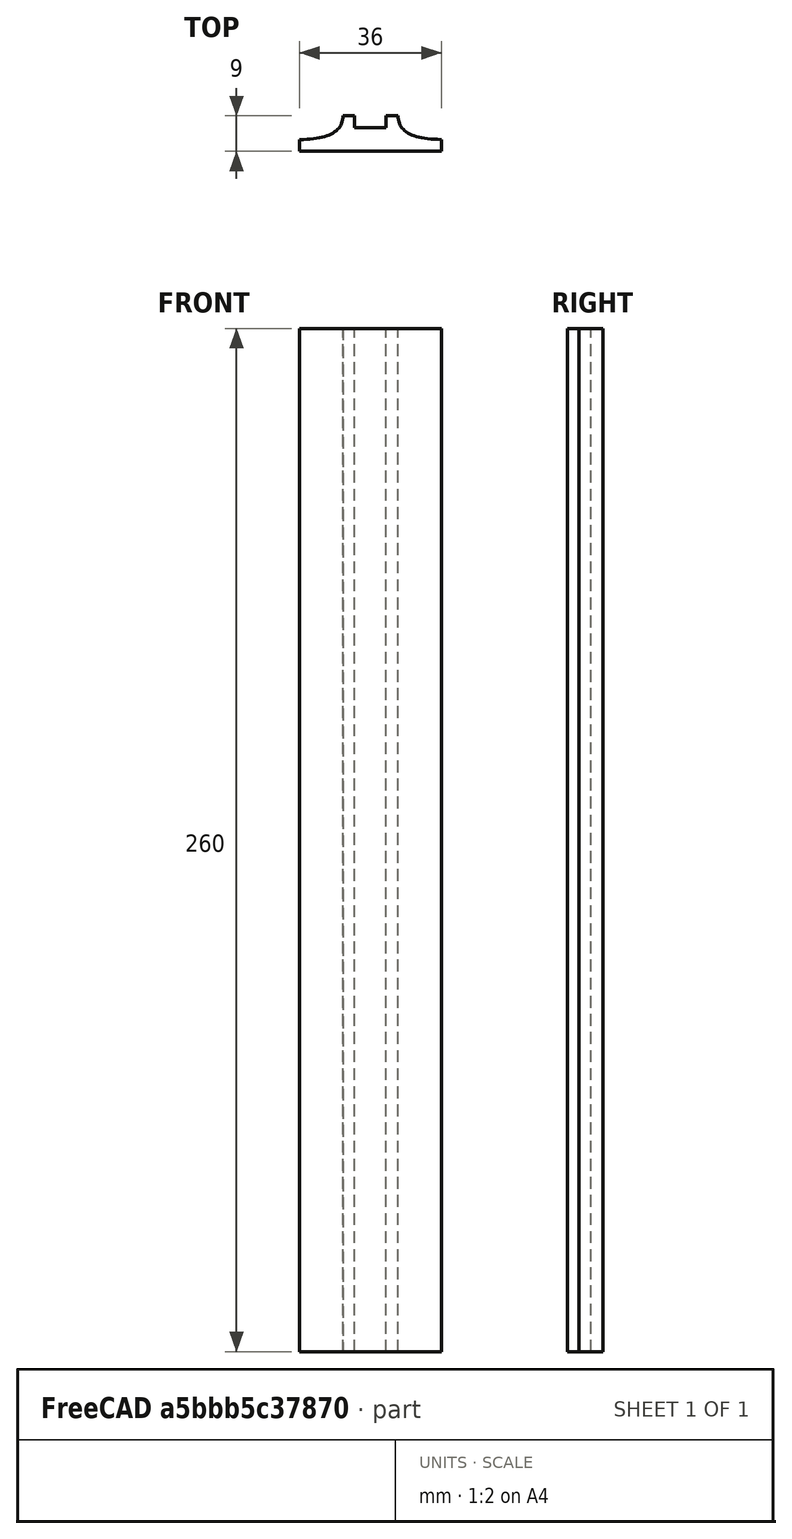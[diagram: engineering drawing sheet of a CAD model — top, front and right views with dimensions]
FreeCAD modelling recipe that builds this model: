
FCSTD DOCUMENT  (FreeCAD 0.19R0.19.2)
Label: laptopStand298.FCStd
License: All rights reserved
LicenseURL: http://en.wikipedia.org/wiki/All_rights_reserved
objects: Sketcher::SketchObject×10, Part::Extrusion×1
note: 11 computed .brp shape members not serialized (recipe doc carries the construction recipe); baked Part::Feature solids carry a one-line shape summary decoded from their .brp

FEATURE [Sketcher::SketchObject] Sketch001  label="legTop"
  FullyConstrained = true
  MapMode = 4
  Placement = pos=(0,0,0) rot=(0.57735,0.57735,0.57735;2.0944rad)
  sketch-geometry (41):
    g0: BSplineCurve PolesCount=3 KnotsCount=2 Degree=2 IsPeriodic=0
    g1: ArcOfCircle CenterX=73.1223 CenterY=-32.291 CenterZ=0 NormalX=0 NormalY=0 NormalZ=1 AngleXU=0 Radius=13 StartAngle=5.92268 EndAngle=9.06428
    g2: ArcOfCircle CenterX=66.7816 CenterY=-49.1439 CenterZ=0 NormalX=0 NormalY=0 NormalZ=1 AngleXU=0 Radius=13 StartAngle=2.78068 EndAngle=5.92131
    g3-g6: Circle x4 (B-spline internal-alignment scaffolding for g7; pole/knot coordinates omitted)
    g7: BSplineCurve PolesCount=4 KnotsCount=2 Degree=3 IsPeriodic=0
    g8: GeomPoint X=28.8094 Y=-19.0875 Z=0
    g9: GeomPoint X=47.0443 Y=-50.4712 Z=0
    g10: Circle CenterX=53.5586 CenterY=-23.2695 CenterZ=0 NormalX=0 NormalY=0 NormalZ=1 AngleXU=0 Radius=3.24518
    g11: LineSegment StartX=17.2232 StartY=-16.0875 StartZ=0 EndX=17.2232 EndY=-19.0875 EndZ=0
    g12: ArcOfCircle CenterX=17.2475 CenterY=-181.166 CenterZ=0 NormalX=0 NormalY=0 NormalZ=1 AngleXU=0 Radius=13 StartAngle=5.92268 EndAngle=7.49361
    g13: ArcOfCircle CenterX=29.5716 CenterY=-148.408 CenterZ=0 NormalX=0 NormalY=0 NormalZ=1 AngleXU=0 Radius=13 StartAngle=4.35228 EndAngle=5.92131
    g14: ArcOfCircle CenterX=35.8967 CenterY=-131.555 CenterZ=0 NormalX=0 NormalY=0 NormalZ=1 AngleXU=0 Radius=13 StartAngle=5.92268 EndAngle=7.49902
    g15: ArcOfCircle CenterX=48.1805 CenterY=-98.7782 CenterZ=0 NormalX=0 NormalY=0 NormalZ=1 AngleXU=0 Radius=13 StartAngle=4.34921 EndAngle=5.92131
    g16: ArcOfCircle CenterX=54.5183 CenterY=-81.9247 CenterZ=0 NormalX=0 NormalY=0 NormalZ=1 AngleXU=0 Radius=13 StartAngle=5.92268 EndAngle=8.70432
    g17: ArcOfCircle CenterX=20.184 CenterY=-217.506 CenterZ=0 NormalX=0 NormalY=0 NormalZ=1 AngleXU=0 Radius=3.81084 StartAngle=1.88136 EndAngle=6.80465
    g18: ArcOfCircle CenterX=36.3663 CenterY=-113.042 CenterZ=0 NormalX=0 NormalY=0 NormalZ=1 AngleXU=0 Radius=3.60555 StartAngle=0.230024 EndAngle=5.3372
    g19: ArcOfCircle CenterX=17.7945 CenterY=-162.686 CenterZ=0 NormalX=0 NormalY=0 NormalZ=1 AngleXU=0 Radius=3.60555 StartAngle=0.230024 EndAngle=5.3372
    g20: ArcOfCircle CenterX=49.8795 CenterY=-62.6074 CenterZ=0 NormalX=0 NormalY=0 NormalZ=1 AngleXU=0 Radius=3.84187 StartAngle=4.46973 EndAngle=9.40343
    g21: LineSegment StartX=48.9563 StartY=-66.3367 StartZ=0 EndX=44.7488 EndY=-73.3482 EndZ=0
    g22: LineSegment StartX=41.085 StartY=-66.3176 StartZ=0 EndX=46.0385 EndY=-62.5254 EndZ=0
    g23: LineSegment StartX=47.0443 StartY=-50.4712 StartZ=0 EndX=41.085 EndY=-66.3176 EndZ=0
    g24: LineSegment StartX=17.2232 StartY=-16.0875 StartZ=0 EndX=117.223 EndY=-16.0875 EndZ=0
    g25: LineSegment StartX=28.8094 StartY=-19.0875 StartZ=0 EndX=17.2232 EndY=-19.0875 EndZ=0
    g26: LineSegment StartX=117.223 StartY=-16.0875 StartZ=0 EndX=117.223 EndY=-19.0875 EndZ=0
    g27: LineSegment StartX=85.2866 StartY=-36.8766 StartZ=0 EndX=78.9396 EndY=-53.7463 EndZ=0
    g28: LineSegment StartX=60.9579 StartY=-27.7053 StartZ=0 EndX=54.6191 EndY=-44.5532 EndZ=0
    g29: LineSegment StartX=23.4884 StartY=-215.608 StartZ=0 EndX=94.6579 EndY=-26.1359 EndZ=0
    g30: LineSegment StartX=19.0195 StartY=-213.878 StartZ=0 EndX=29.4118 EndY=-185.752 EndZ=0
    g31: LineSegment StartX=22.7134 StartY=-166.661 StartZ=0 EndX=21.8316 EndY=-169.001 EndZ=0
    g32: LineSegment StartX=19.9036 StartY=-165.61 StartZ=0 EndX=22.7134 EndY=-166.661 EndZ=0
    g33: LineSegment StartX=21.3051 StartY=-161.864 StartZ=0 EndX=24.1149 EndY=-162.915 EndZ=0
    g34: LineSegment StartX=24.1149 StartY=-162.915 StartZ=0 EndX=24.9906 EndY=-160.574 EndZ=0
    g35: LineSegment StartX=41.7296 StartY=-153.01 StartZ=0 EndX=48.061 EndY=-136.14 EndZ=0
    g36: LineSegment StartX=41.2852 StartY=-117.017 StartZ=0 EndX=40.4148 EndY=-119.365 EndZ=0
    g37: LineSegment StartX=38.4753 StartY=-115.966 StartZ=0 EndX=41.2852 EndY=-117.017 EndZ=0
    g38: LineSegment StartX=39.8769 StartY=-112.22 StartZ=0 EndX=42.6867 EndY=-113.271 EndZ=0
    g39: LineSegment StartX=42.6867 StartY=-113.271 StartZ=0 EndX=43.5622 EndY=-110.93 EndZ=0
    g40: LineSegment StartX=66.6827 StartY=-86.5104 StartZ=0 EndX=60.3386 EndY=-103.381 EndZ=0
  constraints (65):
    c: Block(g0)
    c: Block(g1)
    c: Block(g2)
    c: Weight(g3) = 1
    c: Equal(g3,g4)
    c: Equal(g3,g5)
    c: Equal(g3,g6)
    c: InternalAlignment(g3-g6 -> g7) x4
    c: InternalAlignment(g8,g7)
    c: InternalAlignment(g9,g7)
    c: Block(g10)
    c: Block(g7)
    c: Vertical(g11)
    c: Block(g12)
    c: Block(g13)
    c: Block(g14)
    c: Block(g15)
    c: Block(g16)
    c: Block(g17)
    c: Block(g18)
    c: Block(g19)
    c: Block(g20)
    c: Coincident(g21,g20)
    c: Coincident(g21,g16)
    c: Coincident(g22,g20)
    c: Block(g22)
    c: Coincident(g23,g7)
    c: Coincident(g23,g22)
    c: Coincident(g24,g11)
    c: Horizontal(g24)
    c: Coincident(g25,g7)
    c: Coincident(g25,g11)
    c: Horizontal(g25)
    c: Coincident(g26,g24)
    c: Coincident(g26,g0)
    c: Vertical(g26)
    c: Block(g24)
    c: Coincident(g27,g1)
    c: Coincident(g27,g2)
    c: Coincident(g28,g1)
    c: Coincident(g28,g2)
    c: Coincident(g29,g17)
    c: Coincident(g29,g0)
    c: Coincident(g30,g17)
    c: Coincident(g30,g12)
    c: Coincident(g31,g12)
    c: Coincident(g32,g19)
    c: Coincident(g32,g31)
    c: Block(g31)
    c: Coincident(g33,g19)
    c: Coincident(g34,g33)
    c: Coincident(g34,g13)
    c: Block(g34)
    c: Coincident(g35,g13)
    c: Coincident(g35,g14)
    c: Coincident(g36,g14)
    c: Coincident(g37,g18)
    c: Coincident(g37,g36)
    c: Block(g36)
    c: Coincident(g38,g18)
    c: Coincident(g39,g38)
    c: Coincident(g39,g15)
    c: Block(g39)
    c: Coincident(g40,g16)
    c: Coincident(g40,g15)
FEATURE [Sketcher::SketchObject] Sketch002
  FullyConstrained = true
  sketch-geometry (20):
    g0: LineSegment StartX=-2.77179 StartY=-200.304 StartZ=0 EndX=5.22821 EndY=-200.304 EndZ=0
    g1: LineSegment StartX=5.22821 StartY=-200.304 StartZ=0 EndX=5.22821 EndY=-197.304 EndZ=0
    g2: LineSegment StartX=-2.77179 StartY=-200.304 StartZ=0 EndX=-2.77179 EndY=-197.304 EndZ=0
    g3: LineSegment StartX=5.22821 StartY=-197.304 StartZ=0 EndX=8.22821 EndY=-197.304 EndZ=0
    g4: LineSegment StartX=-2.77179 StartY=-197.304 StartZ=0 EndX=-5.77179 EndY=-197.304 EndZ=0
    g5: LineSegment StartX=19.2282 StartY=-203.304 StartZ=0 EndX=19.2282 EndY=-206.304 EndZ=0
    g6: LineSegment StartX=-16.7718 StartY=-203.304 StartZ=0 EndX=-16.7718 EndY=-206.304 EndZ=0
    g7: LineSegment StartX=-16.7718 StartY=-206.304 StartZ=0 EndX=19.2282 EndY=-206.304 EndZ=0
    g8: Circle CenterX=-16.7718 CenterY=-203.304 CenterZ=0 NormalX=0 NormalY=0 NormalZ=1 AngleXU=0 Radius=1
    g9: Circle CenterX=-5.77179 CenterY=-203.304 CenterZ=0 NormalX=0 NormalY=0 NormalZ=1 AngleXU=0 Radius=1
    g10: Circle CenterX=-5.77179 CenterY=-197.304 CenterZ=0 NormalX=0 NormalY=0 NormalZ=1 AngleXU=0 Radius=1
    g11: BSplineCurve PolesCount=3 KnotsCount=2 Degree=2 IsPeriodic=0
    g12: GeomPoint X=-16.7718 Y=-203.304 Z=0
    g13: GeomPoint X=-5.77179 Y=-197.304 Z=0
    g14: Circle CenterX=19.2282 CenterY=-203.304 CenterZ=0 NormalX=0 NormalY=0 NormalZ=1 AngleXU=0 Radius=1
    g15: Circle CenterX=8.22821 CenterY=-203.304 CenterZ=0 NormalX=0 NormalY=0 NormalZ=1 AngleXU=0 Radius=1
    g16: Circle CenterX=8.22821 CenterY=-197.304 CenterZ=0 NormalX=0 NormalY=0 NormalZ=1 AngleXU=0 Radius=1
    g17: BSplineCurve PolesCount=3 KnotsCount=2 Degree=2 IsPeriodic=0
    g18: GeomPoint X=19.2282 Y=-203.304 Z=0
    g19: GeomPoint X=8.22821 Y=-197.304 Z=0
  constraints (41):
    c: Horizontal(g0)
    c: Distance(g0) = 8
    c: Coincident(g1,g0)
    c: Vertical(g1)
    c: Distance(g1) = 3
    c: Coincident(g2,g0)
    c: Vertical(g2)
    c: Distance(g2) = 3
    c: Coincident(g3,g1)
    c: Horizontal(g3)
    c: Distance(g3) = 3
    c: Coincident(g4,g2)
    c: Horizontal(g4)
    c: Distance(g4) = 3
    c: Vertical(g5)
    c: Vertical(g6)
    c: Coincident(g7,g6)
    c: Coincident(g7,g5)
    c: Weight(g8) = 1
    c: Equal(g8,g9)
    c: Equal(g8,g10)
    c: Coincident(g11,g4)
    c: InternalAlignment(g8,g11)
    c: InternalAlignment(g9,g11)
    c: InternalAlignment(g10,g11)
    c: InternalAlignment(g12,g11)
    c: InternalAlignment(g13,g11)
    c: Coincident(g17,g5)
    c: Weight(g14) = 1
    c: Equal(g14,g15)
    c: Equal(g14,g16)
    c: Coincident(g17,g3)
    c: InternalAlignment(g14,g17)
    c: InternalAlignment(g15,g17)
    c: InternalAlignment(g16,g17)
    c: InternalAlignment(g18,g17)
    c: InternalAlignment(g19,g17)
    c: Block(g7)
    c: Block(g17)
    c: Block(g11)
    c: Block(g6)
FEATURE [Part::Extrusion] Extrude003
  Base = -> Sketch002
  Dir = (0,0,1)
  DirMode = 2
  FaceMakerClass = Part::FaceMakerBullseye
  LengthFwd = 260
  LengthRev = 0
  Solid = true
  Symmetric = false
FEATURE [Sketcher::SketchObject] Sketch003  label="original"
  FullyConstrained = false
  sketch-geometry (469):
    g0: LineSegment StartX=-42.9272 StartY=136.221 StartZ=0 EndX=-42.9272 EndY=-103.779 EndZ=0
    g1: LineSegment StartX=407.073 StartY=136.221 StartZ=0 EndX=407.073 EndY=-103.779 EndZ=0
    g2: ArcOfCircle CenterX=-26.9272 CenterY=-83.7794 CenterZ=0 NormalX=0 NormalY=0 NormalZ=1 AngleXU=0 Radius=8 StartAngle=3.14159 EndAngle=6.28319
    g3: ArcOfCircle CenterX=391.073 CenterY=-83.7794 CenterZ=0 NormalX=0 NormalY=0 NormalZ=1 AngleXU=0 Radius=8 StartAngle=3.14159 EndAngle=6.28319
    g4: Circle CenterX=175.022 CenterY=27.0628 CenterZ=0 NormalX=0 NormalY=0 NormalZ=1 AngleXU=0 Radius=1
    g5: Circle CenterX=179.022 CenterY=24.8665 CenterZ=0 NormalX=0 NormalY=0 NormalZ=1 AngleXU=0 Radius=1
    g6: Circle CenterX=179.022 CenterY=27.0628 CenterZ=0 NormalX=0 NormalY=0 NormalZ=1 AngleXU=0 Radius=1
    g7: BSplineCurve PolesCount=3 KnotsCount=2 Degree=2 IsPeriodic=0
    g8: GeomPoint X=175.022 Y=27.0628 Z=0
    g9: GeomPoint X=179.022 Y=27.0628 Z=0
    g10: Circle CenterX=189.124 CenterY=27.0628 CenterZ=0 NormalX=0 NormalY=0 NormalZ=1 AngleXU=0 Radius=1
    g11: Circle CenterX=185.124 CenterY=24.8665 CenterZ=0 NormalX=0 NormalY=0 NormalZ=1 AngleXU=0 Radius=1
    g12: Circle CenterX=185.124 CenterY=27.0628 CenterZ=0 NormalX=0 NormalY=0 NormalZ=1 AngleXU=0 Radius=1
    g13: BSplineCurve PolesCount=3 KnotsCount=2 Degree=2 IsPeriodic=0
    g14: GeomPoint X=189.124 Y=27.0628 Z=0
    g15: GeomPoint X=185.124 Y=27.0628 Z=0
    g16: Circle CenterX=175.022 CenterY=5.37834 CenterZ=0 NormalX=0 NormalY=0 NormalZ=1 AngleXU=0 Radius=1
    g17: Circle CenterX=179.022 CenterY=7.57463 CenterZ=0 NormalX=0 NormalY=0 NormalZ=1 AngleXU=0 Radius=1
    g18: Circle CenterX=179.022 CenterY=5.34704 CenterZ=0 NormalX=0 NormalY=0 NormalZ=1 AngleXU=0 Radius=1
    g19: BSplineCurve PolesCount=3 KnotsCount=2 Degree=2 IsPeriodic=0
    g20: GeomPoint X=175.022 Y=5.37834 Z=0
    g21: GeomPoint X=179.022 Y=5.34704 Z=0
    g22: Circle CenterX=189.124 CenterY=5.37834 CenterZ=0 NormalX=0 NormalY=0 NormalZ=1 AngleXU=0 Radius=1
    g23: Circle CenterX=185.124 CenterY=7.57463 CenterZ=0 NormalX=0 NormalY=0 NormalZ=1 AngleXU=0 Radius=1
    g24: Circle CenterX=185.124 CenterY=5.34704 CenterZ=0 NormalX=0 NormalY=0 NormalZ=1 AngleXU=0 Radius=1
    g25: BSplineCurve PolesCount=3 KnotsCount=2 Degree=2 IsPeriodic=0
    g26: GeomPoint X=189.124 Y=5.37834 Z=0
    g27: GeomPoint X=185.124 Y=5.34704 Z=0
    g28: Circle CenterX=165.871 CenterY=18.1458 CenterZ=0 NormalX=0 NormalY=0 NormalZ=1 AngleXU=0 Radius=1
    g29: Circle CenterX=169.377 CenterY=16.2206 CenterZ=0 NormalX=0 NormalY=0 NormalZ=1 AngleXU=0 Radius=1
    g30: Circle CenterX=165.871 CenterY=14.2956 CenterZ=0 NormalX=0 NormalY=0 NormalZ=1 AngleXU=0 Radius=1
    g31: BSplineCurve PolesCount=3 KnotsCount=2 Degree=2 IsPeriodic=0
    g32: GeomPoint X=165.871 Y=18.1458 Z=0
    g33: GeomPoint X=165.871 Y=14.2956 Z=0
    g34: Circle CenterX=198.275 CenterY=18.1318 CenterZ=0 NormalX=0 NormalY=0 NormalZ=1 AngleXU=0 Radius=1
    g35: Circle CenterX=194.768 CenterY=16.2206 CenterZ=0 NormalX=0 NormalY=0 NormalZ=1 AngleXU=0 Radius=1
    g36: Circle CenterX=198.264 CenterY=14.2963 CenterZ=0 NormalX=0 NormalY=0 NormalZ=1 AngleXU=0 Radius=1
    g37: BSplineCurve PolesCount=3 KnotsCount=2 Degree=2 IsPeriodic=0
    g38: GeomPoint X=198.275 Y=18.1318 Z=0
    g39: GeomPoint X=198.264 Y=14.2963 Z=0
    g40: LineSegment StartX=407.073 StartY=-103.779 StartZ=0 EndX=-42.9272 EndY=-103.779 EndZ=0
    g41: Circle CenterX=125.607 CenterY=54.1951 CenterZ=0 NormalX=0 NormalY=0 NormalZ=1 AngleXU=0 Radius=1
    g42: Circle CenterX=139.632 CenterY=46.4944 CenterZ=0 NormalX=0 NormalY=0 NormalZ=1 AngleXU=0 Radius=1
    g43: Circle CenterX=127.326 CenterY=56.7187 CenterZ=0 NormalX=0 NormalY=0 NormalZ=1 AngleXU=0 Radius=1
    g44: BSplineCurve PolesCount=3 KnotsCount=2 Degree=2 IsPeriodic=0
    g45: GeomPoint X=125.607 Y=54.1951 Z=0
    g46: GeomPoint X=127.326 Y=56.7187 Z=0
    g47: Circle CenterX=236.824 CenterY=56.7187 CenterZ=0 NormalX=0 NormalY=0 NormalZ=1 AngleXU=0 Radius=1
    g48: Circle CenterX=224.513 CenterY=46.4944 CenterZ=0 NormalX=0 NormalY=0 NormalZ=1 AngleXU=0 Radius=1
    g49: Circle CenterX=238.538 CenterY=54.1951 CenterZ=0 NormalX=0 NormalY=0 NormalZ=1 AngleXU=0 Radius=1
    g50: BSplineCurve PolesCount=3 KnotsCount=2 Degree=2 IsPeriodic=0
    g51: GeomPoint X=236.824 Y=56.7187 Z=0
    g52: GeomPoint X=238.538 Y=54.1951 Z=0
    g53: Circle CenterX=238.538 CenterY=-21.7516 CenterZ=0 NormalX=0 NormalY=0 NormalZ=1 AngleXU=0 Radius=1
    g54: Circle CenterX=224.513 CenterY=-14.0532 CenterZ=0 NormalX=0 NormalY=0 NormalZ=1 AngleXU=0 Radius=1
    g55: Circle CenterX=236.584 CenterY=-24.2775 CenterZ=0 NormalX=0 NormalY=0 NormalZ=1 AngleXU=0 Radius=1
    g56: BSplineCurve PolesCount=3 KnotsCount=2 Degree=2 IsPeriodic=0
    g57: GeomPoint X=238.538 Y=-21.7516 Z=0
    g58: GeomPoint X=236.584 Y=-24.2775 Z=0
    g59: Circle CenterX=125.607 CenterY=-21.7539 CenterZ=0 NormalX=0 NormalY=0 NormalZ=1 AngleXU=0 Radius=1
    g60: Circle CenterX=139.632 CenterY=-14.0532 CenterZ=0 NormalX=0 NormalY=0 NormalZ=1 AngleXU=0 Radius=1
    g61: Circle CenterX=127.325 CenterY=-24.2775 CenterZ=0 NormalX=0 NormalY=0 NormalZ=1 AngleXU=0 Radius=1
    g62: BSplineCurve PolesCount=3 KnotsCount=2 Degree=2 IsPeriodic=0
    g63: GeomPoint X=125.607 Y=-21.7539 Z=0
    g64: GeomPoint X=127.325 Y=-24.2775 Z=0
    g65: Circle CenterX=302.996 CenterY=111.695 CenterZ=0 NormalX=0 NormalY=0 NormalZ=1 AngleXU=0 Radius=1
    g66: Circle CenterX=306.073 CenterY=114.251 CenterZ=0 NormalX=0 NormalY=0 NormalZ=1 AngleXU=0 Radius=1
    g67: Circle CenterX=306.073 CenterY=110.251 CenterZ=0 NormalX=0 NormalY=0 NormalZ=1 AngleXU=0 Radius=1
    g68: BSplineCurve PolesCount=3 KnotsCount=2 Degree=2 IsPeriodic=0
    g69: GeomPoint X=302.996 Y=111.695 Z=0
    g70: GeomPoint X=306.073 Y=110.251 Z=0
    g71: Circle CenterX=306.073 CenterY=95.2763 CenterZ=0 NormalX=0 NormalY=0 NormalZ=1 AngleXU=0 Radius=1
    g72: Circle CenterX=306.073 CenterY=91.2763 CenterZ=0 NormalX=0 NormalY=0 NormalZ=1 AngleXU=0 Radius=1
    g73: Circle CenterX=302.567 CenterY=89.3511 CenterZ=0 NormalX=0 NormalY=0 NormalZ=1 AngleXU=0 Radius=1
    g74: BSplineCurve PolesCount=3 KnotsCount=2 Degree=2 IsPeriodic=0
    g75: GeomPoint X=306.073 Y=95.2763 Z=0
    g76: GeomPoint X=302.567 Y=89.3511 Z=0
    g77: LineSegment StartX=306.073 StartY=110.251 StartZ=0 EndX=306.073 EndY=95.2763 EndZ=0
    g78: LineSegment StartX=302.996 StartY=111.695 StartZ=0 EndX=236.824 EndY=56.7187 EndZ=0
    g79: LineSegment StartX=238.538 StartY=54.1951 StartZ=0 EndX=302.567 EndY=89.3511 EndZ=0
    g80: Circle CenterX=61.1496 CenterY=111.695 CenterZ=0 NormalX=0 NormalY=0 NormalZ=1 AngleXU=0 Radius=1
    g81: Circle CenterX=58.0728 CenterY=114.251 CenterZ=0 NormalX=0 NormalY=0 NormalZ=1 AngleXU=0 Radius=1
    g82: Circle CenterX=58.0728 CenterY=110.251 CenterZ=0 NormalX=0 NormalY=0 NormalZ=1 AngleXU=0 Radius=1
    g83: BSplineCurve PolesCount=3 KnotsCount=2 Degree=2 IsPeriodic=0
    g84: GeomPoint X=61.1496 Y=111.695 Z=0
    g85: GeomPoint X=58.0728 Y=110.251 Z=0
    g86: Circle CenterX=61.5791 CenterY=89.3511 CenterZ=0 NormalX=0 NormalY=0 NormalZ=1 AngleXU=0 Radius=1
    g87: Circle CenterX=58.0728 CenterY=91.2763 CenterZ=0 NormalX=0 NormalY=0 NormalZ=1 AngleXU=0 Radius=1
    g88: Circle CenterX=58.0728 CenterY=95.2763 CenterZ=0 NormalX=0 NormalY=0 NormalZ=1 AngleXU=0 Radius=1
    g89: BSplineCurve PolesCount=3 KnotsCount=2 Degree=2 IsPeriodic=0
    g90: GeomPoint X=61.5791 Y=89.3511 Z=0
    g91: GeomPoint X=58.0728 Y=95.2763 Z=0
    g92: LineSegment StartX=58.0728 StartY=110.251 StartZ=0 EndX=58.0728 EndY=95.2763 EndZ=0
    g93: LineSegment StartX=61.1496 StartY=111.695 StartZ=0 EndX=127.326 EndY=56.7187 EndZ=0
    g94: LineSegment StartX=125.607 StartY=54.1951 StartZ=0 EndX=61.5791 EndY=89.3511 EndZ=0
    g95: Circle CenterX=61.5791 CenterY=-56.9099 CenterZ=0 NormalX=0 NormalY=0 NormalZ=1 AngleXU=0 Radius=1
    g96: Circle CenterX=58.0728 CenterY=-58.8351 CenterZ=0 NormalX=0 NormalY=0 NormalZ=1 AngleXU=0 Radius=1
    g97: Circle CenterX=58.0728 CenterY=-62.8351 CenterZ=0 NormalX=0 NormalY=0 NormalZ=1 AngleXU=0 Radius=1
    g98: BSplineCurve PolesCount=3 KnotsCount=2 Degree=2 IsPeriodic=0
    g99: GeomPoint X=61.5791 Y=-56.9099 Z=0
    g100: GeomPoint X=58.0728 Y=-62.8351 Z=0
    g101: Circle CenterX=58.0728 CenterY=-77.8102 CenterZ=0 NormalX=0 NormalY=0 NormalZ=1 AngleXU=0 Radius=1
    g102: Circle CenterX=58.0728 CenterY=-81.8102 CenterZ=0 NormalX=0 NormalY=0 NormalZ=1 AngleXU=0 Radius=1
    g103: Circle CenterX=61.1496 CenterY=-79.2541 CenterZ=0 NormalX=0 NormalY=0 NormalZ=1 AngleXU=0 Radius=1
    g104: BSplineCurve PolesCount=3 KnotsCount=2 Degree=2 IsPeriodic=0
    g105: GeomPoint X=58.0728 Y=-77.8102 Z=0
    g106: GeomPoint X=61.1496 Y=-79.2541 Z=0
    g107: LineSegment StartX=58.0728 StartY=-62.8351 StartZ=0 EndX=58.0728 EndY=-77.8102 EndZ=0
    g108: LineSegment StartX=61.1496 StartY=-79.2541 StartZ=0 EndX=127.325 EndY=-24.2775 EndZ=0
    g109: LineSegment StartX=125.607 StartY=-21.7539 StartZ=0 EndX=61.5791 EndY=-56.9099 EndZ=0
    g110: Circle CenterX=302.567 CenterY=-56.9099 CenterZ=0 NormalX=0 NormalY=0 NormalZ=1 AngleXU=0 Radius=1
    g111: Circle CenterX=306.073 CenterY=-58.8351 CenterZ=0 NormalX=0 NormalY=0 NormalZ=1 AngleXU=0 Radius=1
    g112: Circle CenterX=306.073 CenterY=-62.8351 CenterZ=0 NormalX=0 NormalY=0 NormalZ=1 AngleXU=0 Radius=1
    g113: BSplineCurve PolesCount=3 KnotsCount=2 Degree=2 IsPeriodic=0
    g114: GeomPoint X=302.567 Y=-56.9099 Z=0
    g115: GeomPoint X=306.073 Y=-62.8351 Z=0
    g116: Circle CenterX=302.996 CenterY=-79.2541 CenterZ=0 NormalX=0 NormalY=0 NormalZ=1 AngleXU=0 Radius=1
    g117: Circle CenterX=306.073 CenterY=-81.8102 CenterZ=0 NormalX=0 NormalY=0 NormalZ=1 AngleXU=0 Radius=1
    g118: Circle CenterX=306.073 CenterY=-77.8102 CenterZ=0 NormalX=0 NormalY=0 NormalZ=1 AngleXU=0 Radius=1
    g119: BSplineCurve PolesCount=3 KnotsCount=2 Degree=2 IsPeriodic=0
    g120: GeomPoint X=302.996 Y=-79.2541 Z=0
    g121: GeomPoint X=306.073 Y=-77.8102 Z=0
    g122: LineSegment StartX=306.073 StartY=-62.8351 StartZ=0 EndX=306.073 EndY=-77.8102 EndZ=0
    g123: LineSegment StartX=302.996 StartY=-79.2541 StartZ=0 EndX=236.584 EndY=-24.2775 EndZ=0
    g124: LineSegment StartX=238.538 StartY=-21.7516 StartZ=0 EndX=302.567 EndY=-56.9099 EndZ=0
    g125: Circle CenterX=61.6457 CenterY=-88.8112 CenterZ=0 NormalX=0 NormalY=0 NormalZ=1 AngleXU=0 Radius=1
    g126: Circle CenterX=58.0728 CenterY=-91.7794 CenterZ=0 NormalX=0 NormalY=0 NormalZ=1 AngleXU=0 Radius=1
    g127: Circle CenterX=63.9135 CenterY=-91.7791 CenterZ=0 NormalX=0 NormalY=0 NormalZ=1 AngleXU=0 Radius=1
    g128: BSplineCurve PolesCount=3 KnotsCount=2 Degree=2 IsPeriodic=0
    g129: GeomPoint X=61.6457 Y=-88.8112 Z=0
    g130: GeomPoint X=63.9135 Y=-91.7791 Z=0
    g131: Circle CenterX=179.022 CenterY=-85.8163 CenterZ=0 NormalX=0 NormalY=0 NormalZ=1 AngleXU=0 Radius=1
    g132: Circle CenterX=179.022 CenterY=-91.7794 CenterZ=0 NormalX=0 NormalY=0 NormalZ=1 AngleXU=0 Radius=1
    g133: Circle CenterX=171.895 CenterY=-91.7791 CenterZ=0 NormalX=0 NormalY=0 NormalZ=1 AngleXU=0 Radius=1
    g134: BSplineCurve PolesCount=3 KnotsCount=2 Degree=2 IsPeriodic=0
    g135: GeomPoint X=179.022 Y=-85.8163 Z=0
    g136: GeomPoint X=171.895 Y=-91.7791 Z=0
    g137: Circle CenterX=185.124 CenterY=-86.2028 CenterZ=0 NormalX=0 NormalY=0 NormalZ=1 AngleXU=0 Radius=1
    g138: Circle CenterX=185.124 CenterY=-91.7794 CenterZ=0 NormalX=0 NormalY=0 NormalZ=1 AngleXU=0 Radius=1
    g139: Circle CenterX=191.747 CenterY=-91.7794 CenterZ=0 NormalX=0 NormalY=0 NormalZ=1 AngleXU=0 Radius=1
    g140: BSplineCurve PolesCount=3 KnotsCount=2 Degree=2 IsPeriodic=0
    g141: GeomPoint X=185.124 Y=-86.2028 Z=0
    g142: GeomPoint X=191.747 Y=-91.7794 Z=0
    g143: Circle CenterX=299.888 CenterY=-86.6413 CenterZ=0 NormalX=0 NormalY=0 NormalZ=1 AngleXU=0 Radius=1
    g144: Circle CenterX=306.073 CenterY=-91.7794 CenterZ=0 NormalX=0 NormalY=0 NormalZ=1 AngleXU=0 Radius=1
    g145: Circle CenterX=298.776 CenterY=-91.7794 CenterZ=0 NormalX=0 NormalY=0 NormalZ=1 AngleXU=0 Radius=1
    g146: BSplineCurve PolesCount=3 KnotsCount=2 Degree=2 IsPeriodic=0
    g147: GeomPoint X=299.888 Y=-86.6413 Z=0
    g148: GeomPoint X=298.776 Y=-91.7794 Z=0
    g149: LineSegment StartX=189.124 StartY=5.37834 StartZ=0 EndX=299.888 EndY=-86.6413 EndZ=0
    g150: LineSegment StartX=298.776 StartY=-91.7794 StartZ=0 EndX=191.747 EndY=-91.7794 EndZ=0
    g151: LineSegment StartX=185.124 StartY=-86.2028 StartZ=0 EndX=185.124 EndY=5.34704 EndZ=0
    g152: LineSegment StartX=179.022 StartY=5.34704 StartZ=0 EndX=179.022 EndY=-85.8163 EndZ=0
    g153: LineSegment StartX=171.895 StartY=-91.7791 StartZ=0 EndX=63.9135 EndY=-91.7791 EndZ=0
    g154: LineSegment StartX=61.6457 StartY=-88.8112 StartZ=0 EndX=175.022 EndY=5.37834 EndZ=0
    g155: Circle CenterX=302.073 CenterY=124.221 CenterZ=0 NormalX=0 NormalY=0 NormalZ=1 AngleXU=0 Radius=1
    g156: Circle CenterX=306.073 CenterY=124.221 CenterZ=0 NormalX=0 NormalY=0 NormalZ=1 AngleXU=0 Radius=1
    g157: Circle CenterX=302.996 CenterY=121.665 CenterZ=0 NormalX=0 NormalY=0 NormalZ=1 AngleXU=0 Radius=1
    g158: BSplineCurve PolesCount=3 KnotsCount=2 Degree=2 IsPeriodic=0
    g159: GeomPoint X=302.073 Y=124.221 Z=0
    g160: GeomPoint X=302.996 Y=121.665 Z=0
    g161: Circle CenterX=189.124 CenterY=124.221 CenterZ=0 NormalX=0 NormalY=0 NormalZ=1 AngleXU=0 Radius=1
    g162: Circle CenterX=185.124 CenterY=124.221 CenterZ=0 NormalX=0 NormalY=0 NormalZ=1 AngleXU=0 Radius=1
    g163: Circle CenterX=185.124 CenterY=120.221 CenterZ=0 NormalX=0 NormalY=0 NormalZ=1 AngleXU=0 Radius=1
    g164: BSplineCurve PolesCount=3 KnotsCount=2 Degree=2 IsPeriodic=0
    g165: GeomPoint X=189.124 Y=124.221 Z=0
    g166: GeomPoint X=185.124 Y=120.221 Z=0
    g167: Circle CenterX=175.022 CenterY=124.221 CenterZ=0 NormalX=0 NormalY=0 NormalZ=1 AngleXU=0 Radius=1
    g168: Circle CenterX=179.022 CenterY=124.221 CenterZ=0 NormalX=0 NormalY=0 NormalZ=1 AngleXU=0 Radius=1
    g169: Circle CenterX=179.022 CenterY=120.221 CenterZ=0 NormalX=0 NormalY=0 NormalZ=1 AngleXU=0 Radius=1
    g170: BSplineCurve PolesCount=3 KnotsCount=2 Degree=2 IsPeriodic=0
    g171: GeomPoint X=175.022 Y=124.221 Z=0
    g172: GeomPoint X=179.022 Y=120.221 Z=0
    g173: Circle CenterX=62.0728 CenterY=124.221 CenterZ=0 NormalX=0 NormalY=0 NormalZ=1 AngleXU=0 Radius=1
    g174: Circle CenterX=58.0728 CenterY=124.221 CenterZ=0 NormalX=0 NormalY=0 NormalZ=1 AngleXU=0 Radius=1
    g175: Circle CenterX=61.1496 CenterY=121.665 CenterZ=0 NormalX=0 NormalY=0 NormalZ=1 AngleXU=0 Radius=1
    g176: BSplineCurve PolesCount=3 KnotsCount=2 Degree=2 IsPeriodic=0
    g177: GeomPoint X=62.0728 Y=124.221 Z=0
    g178: GeomPoint X=61.1496 Y=121.665 Z=0
    g179: LineSegment StartX=179.022 StartY=120.221 StartZ=0 EndX=179.022 EndY=27.0628 EndZ=0
    g180: LineSegment StartX=185.124 StartY=27.0628 StartZ=0 EndX=185.124 EndY=120.221 EndZ=0
    g181: LineSegment StartX=302.996 StartY=121.665 StartZ=0 EndX=189.124 EndY=27.0628 EndZ=0
    g182: LineSegment StartX=175.022 StartY=27.0628 StartZ=0 EndX=61.1496 EndY=121.665 EndZ=0
    g183: Circle CenterX=61.5791 CenterY=75.4095 CenterZ=0 NormalX=0 NormalY=0 NormalZ=1 AngleXU=0 Radius=1
    g184: Circle CenterX=58.0728 CenterY=77.3346 CenterZ=0 NormalX=0 NormalY=0 NormalZ=1 AngleXU=0 Radius=1
    g185: Circle CenterX=58.0728 CenterY=73.3346 CenterZ=0 NormalX=0 NormalY=0 NormalZ=1 AngleXU=0 Radius=1
    g186: BSplineCurve PolesCount=3 KnotsCount=2 Degree=2 IsPeriodic=0
    g187: GeomPoint X=61.5791 Y=75.4095 Z=0
    g188: GeomPoint X=58.0728 Y=73.3346 Z=0
    g189: Circle CenterX=58.0728 CenterY=-40.8935 CenterZ=0 NormalX=0 NormalY=0 NormalZ=1 AngleXU=0 Radius=1
    g190: Circle CenterX=58.0728 CenterY=-44.8935 CenterZ=0 NormalX=0 NormalY=0 NormalZ=1 AngleXU=0 Radius=1
    g191: Circle CenterX=61.5791 CenterY=-42.9683 CenterZ=0 NormalX=0 NormalY=0 NormalZ=1 AngleXU=0 Radius=1
    g192: BSplineCurve PolesCount=3 KnotsCount=2 Degree=2 IsPeriodic=0
    g193: GeomPoint X=58.0728 Y=-40.8935 Z=0
    g194: GeomPoint X=61.5791 Y=-42.9683 Z=0
    g195: LineSegment StartX=61.5791 StartY=-42.9683 StartZ=0 EndX=165.871 EndY=14.2956 EndZ=0
    g196: LineSegment StartX=165.871 StartY=18.1458 StartZ=0 EndX=61.5791 EndY=75.4095 EndZ=0
    g197: LineSegment StartX=58.0728 StartY=73.3346 StartZ=0 EndX=58.0728 EndY=-40.8935 EndZ=0
    g198: Circle CenterX=302.567 CenterY=-42.9683 CenterZ=0 NormalX=0 NormalY=0 NormalZ=1 AngleXU=0 Radius=1
    g199: Circle CenterX=306.073 CenterY=-44.8935 CenterZ=0 NormalX=0 NormalY=0 NormalZ=1 AngleXU=0 Radius=1
    g200: Circle CenterX=306.073 CenterY=-40.8935 CenterZ=0 NormalX=0 NormalY=0 NormalZ=1 AngleXU=0 Radius=1
    g201: BSplineCurve PolesCount=3 KnotsCount=2 Degree=2 IsPeriodic=0
    g202: GeomPoint X=302.567 Y=-42.9683 Z=0
    g203: GeomPoint X=306.073 Y=-40.8935 Z=0
    g204: Circle CenterX=306.073 CenterY=73.3346 CenterZ=0 NormalX=0 NormalY=0 NormalZ=1 AngleXU=0 Radius=1
    g205: Circle CenterX=306.073 CenterY=77.3346 CenterZ=0 NormalX=0 NormalY=0 NormalZ=1 AngleXU=0 Radius=1
    g206: Circle CenterX=302.535 CenterY=75.4095 CenterZ=0 NormalX=0 NormalY=0 NormalZ=1 AngleXU=0 Radius=1
    g207: BSplineCurve PolesCount=3 KnotsCount=2 Degree=2 IsPeriodic=0
    g208: GeomPoint X=306.073 Y=73.3346 Z=0
    g209: GeomPoint X=302.535 Y=75.4095 Z=0
    g210: LineSegment StartX=302.567 StartY=-42.9683 StartZ=0 EndX=198.264 EndY=14.2963 EndZ=0
    g211: LineSegment StartX=198.275 StartY=18.1318 StartZ=0 EndX=302.535 EndY=75.4095 EndZ=0
    g212: LineSegment StartX=306.073 StartY=73.3346 StartZ=0 EndX=306.073 EndY=-40.8935 EndZ=0
    g213: LineSegment StartX=322.073 StartY=105.865 StartZ=0 EndX=328.643 EndY=105.865 EndZ=0
    g214: LineSegment StartX=318.073 StartY=120.221 StartZ=0 EndX=318.073 EndY=109.865 EndZ=0
    g215: LineSegment StartX=336.157 StartY=107.779 StartZ=0 EndX=362.567 EndY=122.294 EndZ=0
    g216: Circle CenterX=362.073 CenterY=124.221 CenterZ=0 NormalX=0 NormalY=0 NormalZ=1 AngleXU=0 Radius=1
    g217: Circle CenterX=366.073 CenterY=124.221 CenterZ=0 NormalX=0 NormalY=0 NormalZ=1 AngleXU=0 Radius=1
    g218: Circle CenterX=362.567 CenterY=122.294 CenterZ=0 NormalX=0 NormalY=0 NormalZ=1 AngleXU=0 Radius=1
    g219: BSplineCurve PolesCount=3 KnotsCount=2 Degree=2 IsPeriodic=0
    g220: GeomPoint X=362.073 Y=124.221 Z=0
    g221: GeomPoint X=362.567 Y=122.294 Z=0
    g222: Circle CenterX=322.073 CenterY=124.221 CenterZ=0 NormalX=0 NormalY=0 NormalZ=1 AngleXU=0 Radius=1
    g223: Circle CenterX=318.073 CenterY=124.221 CenterZ=0 NormalX=0 NormalY=0 NormalZ=1 AngleXU=0 Radius=1
    g224: Circle CenterX=318.073 CenterY=120.221 CenterZ=0 NormalX=0 NormalY=0 NormalZ=1 AngleXU=0 Radius=1
    g225: BSplineCurve PolesCount=3 KnotsCount=2 Degree=2 IsPeriodic=0
    g226: GeomPoint X=322.073 Y=124.221 Z=0
    g227: GeomPoint X=318.073 Y=120.221 Z=0
    g228: Circle CenterX=322.073 CenterY=105.865 CenterZ=0 NormalX=0 NormalY=0 NormalZ=1 AngleXU=0 Radius=1
    g229: Circle CenterX=318.073 CenterY=105.865 CenterZ=0 NormalX=0 NormalY=0 NormalZ=1 AngleXU=0 Radius=1
    g230: Circle CenterX=318.073 CenterY=109.865 CenterZ=0 NormalX=0 NormalY=0 NormalZ=1 AngleXU=0 Radius=1
    g231: BSplineCurve PolesCount=3 KnotsCount=2 Degree=2 IsPeriodic=0
    g232: GeomPoint X=322.073 Y=105.865 Z=0
    g233: GeomPoint X=318.073 Y=109.865 Z=0
    g234: Circle CenterX=336.157 CenterY=107.779 CenterZ=0 NormalX=0 NormalY=0 NormalZ=1 AngleXU=0 Radius=1
    g235: Circle CenterX=332.651 CenterY=105.853 CenterZ=0 NormalX=0 NormalY=0 NormalZ=1 AngleXU=0 Radius=1
    g236: Circle CenterX=328.643 CenterY=105.865 CenterZ=0 NormalX=0 NormalY=0 NormalZ=1 AngleXU=0 Radius=1
    g237: BSplineCurve PolesCount=3 KnotsCount=2 Degree=2 IsPeriodic=0
    g238: GeomPoint X=336.157 Y=107.779 Z=0
    g239: GeomPoint X=328.643 Y=105.865 Z=0
    g240: LineSegment StartX=322.073 StartY=124.221 StartZ=0 EndX=362.073 EndY=124.221 EndZ=0
    g241: Circle CenterX=371.567 CenterY=-80.8644 CenterZ=0 NormalX=0 NormalY=0 NormalZ=1 AngleXU=0 Radius=1
    g242: Circle CenterX=375.073 CenterY=-82.7896 CenterZ=0 NormalX=0 NormalY=0 NormalZ=1 AngleXU=0 Radius=1
    g243: Circle CenterX=375.073 CenterY=-78.7896 CenterZ=0 NormalX=0 NormalY=0 NormalZ=1 AngleXU=0 Radius=1
    g244: BSplineCurve PolesCount=3 KnotsCount=2 Degree=2 IsPeriodic=0
    g245: GeomPoint X=371.567 Y=-80.8644 Z=0
    g246: GeomPoint X=375.073 Y=-78.7896 Z=0
    g247: Circle CenterX=321.579 CenterY=-53.4075 CenterZ=0 NormalX=0 NormalY=0 NormalZ=1 AngleXU=0 Radius=1
    g248: Circle CenterX=318.073 CenterY=-51.4823 CenterZ=0 NormalX=0 NormalY=0 NormalZ=1 AngleXU=0 Radius=1
    g249: Circle CenterX=318.073 CenterY=-47.4805 CenterZ=0 NormalX=0 NormalY=0 NormalZ=1 AngleXU=0 Radius=1
    g250: BSplineCurve PolesCount=3 KnotsCount=2 Degree=2 IsPeriodic=0
    g251: GeomPoint X=321.579 Y=-53.4075 Z=0
    g252: GeomPoint X=318.073 Y=-47.4805 Z=0
    g253: LineSegment StartX=371.567 StartY=-80.8644 StartZ=0 EndX=321.579 EndY=-53.4075 EndZ=0
    g254: Circle CenterX=321.579 CenterY=-67.3492 CenterZ=0 NormalX=0 NormalY=0 NormalZ=1 AngleXU=0 Radius=1
    g255: Circle CenterX=318.073 CenterY=-65.424 CenterZ=0 NormalX=0 NormalY=0 NormalZ=1 AngleXU=0 Radius=1
    g256: Circle CenterX=318.073 CenterY=-69.424 CenterZ=0 NormalX=0 NormalY=0 NormalZ=1 AngleXU=0 Radius=1
    g257: BSplineCurve PolesCount=3 KnotsCount=2 Degree=2 IsPeriodic=0
    g258: GeomPoint X=321.579 Y=-67.3492 Z=0
    g259: GeomPoint X=318.073 Y=-69.424 Z=0
    g260: Circle CenterX=362.567 CenterY=-89.8542 CenterZ=0 NormalX=0 NormalY=0 NormalZ=1 AngleXU=0 Radius=1
    g261: Circle CenterX=366.073 CenterY=-91.7794 CenterZ=0 NormalX=0 NormalY=0 NormalZ=1 AngleXU=0 Radius=1
    g262: Circle CenterX=362.073 CenterY=-91.7794 CenterZ=0 NormalX=0 NormalY=0 NormalZ=1 AngleXU=0 Radius=1
    g263: BSplineCurve PolesCount=3 KnotsCount=2 Degree=2 IsPeriodic=0
    g264: GeomPoint X=362.567 Y=-89.8542 Z=0
    g265: GeomPoint X=362.073 Y=-91.7794 Z=0
    g266: Circle CenterX=322.073 CenterY=-91.7794 CenterZ=0 NormalX=0 NormalY=0 NormalZ=1 AngleXU=0 Radius=1
    g267: Circle CenterX=318.073 CenterY=-91.7794 CenterZ=0 NormalX=0 NormalY=0 NormalZ=1 AngleXU=0 Radius=1
    g268: Circle CenterX=318.073 CenterY=-87.7794 CenterZ=0 NormalX=0 NormalY=0 NormalZ=1 AngleXU=0 Radius=1
    g269: BSplineCurve PolesCount=3 KnotsCount=2 Degree=2 IsPeriodic=0
    g270: GeomPoint X=322.073 Y=-91.7794 Z=0
    g271: GeomPoint X=318.073 Y=-87.7794 Z=0
    g272: LineSegment StartX=362.567 StartY=-89.8542 StartZ=0 EndX=321.579 EndY=-67.3492 EndZ=0
    g273: LineSegment StartX=318.073 StartY=-69.424 StartZ=0 EndX=318.073 EndY=-87.7794 EndZ=0
    g274: LineSegment StartX=322.073 StartY=-91.7794 StartZ=0 EndX=362.073 EndY=-91.7794 EndZ=0
    g275: Circle CenterX=2.07281 CenterY=124.221 CenterZ=0 NormalX=0 NormalY=0 NormalZ=1 AngleXU=0 Radius=1
    g276: Circle CenterX=1.57905 CenterY=122.295 CenterZ=0 NormalX=0 NormalY=0 NormalZ=1 AngleXU=0 Radius=1
    g277: BSplineCurve PolesCount=3 KnotsCount=2 Degree=2 IsPeriodic=0
    g278: GeomPoint X=2.07281 Y=124.221 Z=0
    g279: GeomPoint X=1.57905 Y=122.295 Z=0
    g280: Circle CenterX=42.0728 CenterY=124.221 CenterZ=0 NormalX=0 NormalY=0 NormalZ=1 AngleXU=0 Radius=1
    g281: Circle CenterX=46.0728 CenterY=124.221 CenterZ=0 NormalX=0 NormalY=0 NormalZ=1 AngleXU=0 Radius=1
    g282: Circle CenterX=46.0728 CenterY=120.221 CenterZ=0 NormalX=0 NormalY=0 NormalZ=1 AngleXU=0 Radius=1
    g283: BSplineCurve PolesCount=3 KnotsCount=2 Degree=2 IsPeriodic=0
    g284: GeomPoint X=42.0728 Y=124.221 Z=0
    g285: GeomPoint X=46.0728 Y=120.221 Z=0
    g286: Circle CenterX=46.0728 CenterY=109.865 CenterZ=0 NormalX=0 NormalY=0 NormalZ=1 AngleXU=0 Radius=1
    g287: Circle CenterX=46.0728 CenterY=105.865 CenterZ=0 NormalX=0 NormalY=0 NormalZ=1 AngleXU=0 Radius=1
    g288: Circle CenterX=42.0728 CenterY=105.865 CenterZ=0 NormalX=0 NormalY=0 NormalZ=1 AngleXU=0 Radius=1
    g289: BSplineCurve PolesCount=3 KnotsCount=2 Degree=2 IsPeriodic=0
    g290: GeomPoint X=46.0728 Y=109.865 Z=0
    g291: GeomPoint X=42.0728 Y=105.865 Z=0
    g292: Circle CenterX=35.5028 CenterY=105.865 CenterZ=0 NormalX=0 NormalY=0 NormalZ=1 AngleXU=0 Radius=1
    g293: Circle CenterX=31.5028 CenterY=105.865 CenterZ=0 NormalX=0 NormalY=0 NormalZ=1 AngleXU=0 Radius=1
    g294: Circle CenterX=27.9965 CenterY=107.79 CenterZ=0 NormalX=0 NormalY=0 NormalZ=1 AngleXU=0 Radius=1
    g295: BSplineCurve PolesCount=3 KnotsCount=2 Degree=2 IsPeriodic=0
    g296: GeomPoint X=35.5028 Y=105.865 Z=0
    g297: GeomPoint X=27.9965 Y=107.79 Z=0
    g298: LineSegment StartX=2.07281 StartY=124.221 StartZ=0 EndX=42.0728 EndY=124.221 EndZ=0
    g299: LineSegment StartX=46.0728 StartY=120.221 StartZ=0 EndX=46.0728 EndY=109.865 EndZ=0
    g300: LineSegment StartX=42.0728 StartY=105.865 StartZ=0 EndX=35.5028 EndY=105.865 EndZ=0
    g301: LineSegment StartX=27.9965 StartY=107.79 StartZ=0 EndX=1.57905 EndY=122.295 EndZ=0
    g302: Circle CenterX=42.5666 CenterY=-67.3492 CenterZ=0 NormalX=0 NormalY=0 NormalZ=1 AngleXU=0 Radius=1
    g303: Circle CenterX=46.0728 CenterY=-65.424 CenterZ=0 NormalX=0 NormalY=0 NormalZ=1 AngleXU=0 Radius=1
    g304: Circle CenterX=46.0728 CenterY=-69.424 CenterZ=0 NormalX=0 NormalY=0 NormalZ=1 AngleXU=0 Radius=1
    g305: BSplineCurve PolesCount=3 KnotsCount=2 Degree=2 IsPeriodic=0
    g306: GeomPoint X=42.5666 Y=-67.3492 Z=0
    g307: GeomPoint X=46.0728 Y=-69.424 Z=0
    g308: Circle CenterX=46.0728 CenterY=-87.7794 CenterZ=0 NormalX=0 NormalY=0 NormalZ=1 AngleXU=0 Radius=1
    g309: Circle CenterX=46.0728 CenterY=-91.7794 CenterZ=0 NormalX=0 NormalY=0 NormalZ=1 AngleXU=0 Radius=1
    g310: Circle CenterX=42.0728 CenterY=-91.7794 CenterZ=0 NormalX=0 NormalY=0 NormalZ=1 AngleXU=0 Radius=1
    g311: BSplineCurve PolesCount=3 KnotsCount=2 Degree=2 IsPeriodic=0
    g312: GeomPoint X=46.0728 Y=-87.7794 Z=0
    g313: GeomPoint X=42.0728 Y=-91.7794 Z=0
    g314: Circle CenterX=2.07281 CenterY=-91.7794 CenterZ=0 NormalX=0 NormalY=0 NormalZ=1 AngleXU=0 Radius=1
    g315: Circle CenterX=-1.92719 CenterY=-91.7794 CenterZ=0 NormalX=0 NormalY=0 NormalZ=1 AngleXU=0 Radius=1
    g316: Circle CenterX=1.57905 CenterY=-89.8542 CenterZ=0 NormalX=0 NormalY=0 NormalZ=1 AngleXU=0 Radius=1
    g317: BSplineCurve PolesCount=3 KnotsCount=2 Degree=2 IsPeriodic=0
    g318: GeomPoint X=2.07281 Y=-91.7794 Z=0
    g319: GeomPoint X=1.57905 Y=-89.8542 Z=0
    g320: LineSegment StartX=2.07281 StartY=-91.7794 StartZ=0 EndX=42.0728 EndY=-91.7794 EndZ=0
    g321: LineSegment StartX=46.0728 StartY=-87.7794 StartZ=0 EndX=46.0728 EndY=-69.424 EndZ=0
    g322: LineSegment StartX=42.5666 StartY=-67.3492 StartZ=0 EndX=1.57905 EndY=-89.8542 EndZ=0
    g323: Circle CenterX=322.073 CenterY=76.4095 CenterZ=0 NormalX=0 NormalY=0 NormalZ=1 AngleXU=0 Radius=4
    g324: BSplineCurve PolesCount=3 KnotsCount=2 Degree=2 IsPeriodic=0
    g325: GeomPoint X=318.073 Y=72.4095 Z=0
    g326: GeomPoint X=322.073 Y=76.4095 Z=0
    g327: Circle CenterX=375.073 CenterY=72.4095 CenterZ=0 NormalX=0 NormalY=0 NormalZ=1 AngleXU=0 Radius=1
    g328: Circle CenterX=375.073 CenterY=76.4095 CenterZ=0 NormalX=0 NormalY=0 NormalZ=1 AngleXU=0 Radius=1
    g329: Circle CenterX=371.073 CenterY=76.4095 CenterZ=0 NormalX=0 NormalY=0 NormalZ=1 AngleXU=0 Radius=1
    g330: BSplineCurve PolesCount=3 KnotsCount=2 Degree=2 IsPeriodic=0
    g331: GeomPoint X=375.073 Y=72.4095 Z=0
    g332: GeomPoint X=371.073 Y=76.4095 Z=0
    g333: LineSegment StartX=322.073 StartY=76.4095 StartZ=0 EndX=371.073 EndY=76.4095 EndZ=0
    g334: LineSegment StartX=318.073 StartY=72.4095 StartZ=0 EndX=318.073 EndY=-47.4805 EndZ=0
    g335: LineSegment StartX=375.073 StartY=72.4095 StartZ=0 EndX=375.073 EndY=-78.7896 EndZ=0
    g336: ArcOfCircle CenterX=-26.9272 CenterY=22.1087 CenterZ=0 NormalX=0 NormalY=0 NormalZ=1 AngleXU=0 Radius=4 StartAngle=5e-16 EndAngle=3.14159
    g337: LineSegment StartX=-22.9272 StartY=22.1087 StartZ=0 EndX=-18.9272 EndY=-83.7794 EndZ=0
    g338: LineSegment StartX=-34.9272 StartY=-83.7794 StartZ=0 EndX=-30.9272 EndY=22.1087 EndZ=0
    g339: ArcOfCircle CenterX=391.073 CenterY=22.1087 CenterZ=0 NormalX=0 NormalY=0 NormalZ=1 AngleXU=0 Radius=4 StartAngle=0 EndAngle=3.14159
    g340: LineSegment StartX=387.073 StartY=22.1087 StartZ=0 EndX=383.073 EndY=-83.7794 EndZ=0
    g341: LineSegment StartX=395.073 StartY=22.1087 StartZ=0 EndX=399.073 EndY=-83.7794 EndZ=0
    g342: Circle CenterX=-10.9272 CenterY=-78.7794 CenterZ=0 NormalX=0 NormalY=0 NormalZ=1 AngleXU=0 Radius=1
    g343: Circle CenterX=-10.9272 CenterY=-82.7794 CenterZ=0 NormalX=0 NormalY=0 NormalZ=1 AngleXU=0 Radius=1
    g344: Circle CenterX=-7.42095 CenterY=-80.8542 CenterZ=0 NormalX=0 NormalY=0 NormalZ=1 AngleXU=0 Radius=1
    g345: BSplineCurve PolesCount=3 KnotsCount=2 Degree=2 IsPeriodic=0
    g346: GeomPoint X=-10.9272 Y=-78.7794 Z=0
    g347: GeomPoint X=-7.42095 Y=-80.8542 Z=0
    g348: Circle CenterX=42.5666 CenterY=-53.4075 CenterZ=0 NormalX=0 NormalY=0 NormalZ=1 AngleXU=0 Radius=1
    g349: Circle CenterX=46.0728 CenterY=-51.4823 CenterZ=0 NormalX=0 NormalY=0 NormalZ=1 AngleXU=0 Radius=1
    g350: Circle CenterX=46.0728 CenterY=-47.4823 CenterZ=0 NormalX=0 NormalY=0 NormalZ=1 AngleXU=0 Radius=1
    g351: BSplineCurve PolesCount=3 KnotsCount=2 Degree=2 IsPeriodic=0
    g352: GeomPoint X=42.5666 Y=-53.4075 Z=0
    g353: GeomPoint X=46.0728 Y=-47.4823 Z=0
    g354: Circle CenterX=46.0728 CenterY=72.4095 CenterZ=0 NormalX=0 NormalY=0 NormalZ=1 AngleXU=0 Radius=1
    g355: Circle CenterX=46.0728 CenterY=76.4095 CenterZ=0 NormalX=0 NormalY=0 NormalZ=1 AngleXU=0 Radius=1
    g356: Circle CenterX=42.0728 CenterY=76.4095 CenterZ=0 NormalX=0 NormalY=0 NormalZ=1 AngleXU=0 Radius=1
    g357: BSplineCurve PolesCount=3 KnotsCount=2 Degree=2 IsPeriodic=0
    g358: GeomPoint X=46.0728 Y=72.4095 Z=0
    g359: GeomPoint X=42.0728 Y=76.4095 Z=0
    g360: Circle CenterX=-6.92719 CenterY=76.4095 CenterZ=0 NormalX=0 NormalY=0 NormalZ=1 AngleXU=0 Radius=1
    g361: Circle CenterX=-10.9272 CenterY=76.4095 CenterZ=0 NormalX=0 NormalY=0 NormalZ=1 AngleXU=0 Radius=1
    g362: Circle CenterX=-10.9272 CenterY=72.4095 CenterZ=0 NormalX=0 NormalY=0 NormalZ=1 AngleXU=0 Radius=1
    g363: BSplineCurve PolesCount=3 KnotsCount=2 Degree=2 IsPeriodic=0
    g364: GeomPoint X=-6.92719 Y=76.4095 Z=0
    g365: GeomPoint X=-10.9272 Y=72.4095 Z=0
    g366: LineSegment StartX=-10.9272 StartY=72.4095 StartZ=0 EndX=-10.9272 EndY=-78.7794 EndZ=0
    g367: LineSegment StartX=-7.42095 StartY=-80.8542 StartZ=0 EndX=42.5666 EndY=-53.4075 EndZ=0
    g368: LineSegment StartX=46.0728 StartY=-47.4823 StartZ=0 EndX=46.0728 EndY=72.4095 EndZ=0
    g369: LineSegment StartX=42.0728 StartY=76.4095 StartZ=0 EndX=-6.92719 EndY=76.4095 EndZ=0
    g370: LineSegment StartX=-42.9272 StartY=136.221 StartZ=0 EndX=407.073 EndY=136.221 EndZ=0
    g371: LineSegment StartX=232.072 StartY=136.221 StartZ=0 EndX=220.072 EndY=136.221 EndZ=0
    g372: LineSegment StartX=232.072 StartY=136.221 StartZ=0 EndX=232.072 EndY=124.221 EndZ=0
    g373: LineSegment StartX=220.072 StartY=136.221 StartZ=0 EndX=220.072 EndY=124.221 EndZ=0
    g374: LineSegment StartX=220.072 StartY=136.221 StartZ=0 EndX=226.072 EndY=136.221 EndZ=0
    g375: LineSegment StartX=220.072 StartY=136.221 StartZ=0 EndX=220.072 EndY=130.221 EndZ=0
    g376: LineSegment StartX=220.072 StartY=124.221 StartZ=0 EndX=226.072 EndY=124.221 EndZ=0
    g377: LineSegment StartX=232.072 StartY=124.221 StartZ=0 EndX=232.072 EndY=127.221 EndZ=0
    g378: LineSegment StartX=232.072 StartY=136.221 StartZ=0 EndX=232.072 EndY=133.221 EndZ=0
    g379-g383: Circle x5 (B-spline internal-alignment scaffolding for g384; pole/knot coordinates omitted)
    g384: BSplineCurve PolesCount=5 KnotsCount=3 Degree=3 IsPeriodic=0
    g385: GeomPoint X=232.072 Y=133.221 Z=0
    g386: GeomPoint X=223.072 Y=130.221 Z=0
    g387: GeomPoint X=232.072 Y=127.221 Z=0
    g388: LineSegment StartX=189.124 StartY=124.221 StartZ=0 EndX=302.073 EndY=124.221 EndZ=0
    g389: LineSegment StartX=132.072 StartY=136.221 StartZ=0 EndX=132.072 EndY=124.221 EndZ=0
    g390: LineSegment StartX=132.072 StartY=136.221 StartZ=0 EndX=144.072 EndY=136.221 EndZ=0
    g391: LineSegment StartX=144.072 StartY=136.221 StartZ=0 EndX=144.072 EndY=124.221 EndZ=0
    g392: LineSegment StartX=144.072 StartY=136.221 StartZ=0 EndX=138.072 EndY=136.221 EndZ=0
    g393: LineSegment StartX=144.072 StartY=136.221 StartZ=0 EndX=144.072 EndY=130.221 EndZ=0
    g394: LineSegment StartX=132.072 StartY=136.221 StartZ=0 EndX=132.072 EndY=133.221 EndZ=0
    g395: LineSegment StartX=132.072 StartY=133.221 StartZ=0 EndX=132.072 EndY=127.221 EndZ=0
    g396-g400: Circle x5 (B-spline internal-alignment scaffolding for g401; pole/knot coordinates omitted)
    g401: BSplineCurve PolesCount=5 KnotsCount=3 Degree=3 IsPeriodic=0
    g402: GeomPoint X=132.072 Y=133.221 Z=0
    g403: GeomPoint X=141.072 Y=130.221 Z=0
    g404: GeomPoint X=132.072 Y=127.221 Z=0
    g405: LineSegment StartX=132.072 StartY=124.221 StartZ=0 EndX=175.022 EndY=124.221 EndZ=0
    g406: LineSegment StartX=62.0728 StartY=124.221 StartZ=0 EndX=132.072 EndY=124.221 EndZ=0
    g407: LineSegment StartX=132.072 StartY=136.221 StartZ=0 EndX=131.457 EndY=138.832 EndZ=0
    ... +61 more geometry lines
  constraints (808):
    c: Vertical(g0)
    c: Vertical(g1)
    c: Block(g1)
    c: Block(g0)
    c: Weight(g4) = 1
    c: Equal(g4,g5)
    c: Equal(g4,g6)
    c: InternalAlignment(g4,g7)
    c: InternalAlignment(g5,g7)
    c: InternalAlignment(g6,g7)
    c: InternalAlignment(g8,g7)
    c: InternalAlignment(g9,g7)
    c: Weight(g10) = 1
    c: Equal(g10,g11)
    c: Equal(g10,g12)
    c: InternalAlignment(g10,g13)
    c: InternalAlignment(g11,g13)
    c: InternalAlignment(g12,g13)
    c: InternalAlignment(g14,g13)
    c: InternalAlignment(g15,g13)
    c: Block(g13)
    c: Block(g7)
    c: Weight(g16) = 1
    c: Equal(g16,g17)
    c: Equal(g16,g18)
    c: InternalAlignment(g16,g19)
    c: InternalAlignment(g17,g19)
    c: InternalAlignment(g18,g19)
    c: InternalAlignment(g20,g19)
    c: InternalAlignment(g21,g19)
    c: Weight(g22) = 1
    c: Equal(g22,g23)
    c: Equal(g22,g24)
    c: InternalAlignment(g22,g25)
    c: InternalAlignment(g23,g25)
    c: InternalAlignment(g24,g25)
    c: InternalAlignment(g26,g25)
    c: InternalAlignment(g27,g25)
    c: Block(g25)
    c: Block(g19)
    c: Weight(g28) = 1
    c: Equal(g28,g29)
    c: Equal(g28,g30)
    c: InternalAlignment(g28,g31)
    c: InternalAlignment(g29,g31)
    c: InternalAlignment(g30,g31)
    c: InternalAlignment(g32,g31)
    c: InternalAlignment(g33,g31)
    c: Weight(g34) = 1
    c: Equal(g34,g35)
    c: Equal(g34,g36)
    c: InternalAlignment(g34,g37)
    c: InternalAlignment(g35,g37)
    c: InternalAlignment(g36,g37)
    c: InternalAlignment(g38,g37)
    c: InternalAlignment(g39,g37)
    c: Block(g31)
    c: Block(g37)
    c: Coincident(g40,g1)
    c: Coincident(g40,g0)
    c: Horizontal(g40)
    c: Distance(g40) = 450
    c: Weight(g41) = 1
    c: Equal(g41,g42)
    c: Equal(g41,g43)
    c: InternalAlignment(g41,g44)
    c: InternalAlignment(g42,g44)
    c: InternalAlignment(g43,g44)
    c: InternalAlignment(g45,g44)
    c: InternalAlignment(g46,g44)
    c: Block(g44)
    c: Weight(g47) = 1
    c: Equal(g47,g48)
    c: Equal(g47,g49)
    c: InternalAlignment(g47,g50)
    c: InternalAlignment(g48,g50)
    c: InternalAlignment(g49,g50)
    c: InternalAlignment(g51,g50)
    c: InternalAlignment(g52,g50)
    c: Block(g50)
    c: Weight(g53) = 1
    c: Equal(g53,g54)
    c: Equal(g53,g55)
    c: InternalAlignment(g53,g56)
    c: InternalAlignment(g54,g56)
    c: InternalAlignment(g55,g56)
    c: InternalAlignment(g57,g56)
    c: InternalAlignment(g58,g56)
    c: Block(g56)
    c: Weight(g59) = 1
    c: Equal(g59,g60)
    c: Equal(g59,g61)
    c: InternalAlignment(g59,g62)
    c: InternalAlignment(g60,g62)
    c: InternalAlignment(g61,g62)
    c: InternalAlignment(g63,g62)
    c: InternalAlignment(g64,g62)
    c: Block(g62)
    c: Weight(g65) = 1
    c: Equal(g65,g66)
    c: Equal(g65,g67)
    c: InternalAlignment(g65,g68)
    c: InternalAlignment(g66,g68)
    c: InternalAlignment(g67,g68)
    c: InternalAlignment(g69,g68)
    c: InternalAlignment(g70,g68)
    c: Weight(g71) = 1
    c: Equal(g71,g72)
    c: Equal(g71,g73)
    c: InternalAlignment(g71,g74)
    c: InternalAlignment(g72,g74)
    c: InternalAlignment(g73,g74)
    c: InternalAlignment(g75,g74)
    c: InternalAlignment(g76,g74)
    c: Block(g68)
    c: Block(g74)
    c: Coincident(g77,g68)
    c: Coincident(g77,g74)
    c: Vertical(g77)
    c: Coincident(g78,g68)
    c: Coincident(g78,g50)
    c: Coincident(g79,g50)
    c: Coincident(g79,g74)
    c: Weight(g80) = 1
    c: Equal(g80,g81)
    c: Equal(g80,g82)
    c: InternalAlignment(g80,g83)
    c: InternalAlignment(g81,g83)
    c: InternalAlignment(g82,g83)
    c: InternalAlignment(g84,g83)
    c: InternalAlignment(g85,g83)
    c: Weight(g86) = 1
    c: Equal(g86,g87)
    c: Equal(g86,g88)
    c: InternalAlignment(g86,g89)
    c: InternalAlignment(g87,g89)
    c: InternalAlignment(g88,g89)
    c: InternalAlignment(g90,g89)
    c: InternalAlignment(g91,g89)
    c: Block(g83)
    c: Block(g89)
    c: Coincident(g92,g83)
    c: Coincident(g92,g89)
    c: Vertical(g92)
    c: Coincident(g93,g83)
    c: Coincident(g93,g44)
    c: Coincident(g94,g44)
    c: Coincident(g94,g89)
    c: Weight(g95) = 1
    c: Equal(g95,g96)
    c: Equal(g95,g97)
    c: InternalAlignment(g95,g98)
    c: InternalAlignment(g96,g98)
    c: InternalAlignment(g97,g98)
    c: InternalAlignment(g99,g98)
    c: InternalAlignment(g100,g98)
    c: Weight(g101) = 1
    c: Equal(g101,g102)
    c: Equal(g101,g103)
    c: InternalAlignment(g101,g104)
    c: InternalAlignment(g102,g104)
    c: InternalAlignment(g103,g104)
    c: InternalAlignment(g105,g104)
    c: InternalAlignment(g106,g104)
    c: Block(g98)
    c: Block(g104)
    c: Coincident(g107,g98)
    c: Coincident(g107,g104)
    c: Vertical(g107)
    c: Coincident(g108,g104)
    c: Coincident(g108,g62)
    c: Coincident(g109,g62)
    c: Coincident(g109,g98)
    c: Weight(g110) = 1
    c: Equal(g110,g111)
    c: Equal(g110,g112)
    c: InternalAlignment(g110,g113)
    c: InternalAlignment(g111,g113)
    c: InternalAlignment(g112,g113)
    c: InternalAlignment(g114,g113)
    c: InternalAlignment(g115,g113)
    c: Weight(g116) = 1
    c: Equal(g116,g117)
    c: Equal(g116,g118)
    c: InternalAlignment(g116,g119)
    c: InternalAlignment(g117,g119)
    c: InternalAlignment(g118,g119)
    c: InternalAlignment(g120,g119)
    c: InternalAlignment(g121,g119)
    c: Block(g113)
    c: Block(g119)
    c: Coincident(g122,g113)
    c: Coincident(g122,g119)
    c: Vertical(g122)
    c: Coincident(g123,g119)
    c: Coincident(g123,g56)
    c: Coincident(g124,g56)
    c: Coincident(g124,g113)
    c: Weight(g125) = 1
    c: Equal(g125,g126)
    c: Equal(g125,g127)
    c: InternalAlignment(g125,g128)
    c: InternalAlignment(g126,g128)
    c: InternalAlignment(g127,g128)
    c: InternalAlignment(g129,g128)
    c: InternalAlignment(g130,g128)
    c: Weight(g131) = 1
    c: Equal(g131,g132)
    c: Equal(g131,g133)
    c: InternalAlignment(g131,g134)
    c: InternalAlignment(g132,g134)
    c: InternalAlignment(g133,g134)
    c: InternalAlignment(g135,g134)
    c: InternalAlignment(g136,g134)
    c: Weight(g137) = 1
    c: Equal(g137,g138)
    c: Equal(g137,g139)
    c: InternalAlignment(g137,g140)
    c: InternalAlignment(g138,g140)
    c: InternalAlignment(g139,g140)
    c: InternalAlignment(g141,g140)
    c: InternalAlignment(g142,g140)
    c: Weight(g143) = 1
    c: Equal(g143,g144)
    c: Equal(g143,g145)
    c: InternalAlignment(g143,g146)
    c: InternalAlignment(g144,g146)
    c: InternalAlignment(g145,g146)
    c: InternalAlignment(g147,g146)
    c: InternalAlignment(g148,g146)
    c: Block(g146)
    c: Block(g140)
    c: Block(g134)
    c: Block(g128)
    c: Coincident(g149,g25)
    c: Coincident(g149,g146)
    c: Coincident(g150,g146)
    c: Coincident(g150,g140)
    c: Horizontal(g150)
    c: Coincident(g151,g140)
    c: Coincident(g151,g25)
    c: Vertical(g151)
    c: Coincident(g152,g19)
    c: Coincident(g152,g134)
    c: Vertical(g152)
    c: Coincident(g153,g134)
    c: Coincident(g153,g128)
    c: Horizontal(g153)
    c: Coincident(g154,g128)
    c: Coincident(g154,g19)
    c: Weight(g155) = 1
    c: Equal(g155,g156)
    c: Equal(g155,g157)
    c: InternalAlignment(g155,g158)
    c: InternalAlignment(g156,g158)
    c: InternalAlignment(g157,g158)
    c: InternalAlignment(g159,g158)
    c: InternalAlignment(g160,g158)
    c: Weight(g161) = 1
    c: Equal(g161,g162)
    c: Equal(g161,g163)
    c: InternalAlignment(g161,g164)
    c: InternalAlignment(g162,g164)
    c: InternalAlignment(g163,g164)
    c: InternalAlignment(g165,g164)
    c: InternalAlignment(g166,g164)
    c: Weight(g167) = 1
    c: Equal(g167,g168)
    c: Equal(g167,g169)
    c: InternalAlignment(g167,g170)
    c: InternalAlignment(g168,g170)
    c: InternalAlignment(g169,g170)
    c: InternalAlignment(g171,g170)
    c: InternalAlignment(g172,g170)
    c: Weight(g173) = 1
    c: Equal(g173,g174)
    c: Equal(g173,g175)
    c: InternalAlignment(g173,g176)
    c: InternalAlignment(g174,g176)
    c: InternalAlignment(g175,g176)
    c: InternalAlignment(g177,g176)
    c: InternalAlignment(g178,g176)
    c: Block(g176)
    c: Block(g170)
    c: Block(g164)
    c: Block(g158)
    c: Coincident(g179,g170)
    c: Coincident(g179,g7)
    c: Vertical(g179)
    c: Coincident(g180,g13)
    c: Coincident(g180,g164)
    c: Vertical(g180)
    c: Coincident(g181,g158)
    c: Coincident(g181,g13)
    c: Coincident(g182,g7)
    c: Weight(g183) = 1
    c: Equal(g183,g184)
    c: Equal(g183,g185)
    c: InternalAlignment(g183,g186)
    c: InternalAlignment(g184,g186)
    c: InternalAlignment(g185,g186)
    c: InternalAlignment(g187,g186)
    c: InternalAlignment(g188,g186)
    c: Weight(g189) = 1
    c: Equal(g189,g190)
    c: Equal(g189,g191)
    c: InternalAlignment(g189,g192)
    c: InternalAlignment(g190,g192)
    c: InternalAlignment(g191,g192)
    c: InternalAlignment(g193,g192)
    c: InternalAlignment(g194,g192)
    c: Block(g192)
    c: Block(g186)
    c: Coincident(g195,g192)
    c: Coincident(g195,g31)
    c: Coincident(g196,g31)
    c: Coincident(g196,g186)
    c: Coincident(g197,g186)
    c: Coincident(g197,g192)
    c: Vertical(g197)
    c: Weight(g198) = 1
    c: Equal(g198,g199)
    c: Equal(g198,g200)
    c: InternalAlignment(g198,g201)
    c: InternalAlignment(g199,g201)
    c: InternalAlignment(g200,g201)
    c: InternalAlignment(g202,g201)
    c: InternalAlignment(g203,g201)
    c: Weight(g204) = 1
    c: Equal(g204,g205)
    c: Equal(g204,g206)
    c: InternalAlignment(g204,g207)
    c: InternalAlignment(g205,g207)
    c: InternalAlignment(g206,g207)
    c: InternalAlignment(g208,g207)
    c: InternalAlignment(g209,g207)
    c: Block(g207)
    c: Block(g201)
    c: Coincident(g210,g201)
    c: Coincident(g210,g37)
    c: Coincident(g211,g37)
    c: Coincident(g211,g207)
    c: Coincident(g212,g207)
    c: Coincident(g212,g201)
    c: Vertical(g212)
    c: Horizontal(g213)
    c: Block(g213)
    c: Vertical(g214)
    c: Block(g214)
    c: Block(g215)
    c: Weight(g216) = 1
    c: Equal(g216,g217)
    c: Equal(g216,g218)
    c: InternalAlignment(g216,g219)
    c: InternalAlignment(g217,g219)
    c: InternalAlignment(g218,g219)
    c: InternalAlignment(g220,g219)
    c: InternalAlignment(g221,g219)
    c: Weight(g222) = 1
    c: Equal(g222,g223)
    c: Equal(g222,g224)
    c: InternalAlignment(g222,g225)
    c: InternalAlignment(g223,g225)
    c: InternalAlignment(g224,g225)
    c: InternalAlignment(g226,g225)
    c: InternalAlignment(g227,g225)
    c: Weight(g228) = 1
    c: Equal(g228,g229)
    c: Equal(g228,g230)
    c: InternalAlignment(g228,g231)
    c: InternalAlignment(g229,g231)
    c: InternalAlignment(g230,g231)
    c: InternalAlignment(g232,g231)
    c: InternalAlignment(g233,g231)
    c: Weight(g234) = 1
    c: Equal(g234,g235)
    c: Equal(g234,g236)
    c: InternalAlignment(g234,g237)
    c: InternalAlignment(g235,g237)
    c: InternalAlignment(g236,g237)
    c: InternalAlignment(g238,g237)
    c: InternalAlignment(g239,g237)
    c: Block(g219)
    c: Block(g225)
    c: Block(g231)
    c: Block(g237)
    c: Coincident(g240,g225)
    c: Coincident(g240,g219)
    c: Horizontal(g240)
    c: Block(g182)
    c: Weight(g241) = 1
    c: Equal(g241,g242)
    c: Equal(g241,g243)
    c: InternalAlignment(g241,g244)
    c: InternalAlignment(g242,g244)
    c: InternalAlignment(g243,g244)
    c: InternalAlignment(g245,g244)
    c: InternalAlignment(g246,g244)
    c: Weight(g247) = 1
    c: Equal(g247,g248)
    c: Equal(g247,g249)
    c: InternalAlignment(g247,g250)
    c: InternalAlignment(g248,g250)
    c: InternalAlignment(g249,g250)
    c: InternalAlignment(g251,g250)
    c: InternalAlignment(g252,g250)
    c: Block(g244)
    c: Block(g250)
    c: Coincident(g253,g244)
    c: Coincident(g253,g250)
    c: Weight(g254) = 1
    c: Equal(g254,g255)
    c: Equal(g254,g256)
    c: InternalAlignment(g254,g257)
    c: InternalAlignment(g255,g257)
    c: InternalAlignment(g256,g257)
    c: InternalAlignment(g258,g257)
    c: InternalAlignment(g259,g257)
    c: Weight(g260) = 1
    c: Equal(g260,g261)
    c: Equal(g260,g262)
    c: InternalAlignment(g260,g263)
    c: InternalAlignment(g261,g263)
    c: InternalAlignment(g262,g263)
    c: InternalAlignment(g264,g263)
    c: InternalAlignment(g265,g263)
    c: Weight(g266) = 1
    c: Equal(g266,g267)
    c: Equal(g266,g268)
    c: InternalAlignment(g266,g269)
    c: InternalAlignment(g267,g269)
    c: InternalAlignment(g268,g269)
    c: InternalAlignment(g270,g269)
    c: InternalAlignment(g271,g269)
    c: Block(g269)
    c: Block(g263)
    c: Block(g257)
    c: Coincident(g272,g263)
    c: Coincident(g272,g257)
    c: Coincident(g273,g257)
    c: Coincident(g273,g269)
    c: Vertical(g273)
    c: Coincident(g274,g269)
    c: Coincident(g274,g263)
    c: Horizontal(g274)
    c: Weight(g275) = 1
    c: Equal(g275,g276)
    c: InternalAlignment(g275,g277)
    c: InternalAlignment(g276,g277)
    c: InternalAlignment(g278,g277)
    c: InternalAlignment(g279,g277)
    c: Weight(g280) = 1
    c: InternalAlignment(g281,g283)
    c: InternalAlignment(g282,g283)
    c: InternalAlignment(g284,g283)
    c: InternalAlignment(g285,g283)
    c: Weight(g286) = 1
    c: Equal(g286,g287)
    c: Equal(g286,g288)
    c: InternalAlignment(g286,g289)
    c: InternalAlignment(g287,g289)
    c: InternalAlignment(g288,g289)
    c: InternalAlignment(g290,g289)
    c: InternalAlignment(g291,g289)
    c: Equal(g292,g293)
    c: Equal(g292,g294)
    c: InternalAlignment(g292,g295)
    c: InternalAlignment(g293,g295)
    c: InternalAlignment(g294,g295)
    c: InternalAlignment(g296,g295)
    c: InternalAlignment(g297,g295)
    c: Block(g283)
    c: Block(g289)
    c: Block(g295)
    c: Block(g277)
    c: Coincident(g298,g277)
    c: Coincident(g298,g283)
    c: Horizontal(g298)
    c: Coincident(g299,g283)
    c: Coincident(g299,g289)
    c: Vertical(g299)
    c: Coincident(g300,g289)
    c: Coincident(g300,g295)
    c: Horizontal(g300)
    c: Coincident(g301,g295)
    c: Coincident(g301,g277)
    c: Weight(g302) = 1
    c: Equal(g302,g303)
    c: Equal(g302,g304)
    c: InternalAlignment(g302,g305)
    c: InternalAlignment(g303,g305)
    c: InternalAlignment(g304,g305)
    c: InternalAlignment(g306,g305)
    c: InternalAlignment(g307,g305)
    c: Weight(g308) = 1
    c: Equal(g308,g309)
    c: Equal(g308,g310)
    c: InternalAlignment(g308,g311)
    c: InternalAlignment(g309,g311)
    c: InternalAlignment(g310,g311)
    c: InternalAlignment(g312,g311)
    c: Weight(g314) = 1
    c: Equal(g314,g315)
    c: Equal(g314,g316)
    c: InternalAlignment(g314,g317)
    c: InternalAlignment(g315,g317)
    c: InternalAlignment(g316,g317)
    c: InternalAlignment(g318,g317)
    c: InternalAlignment(g319,g317)
    c: Block(g317)
    c: Block(g311)
    c: Block(g305)
    c: Coincident(g320,g317)
    c: Coincident(g320,g311)
    c: Horizontal(g320)
    c: Coincident(g321,g311)
    c: Coincident(g321,g305)
    c: Vertical(g321)
    c: Coincident(g322,g305)
    c: Coincident(g322,g317)
    c: InternalAlignment(g323,g324)
    c: InternalAlignment(g325,g324)
    c: InternalAlignment(g326,g324)
    c: Block(g324)
    c: Equal(g327,g328)
    c: Equal(g327,g329)
    c: InternalAlignment(g327,g330)
    c: InternalAlignment(g328,g330)
    c: InternalAlignment(g329,g330)
    c: InternalAlignment(g331,g330)
    c: InternalAlignment(g332,g330)
    c: Block(g330)
    c: Coincident(g333,g324)
    c: Horizontal(g333)
    c: Block(g333)
    c: Coincident(g334,g324)
    c: Coincident(g334,g250)
    c: Vertical(g334)
    c: Coincident(g335,g330)
    c: Coincident(g335,g244)
    c: Vertical(g335)
    c: Block(g336)
    c: Block(g2)
    c: Distance(g334) = 119.89
    c: Coincident(g337,g336)
    c: Coincident(g337,g2)
    c: Coincident(g338,g2)
    c: Coincident(g338,g336)
    c: Block(g3)
    c: Block(g339)
    c: Coincident(g340,g339)
    c: Coincident(g340,g3)
    c: Coincident(g341,g339)
    c: Coincident(g341,g3)
    c: Block(g341)
    c: Block(g340)
    c: Weight(g342) = 1
    c: Equal(g342,g344)
    c: InternalAlignment(g342,g345)
    c: InternalAlignment(g343,g345)
    c: InternalAlignment(g344,g345)
    c: InternalAlignment(g346,g345)
    c: InternalAlignment(g347,g345)
    c: InternalAlignment(g352,g351)
    c: InternalAlignment(g353,g351)
    c: InternalAlignment(g355,g357)
    c: Horizontal(g369)
    c: Coincident(g370,g0)
    c: Horizontal(g370)
    c: Block(g370)
    c: Distance(g370) = 450
    c: Horizontal(g371)
    c: Distance(g371) = 12
    c: Coincident(g373,g371)
    c: Vertical(g373)
    c: Horizontal(g374)
    c: Vertical(g375)
    c: Distance(g375) = 6
    c: Coincident(g375,g371)
    c: Coincident(g374,g371)
    c: Block(g373)
    c: Coincident(g376,g373)
    c: Horizontal(g376)
    c: Distance(g376) = 6
    c: Vertical(g377)
    c: Distance(g377) = 3
    c: Vertical(g378)
    c: Distance(g378) = 3
    c: Coincident(g372,g377)
    c: Coincident(g384,g378)
    c: Weight(g379) = 1
    c: Equal(g379,g380)
    c: Coincident(g380,g374)
    c: Equal(g379,g381)
    c: Coincident(g381,g375)
    c: Equal(g379,g382)
    c: Coincident(g382,g376)
    c: Equal(g379,g383)
    c: Coincident(g384,g377)
    c: InternalAlignment(g379-g383 -> g384) x5
    c: InternalAlignment(g385,g384)
    c: InternalAlignment(g386,g384)
    c: InternalAlignment(g387,g384)
    c: Coincident(g388,g164)
    c: Coincident(g388,g158)
    c: Coincident(g392,g390)
    c: Vertical(g393)
    c: Distance(g393) = 6
    c: Coincident(g393,g390)
    c: Vertical(g394)
    c: Distance(g394) = 3
    c: Vertical(g395)
    c: Distance(g395) = 6
    c: Coincident(g395,g394)
    c: Coincident(g401,g394)
    c: Weight(g396) = 1
    c: Equal(g396,g397)
    c: Coincident(g397,g392)
    c: Equal(g396,g398)
    c: Coincident(g398,g393)
    c: Equal(g396,g399)
    c: Equal(g396,g400)
    c: Coincident(g401,g395)
    c: InternalAlignment(g396-g400 -> g401) x5
    c: InternalAlignment(g402,g401)
    c: InternalAlignment(g403,g401)
    c: InternalAlignment(g404,g401)
    c: Coincident(g405,g389)
    c: Coincident(g405,g170)
    c: Horizontal(g405)
    c: Block(g401)
    c: Coincident(g406,g176)
    c: Coincident(g406,g389)
    c: Horizontal(g406)
    c: Block(g405)
    c: Coincident(g408,g389)
    c: PointOnObject(g408,g153)
    c: Vertical(g408)
    c: Block(g409)
    c: Coincident(g410,g409)
    c: Vertical(g410)
    c: PointOnObject(g410,g40)
    c: Block(g410)
    c: Coincident(g411,g409)
    c: Vertical(g411)
    c: Block(g411)
    c: Vertical(g412)
    c: Distance(g412) = 3
    c: Equal(g379,g415) = 1
    c: Equal(g415,g416)
    c: InternalAlignment(g415,g417)
    c: InternalAlignment(g416,g417)
    c: InternalAlignment(g413,g417)
    c: InternalAlignment(g414,g417)
    c: InternalAlignment(g418,g417)
    c: Block(g417)
    c: Coincident(g418,g412)
    c: Coincident(g419,g417)
    c: PointOnObject(g419,g150)
    c: Vertical(g419)
    c: Distance(g420) = 3
    c: Block(g420)
    c: Distance(g421) = 3
    c: Parallel(g421,g420)
    c: Coincident(g421,g420)
    c: Coincident(g422,g420)
    c: Perpendicular(g422,g420)
    c: Distance(g422) = 3
    c: Coincident(g423,g421)
    c: Perpendicular(g423,g421)
    c: Distance(g423) = 3
    c: Coincident(g424,g420)
    c: Perpendicular(g424,g421)
    c: Distance(g424) = 6
    c: Coincident(g425,g424)
    c: PointOnObject(g423,g425)
    c: Coincident(g426,g420)
    c: PointOnObject(g426,g79)
    c: Block(g426)
    c: Distance(g427) = 2.76
    c: Coincident(g428,g427)
    c: Parallel(g427,g428)
    c: PointOnObject(g428,g181)
    c: Distance(g428) = 2.41
    c: Block(g428)
    c: Coincident(g429,g427)
    c: Distance(g429) = 6.6
    c: Perpendicular(g429,g428)
    c: Distance(g430) = 6.6
    c: Coincident(g431,g429)
    c: Coincident(g431,g430)
    c: Block(g432)
    c: Coincident(g433,g432)
    c: Vertical(g433)
    c: Distance(g433) = 3.6
    c: Coincident(g434,g427)
    c: Parallel(g427,g434)
    c: PointOnObject(g434,g78)
    c: Block(g434)
    c: Coincident(g435,g421)
    c: Parallel(g435,g421)
    c: PointOnObject(g435,g211)
    c: Block(g435)
    c: Coincident(g436,g435)
    c: Vertical(g436)
    c: PointOnObject(g436,g210)
    c: Coincident(g437,g436)
    c: Perpendicular(g437,g210)
    c: Distance(g437) = 3
    c: Coincident(g438,g437)
    c: Block(g437)
    c: Distance(g438) = 3
    c: Parallel(g437,g438)
    c: Coincident(g439,g438)
    c: Distance(g439) = 3
    c: Parallel(g438,g439)
    c: Coincident(g440,g439)
    c: Parallel(g440,g437)
    c: PointOnObject(g440,g124)
    c: PointOnObject(g441,g53)
    c: Tangent(g440,g441)
    c: Coincident(g442,g439)
    c: Perpendicular(g442,g439)
    c: Coincident(g443,g437)
    c: Parallel(g443,g442)
    c: Distance(g443) = 3
    c: Distance(g442) = 3
    c: PointOnObject(g442,g444)
    c: Block(g444)
    c: PointOnObject(g445,g123)
    c: Perpendicular(g123,g445)
    c: Distance(g445) = 2.41
    c: Block(g445)
    c: Coincident(g446,g445)
    c: Perpendicular(g123,g446)
    c: Distance(g446) = 2.76
    c: Coincident(g447,g446)
    c: Perpendicular(g123,g447)
    c: PointOnObject(g447,g149)
    c: Coincident(g448,g445)
    c: Parallel(g123,g448)
    c: Distance(g448) = 6.6
    c: Coincident(g449,g446)
    c: Parallel(g123,g449)
    c: Coincident(g450,g448)
    c: Distance(g449) = 6.6
    c: Coincident(g449,g450)
    c: Block(g149)
    c: Block(g124)
    c: Block(g211)
    c: Block(g181)
    c: Block(g78)
    c: Block(g79)
    c: Block(g430)
    c: Coincident(g451,g447)
    c: Distance(g451) = 46
    c: Parallel(g149,g451)
    c: Coincident(g452,g451)
    c: Horizontal(g452)
    c: PointOnObject(g452,g154)
    c: Coincident(g453,g451)
    c: Vertical(g453)
    c: Distance(g453) = 9
    c: Block(g452)
    c: PointOnObject(g454,g93)
    c: Distance(g455) = 6.6
    c: Distance(g456) = 6.6
    c: Block(g454)
    c: Coincident(g457,g456)
    c: Coincident(g457,g455)
    c: Perpendicular(g457,g182)
    c: Coincident(g458,g455)
    c: Perpendicular(g458,g182)
    c: PointOnObject(g458,g182)
    c: Block(g458)
    c: Block(g457)
    c: Block(g456)
    c: PointOnObject(g459,g196)
    c: Perpendicular(g196,g459)
    c: Distance(g459) = 3
    c: Coincident(g460,g459)
    c: Perpendicular(g196,g460)
    c: Distance(g460) = 3
    c: Coincident(g461,g460)
    c: Perpendicular(g196,g461)
    c: Distance(g461) = 3
    c: Coincident(g462,g461)
    c: Tangent(g462,g41)
    c: PointOnObject(g462,g94)
    c: Block(g462)
    c: Block(g459)
    c: Coincident(g463,g459)
    c: Parallel(g196,g463)
    c: Distance(g463) = 3
    c: Coincident(g464,g461)
    c: Distance(g464) = 3
    c: Parallel(g196,g464)
    c: Coincident(g465,g460)
    c: Distance(g465) = 6
    c: Parallel(g465,g196)
    c: Coincident(g466,g465)
    c: PointOnObject(g464,g466)
    c: Block(g466)
    c: Coincident(g467,g458)
    c: Vertical(g467)
    c: PointOnObject(g467,g195)
    c: Coincident(g468,g467)
    c: Perpendicular(g195,g468)
FEATURE [Sketcher::SketchObject] Sketch004  label="rightSideBottom"
  FullyConstrained = false
  sketch-geometry (91):
    g0: ArcOfCircle CenterX=391.073 CenterY=-83.7794 CenterZ=0 NormalX=0 NormalY=0 NormalZ=1 AngleXU=0 Radius=8 StartAngle=3.14159 EndAngle=6.28319
    g1: Circle CenterX=306.073 CenterY=-81.8102 CenterZ=0 NormalX=0 NormalY=0 NormalZ=1 AngleXU=0 Radius=1
    g2: Circle CenterX=306.073 CenterY=-77.8102 CenterZ=0 NormalX=0 NormalY=0 NormalZ=1 AngleXU=0 Radius=1
    g3: Circle CenterX=302.567 CenterY=-42.9683 CenterZ=0 NormalX=0 NormalY=0 NormalZ=1 AngleXU=0 Radius=1
    g4: Circle CenterX=306.073 CenterY=-44.8935 CenterZ=0 NormalX=0 NormalY=0 NormalZ=1 AngleXU=0 Radius=1
    g5: Circle CenterX=306.073 CenterY=-40.8935 CenterZ=0 NormalX=0 NormalY=0 NormalZ=1 AngleXU=0 Radius=1
    g6: BSplineCurve PolesCount=3 KnotsCount=2 Degree=2 IsPeriodic=0
    g7: GeomPoint X=302.567 Y=-42.9683 Z=0
    g8: GeomPoint X=306.073 Y=-40.8935 Z=0
    g9: Circle CenterX=371.567 CenterY=-80.8644 CenterZ=0 NormalX=0 NormalY=0 NormalZ=1 AngleXU=0 Radius=1
    g10: Circle CenterX=375.073 CenterY=-82.7896 CenterZ=0 NormalX=0 NormalY=0 NormalZ=1 AngleXU=0 Radius=1
    g11: Circle CenterX=375.073 CenterY=-78.7896 CenterZ=0 NormalX=0 NormalY=0 NormalZ=1 AngleXU=0 Radius=1
    g12: GeomPoint X=371.567 Y=-80.8644 Z=0
    g13: GeomPoint X=375.073 Y=-78.7896 Z=0
    g14: Circle CenterX=318.073 CenterY=-51.4823 CenterZ=0 NormalX=0 NormalY=0 NormalZ=1 AngleXU=0 Radius=1
    g15: Circle CenterX=318.073 CenterY=-47.4805 CenterZ=0 NormalX=0 NormalY=0 NormalZ=1 AngleXU=0 Radius=1
    g16: GeomPoint X=321.579 Y=-53.4075 Z=0
    g17: GeomPoint X=318.073 Y=-47.4805 Z=0
    g18: Circle CenterX=321.579 CenterY=-67.3492 CenterZ=0 NormalX=0 NormalY=0 NormalZ=1 AngleXU=0 Radius=1
    g19: Circle CenterX=318.073 CenterY=-65.424 CenterZ=0 NormalX=0 NormalY=0 NormalZ=1 AngleXU=0 Radius=1
    g20: Circle CenterX=318.073 CenterY=-69.424 CenterZ=0 NormalX=0 NormalY=0 NormalZ=1 AngleXU=0 Radius=1
    g21: GeomPoint X=321.579 Y=-67.3492 Z=0
    g22: GeomPoint X=318.073 Y=-69.424 Z=0
    g23: Circle CenterX=362.567 CenterY=-89.8542 CenterZ=0 NormalX=0 NormalY=0 NormalZ=1 AngleXU=0 Radius=1
    g24: Circle CenterX=366.073 CenterY=-91.7794 CenterZ=0 NormalX=0 NormalY=0 NormalZ=1 AngleXU=0 Radius=1
    g25: Circle CenterX=362.073 CenterY=-91.7794 CenterZ=0 NormalX=0 NormalY=0 NormalZ=1 AngleXU=0 Radius=1
    g26: GeomPoint X=362.567 Y=-89.8542 Z=0
    g27: GeomPoint X=362.073 Y=-91.7794 Z=0
    g28: Circle CenterX=322.073 CenterY=-91.7794 CenterZ=0 NormalX=0 NormalY=0 NormalZ=1 AngleXU=0 Radius=1
    g29: Circle CenterX=318.073 CenterY=-91.7794 CenterZ=0 NormalX=0 NormalY=0 NormalZ=1 AngleXU=0 Radius=1
    g30: Circle CenterX=318.073 CenterY=-87.7794 CenterZ=0 NormalX=0 NormalY=0 NormalZ=1 AngleXU=0 Radius=1
    g31: GeomPoint X=322.073 Y=-91.7794 Z=0
    g32: GeomPoint X=318.073 Y=-87.7794 Z=0
    g33: ArcOfCircle CenterX=391.073 CenterY=22.1087 CenterZ=0 NormalX=0 NormalY=0 NormalZ=1 AngleXU=0 Radius=4 StartAngle=0 EndAngle=3.14159
    g34: LineSegment StartX=387.073 StartY=22.1087 StartZ=0 EndX=383.073 EndY=-83.7794 EndZ=0
    g35: LineSegment StartX=395.073 StartY=22.1087 StartZ=0 EndX=399.073 EndY=-83.7794 EndZ=0
    g36: LineSegment StartX=232.072 StartY=-103.779 StartZ=0 EndX=232.072 EndY=-100.779 EndZ=0
    g37: GeomPoint X=232.072 Y=-94.7794 Z=0
    g38: GeomPoint X=223.072 Y=-97.7794 Z=0
    g39: Circle CenterX=232.072 CenterY=-94.7794 CenterZ=0 NormalX=0 NormalY=0 NormalZ=1 AngleXU=0 Radius=1
    g40: Circle CenterX=232.072 CenterY=-100.779 CenterZ=0 NormalX=0 NormalY=0 NormalZ=1 AngleXU=0 Radius=1
    g41: BSplineCurve PolesCount=5 KnotsCount=3 Degree=3 IsPeriodic=0
    g42: GeomPoint X=232.072 Y=-100.779 Z=0
    g43: LineSegment StartX=232.072 StartY=-94.7794 StartZ=0 EndX=232.072 EndY=-91.7794 EndZ=0
    g44: LineSegment StartX=245.072 StartY=-31.3037 StartZ=0 EndX=243.535 EndY=-33.1602 EndZ=0
    g45: LineSegment StartX=241.775 StartY=-35.2862 StartZ=0 EndX=240.266 EndY=-37.1092 EndZ=0
    g46: LineSegment StartX=243.535 StartY=-33.1602 StartZ=0 EndX=248.619 EndY=-37.3688 EndZ=0
    g47: LineSegment StartX=241.775 StartY=-35.2862 StartZ=0 EndX=246.859 EndY=-39.4949 EndZ=0
    g48: LineSegment StartX=248.619 StartY=-37.3688 StartZ=0 EndX=246.859 EndY=-39.4949 EndZ=0
    g49: LineSegment StartX=232.072 StartY=-103.779 StartZ=0 EndX=407.073 EndY=-103.779 EndZ=0
    g50: LineSegment StartX=299.888 StartY=-86.6413 StartZ=0 EndX=240.266 EndY=-37.1092 EndZ=0
    g51: LineSegment StartX=245.072 StartY=-11.4025 StartZ=0 EndX=302.567 EndY=-42.9683 EndZ=0
    g52: BSplineCurve PolesCount=3 KnotsCount=2 Degree=2 IsPeriodic=0
    g53: BSplineCurve PolesCount=3 KnotsCount=2 Degree=2 IsPeriodic=0
    g54: LineSegment StartX=321.579 StartY=-53.4075 StartZ=0 EndX=371.567 EndY=-80.8644 EndZ=0
    g55: BSplineCurve PolesCount=3 KnotsCount=2 Degree=2 IsPeriodic=0
    g56: BSplineCurve PolesCount=3 KnotsCount=2 Degree=2 IsPeriodic=0
    g57: BSplineCurve PolesCount=3 KnotsCount=2 Degree=2 IsPeriodic=0
    g58: LineSegment StartX=318.073 StartY=-69.424 StartZ=0 EndX=318.073 EndY=-87.7794 EndZ=0
    g59: LineSegment StartX=321.579 StartY=-67.3492 StartZ=0 EndX=362.567 EndY=-89.8542 EndZ=0
    g60: LineSegment StartX=362.073 StartY=-91.7794 StartZ=0 EndX=322.073 EndY=-91.7794 EndZ=0
    g61: BSplineCurve PolesCount=3 KnotsCount=2 Degree=2 IsPeriodic=0
    g62: BSplineCurve PolesCount=3 KnotsCount=2 Degree=2 IsPeriodic=0
    g63: LineSegment StartX=245.072 StartY=-31.3037 StartZ=0 EndX=302.996 EndY=-79.2541 EndZ=0
    g64: LineSegment StartX=302.567 StartY=-56.9099 StartZ=0 EndX=239.193 EndY=-22.1109 EndZ=0
    g65: LineSegment StartX=306.073 StartY=-62.8351 StartZ=0 EndX=306.073 EndY=-77.8102 EndZ=0
    g66: BSplineCurve PolesCount=3 KnotsCount=2 Degree=2 IsPeriodic=0
    g67: LineSegment StartX=298.776 StartY=-91.7794 StartZ=0 EndX=232.072 EndY=-91.7794 EndZ=0
    g68: LineSegment StartX=245.072 StartY=-11.4025 StartZ=0 EndX=243.628 EndY=-14.0323 EndZ=0
    g69: LineSegment StartX=240.741 StartY=-19.2917 StartZ=0 EndX=239.193 EndY=-22.1109 EndZ=0
    g70: LineSegment StartX=243.628 StartY=-14.0323 StartZ=0 EndX=246.258 EndY=-15.476 EndZ=0
    g71: LineSegment StartX=240.741 StartY=-19.2917 StartZ=0 EndX=243.37 EndY=-20.7355 EndZ=0
    g72: ArcOfCircle CenterX=247.444 CenterY=-19.5495 CenterZ=0 NormalX=0 NormalY=0 NormalZ=1 AngleXU=0 Radius=4.24264 StartAngle=3.4249 EndAngle=8.13729
    g73: LineSegment StartX=407.073 StartY=-103.779 StartZ=0 EndX=407.073 EndY=48.2206 EndZ=0
    g74: LineSegment StartX=375.073 StartY=48.2206 StartZ=0 EndX=375.073 EndY=-78.7896 EndZ=0
    g75: LineSegment StartX=375.073 StartY=48.2206 StartZ=0 EndX=382.073 EndY=48.2206 EndZ=0
    g76: LineSegment StartX=407.073 StartY=48.2206 StartZ=0 EndX=400.073 EndY=48.2206 EndZ=0
    g77: LineSegment StartX=394.073 StartY=48.2206 StartZ=0 EndX=394.073 EndY=52.2206 EndZ=0
    g78: LineSegment StartX=388.073 StartY=48.2206 StartZ=0 EndX=388.073 EndY=58.2206 EndZ=0
    g79: ArcOfCircle CenterX=385.073 CenterY=61.2206 CenterZ=0 NormalX=0 NormalY=0 NormalZ=1 AngleXU=0 Radius=4.24264 StartAngle=5.49779 EndAngle=10.2102
    g80: ArcOfCircle CenterX=397.073 CenterY=55.2206 CenterZ=0 NormalX=0 NormalY=0 NormalZ=1 AngleXU=0 Radius=4.24264 StartAngle=5.49779 EndAngle=10.2102
    g81: LineSegment StartX=382.073 StartY=58.2206 StartZ=0 EndX=382.073 EndY=48.2206 EndZ=0
    g82: LineSegment StartX=400.073 StartY=52.2206 StartZ=0 EndX=400.073 EndY=48.2206 EndZ=0
    g83: LineSegment StartX=394.073 StartY=48.2206 StartZ=0 EndX=388.073 EndY=48.2206 EndZ=0
    g84: LineSegment StartX=306.073 StartY=-40.8935 StartZ=0 EndX=306.073 EndY=-27.5935 EndZ=0
    g85: LineSegment StartX=318.073 StartY=-27.5935 StartZ=0 EndX=318.073 EndY=-47.4805 EndZ=0
    g86: LineSegment StartX=306.073 StartY=-27.5935 StartZ=0 EndX=310.073 EndY=-27.5935 EndZ=0
    g87: LineSegment StartX=318.073 StartY=-27.5935 StartZ=0 EndX=314.073 EndY=-27.5935 EndZ=0
    g88: LineSegment StartX=310.073 StartY=-27.5935 StartZ=0 EndX=310.073 EndY=-31.5935 EndZ=0
    g89: LineSegment StartX=314.073 StartY=-27.5935 StartZ=0 EndX=314.073 EndY=-31.5935 EndZ=0
    g90: ArcOfCircle CenterX=312.073 CenterY=-33.5935 CenterZ=0 NormalX=0 NormalY=0 NormalZ=1 AngleXU=0 Radius=2.82843 StartAngle=2.35619 EndAngle=7.06858
  constraints (121):
    c: Distance(g44) = 2.41
    c: Block(g44)
    c: Coincident(g46,g44)
    c: Coincident(g49,g36)
    c: Horizontal(g49)
    c: Block(g49)
    c: Coincident(g50,g45)
    c: Block(g50)
    c: Coincident(g51,g6)
    c: Block(g51)
    c: Coincident(g54,g52)
    c: Coincident(g54,g53)
    c: Coincident(g58,g56)
    c: Coincident(g58,g57)
    c: Vertical(g58)
    c: Coincident(g59,g56)
    c: Coincident(g59,g55)
    c: Coincident(g60,g55)
    c: Coincident(g60,g57)
    c: Horizontal(g60)
    c: Block(g61)
    c: Block(g62)
    c: Coincident(g63,g44)
    c: Coincident(g63,g62)
    c: Coincident(g64,g61)
    c: Coincident(g65,g61)
    c: Coincident(g65,g62)
    c: Vertical(g65)
    c: Block(g66)
    c: Coincident(g66,g50)
    c: Coincident(g67,g66)
    c: Coincident(g67,g43)
    c: Horizontal(g67)
    c: Coincident(g68,g51)
    c: Perpendicular(g68,g51)
    c: Coincident(g69,g64)
    c: Coincident(g70,g68)
    c: Distance(g70) = 3
    c: Distance(g71) = 3
    c: Perpendicular(g68,g70)
    c: Coincident(g72,g70)
    c: Coincident(g72,g71)
    c: Block(g72)
    c: Block(g69)
    c: Block(g71)
    c: Block(g54)
    c: Block(g59)
    c: Block(g58)
    c: Block(g60)
    c: Block(g67)
    c: Block(g43)
    c: Block(g36)
    c: Block(g48)
    c: Block(g46)
    c: Block(g47)
    c: Block(g45)
    c: Block(g35)
    c: Block(g34)
    c: Block(g0)
    c: Block(g33)
    c: Block(g52)
    c: Block(g6)
    c: Block(g41)
    c: Block(g57)
    c: Block(g55)
    c: Block(g53)
    c: Block(g68)
    c: Distance(g48) = 2.76
    c: Distance(g47) = 6.6
    c: Distance(g45) = 2.36657
    c: Coincident(g73,g49)
    c: Vertical(g73)
    c: Distance(g73) = 152
    c: Coincident(g74,g53)
    c: Vertical(g74)
    c: Block(g74)
    c: Coincident(g75,g74)
    c: Horizontal(g75)
    c: Distance(g75) = 7
    c: Horizontal(g76)
    c: Distance(g76) = 7
    c: Coincident(g76,g73)
    c: Vertical(g77)
    c: Distance(g77) = 4
    c: Vertical(g78)
    c: Distance(g78) = 10
    c: Coincident(g79,g78)
    c: Coincident(g80,g77)
    c: Block(g80)
    c: Block(g79)
    c: Coincident(g81,g79)
    c: Coincident(g81,g75)
    c: Vertical(g81)
    c: Coincident(g82,g80)
    c: Coincident(g82,g76)
    c: Vertical(g82)
    c: Coincident(g83,g77)
    c: Coincident(g83,g78)
    c: Horizontal(g83)
    c: Coincident(g84,g6)
    c: Vertical(g84)
    c: Distance(g84) = 13.3
    c: Coincident(g85,g52)
    c: Vertical(g85)
    c: Block(g85)
    c: Coincident(g86,g84)
    c: Horizontal(g86)
    c: Distance(g86) = 4
    c: Coincident(g87,g85)
    c: Horizontal(g87)
    c: Distance(g87) = 4
    c: Coincident(g88,g86)
    c: Vertical(g88)
    c: Coincident(g89,g87)
    c: Vertical(g89)
    c: Distance(g88) = 4
    c: Distance(g89) = 4
    c: Coincident(g90,g88)
    c: Coincident(g90,g89)
    c: Block(g90)
    c: Block(g56)
FEATURE [Sketcher::SketchObject] Sketch005  label="middleTop"
  FullyConstrained = true
  sketch-geometry (133):
    g0: Circle CenterX=175.025 CenterY=27.0667 CenterZ=0 NormalX=0 NormalY=0 NormalZ=1 AngleXU=0 Radius=1
    g1: Circle CenterX=179.022 CenterY=24.8665 CenterZ=0 NormalX=0 NormalY=0 NormalZ=1 AngleXU=0 Radius=1
    g2: Circle CenterX=179.022 CenterY=27.0606 CenterZ=0 NormalX=0 NormalY=0 NormalZ=1 AngleXU=0 Radius=1
    g3: BSplineCurve PolesCount=3 KnotsCount=2 Degree=2 IsPeriodic=0
    g4: GeomPoint X=175.025 Y=27.0667 Z=0
    g5: GeomPoint X=179.022 Y=27.0606 Z=0
    g6: Circle CenterX=189.124 CenterY=27.0628 CenterZ=0 NormalX=0 NormalY=0 NormalZ=1 AngleXU=0 Radius=1
    g7: Circle CenterX=185.124 CenterY=24.8665 CenterZ=0 NormalX=0 NormalY=0 NormalZ=1 AngleXU=0 Radius=1
    g8: Circle CenterX=185.124 CenterY=27.0606 CenterZ=0 NormalX=0 NormalY=0 NormalZ=1 AngleXU=0 Radius=1
    g9: BSplineCurve PolesCount=3 KnotsCount=2 Degree=2 IsPeriodic=0
    g10: GeomPoint X=189.124 Y=27.0628 Z=0
    g11: GeomPoint X=185.124 Y=27.0606 Z=0
    g12: Circle CenterX=165.871 CenterY=18.1458 CenterZ=0 NormalX=0 NormalY=0 NormalZ=1 AngleXU=0 Radius=1
    g13: Circle CenterX=169.377 CenterY=16.2206 CenterZ=0 NormalX=0 NormalY=0 NormalZ=1 AngleXU=0 Radius=1
    g14: Circle CenterX=165.871 CenterY=14.2956 CenterZ=0 NormalX=0 NormalY=0 NormalZ=1 AngleXU=0 Radius=1
    g15: BSplineCurve PolesCount=3 KnotsCount=2 Degree=2 IsPeriodic=0
    g16: GeomPoint X=165.871 Y=18.1458 Z=0
    g17: GeomPoint X=165.871 Y=14.2956 Z=0
    g18: Circle CenterX=198.275 CenterY=18.1318 CenterZ=0 NormalX=0 NormalY=0 NormalZ=1 AngleXU=0 Radius=1
    g19: Circle CenterX=194.768 CenterY=16.2206 CenterZ=0 NormalX=0 NormalY=0 NormalZ=1 AngleXU=0 Radius=1
    g20: Circle CenterX=198.264 CenterY=14.2963 CenterZ=0 NormalX=0 NormalY=0 NormalZ=1 AngleXU=0 Radius=1
    g21: BSplineCurve PolesCount=3 KnotsCount=2 Degree=2 IsPeriodic=0
    g22: GeomPoint X=198.275 Y=18.1318 Z=0
    g23: GeomPoint X=198.264 Y=14.2963 Z=0
    g24: Circle CenterX=125.607 CenterY=54.1951 CenterZ=0 NormalX=0 NormalY=0 NormalZ=1 AngleXU=0 Radius=1
    g25: Circle CenterX=139.632 CenterY=46.4944 CenterZ=0 NormalX=0 NormalY=0 NormalZ=1 AngleXU=0 Radius=1
    g26: Circle CenterX=127.326 CenterY=56.7187 CenterZ=0 NormalX=0 NormalY=0 NormalZ=1 AngleXU=0 Radius=1
    g27: BSplineCurve PolesCount=3 KnotsCount=2 Degree=2 IsPeriodic=0
    g28: GeomPoint X=125.607 Y=54.1951 Z=0
    g29: GeomPoint X=127.326 Y=56.7187 Z=0
    g30: Circle CenterX=236.824 CenterY=56.7187 CenterZ=0 NormalX=0 NormalY=0 NormalZ=1 AngleXU=0 Radius=1
    g31: Circle CenterX=224.513 CenterY=46.4944 CenterZ=0 NormalX=0 NormalY=0 NormalZ=1 AngleXU=0 Radius=1
    g32: Circle CenterX=238.538 CenterY=54.1951 CenterZ=0 NormalX=0 NormalY=0 NormalZ=1 AngleXU=0 Radius=1
    g33: BSplineCurve PolesCount=3 KnotsCount=2 Degree=2 IsPeriodic=0
    g34: GeomPoint X=236.824 Y=56.7187 Z=0
    g35: GeomPoint X=238.538 Y=54.1951 Z=0
    g36: Circle CenterX=189.121 CenterY=124.221 CenterZ=0 NormalX=0 NormalY=0 NormalZ=1 AngleXU=0 Radius=1
    g37: Circle CenterX=185.124 CenterY=124.221 CenterZ=0 NormalX=0 NormalY=0 NormalZ=1 AngleXU=0 Radius=1
    g38: Circle CenterX=185.124 CenterY=120.221 CenterZ=0 NormalX=0 NormalY=0 NormalZ=1 AngleXU=0 Radius=1
    g39: BSplineCurve PolesCount=3 KnotsCount=2 Degree=2 IsPeriodic=0
    g40: GeomPoint X=189.121 Y=124.221 Z=0
    g41: GeomPoint X=185.124 Y=120.221 Z=0
    g42: Circle CenterX=175.022 CenterY=124.221 CenterZ=0 NormalX=0 NormalY=0 NormalZ=1 AngleXU=0 Radius=1
    g43: Circle CenterX=179.022 CenterY=124.221 CenterZ=0 NormalX=0 NormalY=0 NormalZ=1 AngleXU=0 Radius=1
    g44: Circle CenterX=179.022 CenterY=120.221 CenterZ=0 NormalX=0 NormalY=0 NormalZ=1 AngleXU=0 Radius=1
    g45: BSplineCurve PolesCount=3 KnotsCount=2 Degree=2 IsPeriodic=0
    g46: GeomPoint X=175.022 Y=124.221 Z=0
    g47: GeomPoint X=179.022 Y=120.221 Z=0
    g48: LineSegment StartX=232.071 StartY=124.221 StartZ=0 EndX=232.071 EndY=127.221 EndZ=0
    g49-g52: Circle x4 (B-spline internal-alignment scaffolding for g53; pole/knot coordinates omitted)
    g53: BSplineCurve PolesCount=5 KnotsCount=3 Degree=3 IsPeriodic=0
    g54: GeomPoint X=232.072 Y=133.221 Z=0
    g55: GeomPoint X=223.072 Y=130.221 Z=0
    g56: GeomPoint X=232.071 Y=127.221 Z=0
    g57-g61: Circle x5 (B-spline internal-alignment scaffolding for g62; pole/knot coordinates omitted)
    g62: BSplineCurve PolesCount=5 KnotsCount=3 Degree=3 IsPeriodic=0
    g63: GeomPoint X=132.072 Y=133.221 Z=0
    g64: GeomPoint X=141.072 Y=130.221 Z=0
    g65: GeomPoint X=132.072 Y=127.221 Z=0
    g66: ArcOfCircle CenterX=247.391 CenterY=52.0843 CenterZ=0 NormalX=0 NormalY=0 NormalZ=1 AngleXU=0 Radius=4.24264 StartAngle=4.42912 EndAngle=9.14151
    g67: LineSegment StartX=240.687 StartY=51.8263 StartZ=0 EndX=239.192 EndY=54.5542 EndZ=0
    g68: LineSegment StartX=243.575 StartY=46.5669 StartZ=0 EndX=245.072 EndY=43.8408 EndZ=0
    g69: LineSegment StartX=240.168 StartY=69.471 StartZ=0 EndX=241.708 EndY=67.6172 EndZ=0
    g70: LineSegment StartX=246.783 StartY=71.8328 StartZ=0 EndX=248.546 EndY=69.7098 EndZ=0
    g71: LineSegment StartX=245.073 StartY=63.5726 StartZ=0 EndX=243.476 EndY=65.4955 EndZ=0
    g72: LineSegment StartX=123.967 StartY=69.4706 StartZ=0 EndX=122.37 EndY=67.5474 EndZ=0
    g73: LineSegment StartX=232.072 StartY=133.221 StartZ=0 EndX=232.072 EndY=136.221 EndZ=0
    g74: LineSegment StartX=232.072 StartY=136.221 StartZ=0 EndX=132.072 EndY=136.221 EndZ=0
    g75: LineSegment StartX=132.072 StartY=136.221 StartZ=0 EndX=132.072 EndY=133.221 EndZ=0
    g76: LineSegment StartX=132.072 StartY=127.221 StartZ=0 EndX=132.072 EndY=124.221 EndZ=0
    g77: LineSegment StartX=132.072 StartY=124.221 StartZ=0 EndX=175.022 EndY=124.221 EndZ=0
    g78: LineSegment StartX=189.121 StartY=124.221 StartZ=0 EndX=232.071 EndY=124.221 EndZ=0
    g79: LineSegment StartX=185.124 StartY=120.221 StartZ=0 EndX=185.124 EndY=27.0606 EndZ=0
    g80: LineSegment StartX=189.124 StartY=27.0628 StartZ=0 EndX=240.168 EndY=69.471 EndZ=0
    g81: LineSegment StartX=241.708 StartY=67.6172 StartZ=0 EndX=246.783 EndY=71.8328 EndZ=0
    g82: LineSegment StartX=248.546 StartY=69.7098 StartZ=0 EndX=243.476 EndY=65.4955 EndZ=0
    g83: LineSegment StartX=245.073 StartY=63.5726 StartZ=0 EndX=236.824 EndY=56.7187 EndZ=0
    g84: LineSegment StartX=238.538 StartY=54.1951 StartZ=0 EndX=239.192 EndY=54.5542 EndZ=0
    g85: LineSegment StartX=240.687 StartY=51.8263 StartZ=0 EndX=243.317 EndY=53.2701 EndZ=0
    g86: LineSegment StartX=246.205 StartY=48.0108 StartZ=0 EndX=243.575 EndY=46.5669 EndZ=0
    g87: LineSegment StartX=245.072 StartY=43.8408 StartZ=0 EndX=198.275 EndY=18.1318 EndZ=0
    g88: LineSegment StartX=165.871 StartY=18.1458 StartZ=0 EndX=118.934 EndY=43.9178 EndZ=0
    g89: LineSegment StartX=118.934 StartY=43.9178 StartZ=0 EndX=120.377 EndY=46.5474 EndZ=0
    g90: LineSegment StartX=117.748 StartY=47.9913 StartZ=0 EndX=120.377 EndY=46.5474 EndZ=0
    g91: LineSegment StartX=120.635 StartY=53.2507 StartZ=0 EndX=123.265 EndY=51.8068 EndZ=0
    g92: LineSegment StartX=123.265 StartY=51.8068 StartZ=0 EndX=124.73 EndY=54.6766 EndZ=0
    g93: ArcOfCircle CenterX=116.562 CenterY=52.0649 CenterZ=0 NormalX=0 NormalY=0 NormalZ=1 AngleXU=0 Radius=4.24264 StartAngle=0.283267 EndAngle=4.99566
    g94: LineSegment StartX=124.73 StartY=54.6766 StartZ=0 EndX=125.607 EndY=54.1951 EndZ=0
    g95: LineSegment StartX=127.326 StartY=56.7187 StartZ=0 EndX=119.072 EndY=63.5741 EndZ=0
    g96: LineSegment StartX=119.072 StartY=63.5741 StartZ=0 EndX=120.669 EndY=65.4973 EndZ=0
    g97: LineSegment StartX=120.669 StartY=65.4973 StartZ=0 EndX=115.591 EndY=69.7147 EndZ=0
    g98: LineSegment StartX=115.591 StartY=69.7147 StartZ=0 EndX=117.293 EndY=71.7641 EndZ=0
    g99: LineSegment StartX=117.293 StartY=71.7641 StartZ=0 EndX=122.37 EndY=67.5474 EndZ=0
    g100: LineSegment StartX=123.967 StartY=69.4706 StartZ=0 EndX=175.025 EndY=27.0667 EndZ=0
    g101: LineSegment StartX=179.022 StartY=27.0606 StartZ=0 EndX=179.022 EndY=120.221 EndZ=0
    g102-g117: Circle x16 (B-spline internal-alignment scaffolding for g118; pole/knot coordinates omitted)
    g118: BSplineCurve PolesCount=16 KnotsCount=14 Degree=3 IsPeriodic=0
    g119-g132: GeomPoint x14 (B-spline internal-alignment scaffolding for g118; pole/knot coordinates omitted)
  constraints (180):
    c: Weight(g0) = 1
    c: Equal(g0,g1)
    c: Equal(g0,g2)
    c: InternalAlignment(g0,g3)
    c: InternalAlignment(g1,g3)
    c: InternalAlignment(g2,g3)
    c: InternalAlignment(g4,g3)
    c: InternalAlignment(g5,g3)
    c: Weight(g6) = 1
    c: Equal(g6,g7)
    c: Equal(g6,g8)
    c: InternalAlignment(g6,g9)
    c: InternalAlignment(g7,g9)
    c: InternalAlignment(g8,g9)
    c: InternalAlignment(g10,g9)
    c: InternalAlignment(g11,g9)
    c: Block(g9)
    c: Block(g3)
    c: Weight(g12) = 1
    c: Equal(g12,g13)
    c: Equal(g12,g14)
    c: InternalAlignment(g12,g15)
    c: InternalAlignment(g13,g15)
    c: InternalAlignment(g14,g15)
    c: InternalAlignment(g16,g15)
    c: InternalAlignment(g17,g15)
    c: Weight(g18) = 1
    c: Equal(g18,g19)
    c: Equal(g18,g20)
    c: InternalAlignment(g18,g21)
    c: InternalAlignment(g19,g21)
    c: InternalAlignment(g20,g21)
    c: InternalAlignment(g22,g21)
    c: InternalAlignment(g23,g21)
    c: Block(g15)
    c: Block(g21)
    c: Weight(g24) = 1
    c: Equal(g24,g25)
    c: Equal(g24,g26)
    c: InternalAlignment(g24,g27)
    c: InternalAlignment(g25,g27)
    c: InternalAlignment(g26,g27)
    c: InternalAlignment(g28,g27)
    c: InternalAlignment(g29,g27)
    c: Block(g27)
    c: Weight(g30) = 1
    c: Equal(g30,g31)
    c: Equal(g30,g32)
    c: InternalAlignment(g30,g33)
    c: InternalAlignment(g31,g33)
    c: InternalAlignment(g32,g33)
    c: InternalAlignment(g34,g33)
    c: InternalAlignment(g35,g33)
    c: Block(g33)
    c: Weight(g36) = 1
    c: Equal(g36,g37)
    c: Equal(g36,g38)
    c: InternalAlignment(g36,g39)
    c: InternalAlignment(g37,g39)
    c: InternalAlignment(g38,g39)
    c: InternalAlignment(g40,g39)
    c: InternalAlignment(g41,g39)
    c: Weight(g42) = 1
    c: Equal(g42,g43)
    c: Equal(g42,g44)
    c: InternalAlignment(g42,g45)
    c: InternalAlignment(g43,g45)
    c: InternalAlignment(g44,g45)
    c: InternalAlignment(g46,g45)
    c: InternalAlignment(g47,g45)
    c: Block(g45)
    c: Block(g39)
    c: Vertical(g48)
    c: Distance(g48) = 3
    c: Weight(g49) = 1
    c: Equal(g49,g50)
    c: Equal(g49,g51)
    c: Equal(g49,g52)
    c: Coincident(g53,g48)
    c: InternalAlignment(g49-g52 -> g53) x4
    c: InternalAlignment(g54,g53)
    c: InternalAlignment(g55,g53)
    c: InternalAlignment(g56,g53)
    c: Weight(g57) = 1
    c: Equal(g57, g58-g61) x4
    c: InternalAlignment(g57-g61 -> g62) x5
    c: InternalAlignment(g63,g62)
    c: InternalAlignment(g64,g62)
    c: InternalAlignment(g65,g62)
    c: Block(g62)
    c: Block(g67)
    c: Block(g68)
    c: Distance(g69) = 2.41
    c: Distance(g70) = 2.76
    c: Distance(g71) = 2.5
    c: Distance(g72) = 2.5
    c: Block(g66)
    c: Block(g48)
    c: Block(g53)
    c: Coincident(g73,g53)
    c: Vertical(g73)
    c: Distance(g73) = 3
    c: Coincident(g74,g73)
    c: Horizontal(g74)
    c: Distance(g74) = 100
    c: Coincident(g75,g74)
    c: Coincident(g75,g62)
    c: Vertical(g75)
    c: Distance(g75) = 3
    c: Coincident(g76,g62)
    c: Vertical(g76)
    c: Distance(g76) = 3
    c: Coincident(g77,g76)
    c: Coincident(g77,g45)
    c: Horizontal(g77)
    c: Distance(g77) = 42.95
    c: Coincident(g78,g39)
    c: Coincident(g78,g48)
    c: Horizontal(g78)
    c: Distance(g78) = 42.95
    c: Coincident(g79,g39)
    c: Coincident(g79,g9)
    c: Vertical(g79)
    c: Distance(g79) = 93.16
    c: Coincident(g80,g9)
    c: Coincident(g80,g69)
    c: Angle(g80) = 0.693245
    c: Block(g80)
    c: Coincident(g81,g69)
    c: Coincident(g81,g70)
    c: Block(g81)
    c: Coincident(g82,g70)
    c: Coincident(g82,g71)
    c: Block(g82)
    c: Coincident(g83,g71)
    c: Coincident(g83,g33)
    c: Block(g71)
    c: Coincident(g84,g33)
    c: Coincident(g84,g67)
    c: Coincident(g85,g67)
    c: Coincident(g85,g66)
    c: Coincident(g86,g66)
    c: Coincident(g86,g68)
    c: Coincident(g87,g68)
    c: Coincident(g87,g21)
    c: Coincident(g88,g15)
    c: Coincident(g89,g88)
    c: Block(g89)
    c: Coincident(g90,g89)
    c: Block(g90)
    c: Block(g91)
    c: Coincident(g92,g91)
    c: Block(g92)
    c: Coincident(g93,g91)
    c: Coincident(g93,g90)
    c: Block(g93)
    c: Coincident(g94,g92)
    c: Coincident(g94,g27)
    c: Coincident(g95,g27)
    c: Block(g95)
    c: Coincident(g96,g95)
    c: Coincident(g97,g96)
    c: Coincident(g98,g97)
    c: Coincident(g99,g98)
    c: Coincident(g99,g72)
    c: Block(g98)
    c: Block(g96)
    c: Block(g72)
    c: Coincident(g100,g72)
    c: Coincident(g100,g3)
    c: Coincident(g101,g3)
    c: Coincident(g101,g45)
    c: Vertical(g101)
    c: Coincident(g118,g21)
    c: Weight(g102) = 1
    c: Equal(g102, g103-g117) x15
    c: Coincident(g118,g15)
    c: InternalAlignment(g102-g117 -> g118) x16
    c: InternalAlignment(g119-g132 -> g118) x14
    c: Block(g118)
FEATURE [Sketcher::SketchObject] Sketch006  label="leftSideTop"
  FullyConstrained = true
  sketch-geometry (99):
    g0: Circle CenterX=61.1495 CenterY=111.695 CenterZ=0 NormalX=0 NormalY=0 NormalZ=1 AngleXU=0 Radius=1
    g1: Circle CenterX=58.0728 CenterY=114.251 CenterZ=0 NormalX=0 NormalY=0 NormalZ=1 AngleXU=0 Radius=1
    g2: Circle CenterX=58.0728 CenterY=110.251 CenterZ=0 NormalX=0 NormalY=0 NormalZ=1 AngleXU=0 Radius=1
    g3: BSplineCurve PolesCount=3 KnotsCount=2 Degree=2 IsPeriodic=0
    g4: GeomPoint X=61.1495 Y=111.695 Z=0
    g5: GeomPoint X=58.0728 Y=110.251 Z=0
    g6: Circle CenterX=61.5791 CenterY=89.3511 CenterZ=0 NormalX=0 NormalY=0 NormalZ=1 AngleXU=0 Radius=1
    g7: Circle CenterX=58.0728 CenterY=91.2763 CenterZ=0 NormalX=0 NormalY=0 NormalZ=1 AngleXU=0 Radius=1
    g8: Circle CenterX=58.0728 CenterY=95.2763 CenterZ=0 NormalX=0 NormalY=0 NormalZ=1 AngleXU=0 Radius=1
    g9: BSplineCurve PolesCount=3 KnotsCount=2 Degree=2 IsPeriodic=0
    g10: GeomPoint X=61.5791 Y=89.3511 Z=0
    g11: GeomPoint X=58.0728 Y=95.2763 Z=0
    g12: Circle CenterX=62.0728 CenterY=124.221 CenterZ=0 NormalX=0 NormalY=0 NormalZ=1 AngleXU=0 Radius=1
    g13: Circle CenterX=58.0728 CenterY=124.221 CenterZ=0 NormalX=0 NormalY=0 NormalZ=1 AngleXU=0 Radius=1
    g14: Circle CenterX=61.1496 CenterY=121.665 CenterZ=0 NormalX=0 NormalY=0 NormalZ=1 AngleXU=0 Radius=1
    g15: BSplineCurve PolesCount=3 KnotsCount=2 Degree=2 IsPeriodic=0
    g16: GeomPoint X=62.0728 Y=124.221 Z=0
    g17: GeomPoint X=61.1496 Y=121.665 Z=0
    g18: Circle CenterX=61.5791 CenterY=75.4095 CenterZ=0 NormalX=0 NormalY=0 NormalZ=1 AngleXU=0 Radius=1
    g19: Circle CenterX=58.0728 CenterY=77.3346 CenterZ=0 NormalX=0 NormalY=0 NormalZ=1 AngleXU=0 Radius=1
    g20: Circle CenterX=58.0728 CenterY=73.3346 CenterZ=0 NormalX=0 NormalY=0 NormalZ=1 AngleXU=0 Radius=1
    g21: BSplineCurve PolesCount=3 KnotsCount=2 Degree=2 IsPeriodic=0
    g22: GeomPoint X=61.5791 Y=75.4095 Z=0
    g23: GeomPoint X=58.0728 Y=73.3346 Z=0
    g24: Circle CenterX=2.07281 CenterY=124.221 CenterZ=0 NormalX=0 NormalY=0 NormalZ=1 AngleXU=0 Radius=1
    g25: Circle CenterX=1.57905 CenterY=122.295 CenterZ=0 NormalX=0 NormalY=0 NormalZ=1 AngleXU=0 Radius=1
    g26: BSplineCurve PolesCount=3 KnotsCount=2 Degree=2 IsPeriodic=0
    g27: GeomPoint X=2.07281 Y=124.221 Z=0
    g28: GeomPoint X=1.57905 Y=122.295 Z=0
    g29: Circle CenterX=46.0728 CenterY=124.221 CenterZ=0 NormalX=0 NormalY=0 NormalZ=1 AngleXU=0 Radius=1
    g30: Circle CenterX=46.0728 CenterY=120.221 CenterZ=0 NormalX=0 NormalY=0 NormalZ=1 AngleXU=0 Radius=1
    g31: BSplineCurve PolesCount=3 KnotsCount=2 Degree=2 IsPeriodic=0
    g32: GeomPoint X=42.0728 Y=124.221 Z=0
    g33: GeomPoint X=46.0728 Y=120.221 Z=0
    g34: Circle CenterX=46.0728 CenterY=109.865 CenterZ=0 NormalX=0 NormalY=0 NormalZ=1 AngleXU=0 Radius=1
    g35: Circle CenterX=46.0728 CenterY=105.865 CenterZ=0 NormalX=0 NormalY=0 NormalZ=1 AngleXU=0 Radius=1
    g36: Circle CenterX=42.0728 CenterY=105.865 CenterZ=0 NormalX=0 NormalY=0 NormalZ=1 AngleXU=0 Radius=1
    g37: BSplineCurve PolesCount=3 KnotsCount=2 Degree=2 IsPeriodic=0
    g38: GeomPoint X=46.0728 Y=109.865 Z=0
    g39: GeomPoint X=42.0728 Y=105.865 Z=0
    g40: Circle CenterX=35.5028 CenterY=105.865 CenterZ=0 NormalX=0 NormalY=0 NormalZ=1 AngleXU=0 Radius=1
    g41: Circle CenterX=31.5028 CenterY=105.865 CenterZ=0 NormalX=0 NormalY=0 NormalZ=1 AngleXU=0 Radius=1
    g42: Circle CenterX=27.9965 CenterY=107.79 CenterZ=0 NormalX=0 NormalY=0 NormalZ=1 AngleXU=0 Radius=1
    g43: BSplineCurve PolesCount=3 KnotsCount=2 Degree=2 IsPeriodic=0
    g44: GeomPoint X=35.5028 Y=105.865 Z=0
    g45: GeomPoint X=27.9965 Y=107.79 Z=0
    g46-g50: Circle x5 (B-spline internal-alignment scaffolding for g51; pole/knot coordinates omitted)
    g51: BSplineCurve PolesCount=5 KnotsCount=3 Degree=3 IsPeriodic=0
    g52: GeomPoint X=132.072 Y=133.221 Z=0
    g53: GeomPoint X=141.072 Y=130.221 Z=0
    g54: GeomPoint X=132.072 Y=127.221 Z=0
    g55: ArcOfCircle CenterX=116.562 CenterY=52.0649 CenterZ=0 NormalX=0 NormalY=0 NormalZ=1 AngleXU=0 Radius=4.24264 StartAngle=0.283268 EndAngle=4.99566
    g56: LineSegment StartX=123.967 StartY=69.4706 StartZ=0 EndX=122.37 EndY=67.5474 EndZ=0
    g57: LineSegment StartX=117.293 StartY=71.7641 StartZ=0 EndX=115.591 EndY=69.7147 EndZ=0
    g58: LineSegment StartX=120.669 StartY=65.4973 StartZ=0 EndX=119.072 EndY=63.5741 EndZ=0
    g59: LineSegment StartX=124.73 StartY=54.6766 StartZ=0 EndX=123.265 EndY=51.8068 EndZ=0
    g60: LineSegment StartX=120.377 StartY=46.5474 StartZ=0 EndX=118.934 EndY=43.9178 EndZ=0
    g61: BSplineCurve PolesCount=3 KnotsCount=2 Degree=2 IsPeriodic=0
    g62: BSplineCurve PolesCount=3 KnotsCount=2 Degree=2 IsPeriodic=0
    g63: LineSegment StartX=61.5791 StartY=75.4095 StartZ=0 EndX=118.934 EndY=43.9178 EndZ=0
    g64: LineSegment StartX=117.748 StartY=47.9913 StartZ=0 EndX=120.377 EndY=46.5474 EndZ=0
    g65: LineSegment StartX=120.635 StartY=53.2507 StartZ=0 EndX=123.265 EndY=51.8068 EndZ=0
    g66: LineSegment StartX=124.73 StartY=54.6766 StartZ=0 EndX=61.5791 EndY=89.3511 EndZ=0
    g67: LineSegment StartX=58.0728 StartY=95.2763 StartZ=0 EndX=58.0728 EndY=110.251 EndZ=0
    g68: LineSegment StartX=61.1495 StartY=111.695 StartZ=0 EndX=119.072 EndY=63.5741 EndZ=0
    g69: LineSegment StartX=120.669 StartY=65.4973 StartZ=0 EndX=115.591 EndY=69.7147 EndZ=0
    g70: LineSegment StartX=117.293 StartY=71.7641 StartZ=0 EndX=122.37 EndY=67.5474 EndZ=0
    g71: LineSegment StartX=123.967 StartY=69.4706 StartZ=0 EndX=61.1496 EndY=121.665 EndZ=0
    g72: LineSegment StartX=62.0728 StartY=124.221 StartZ=0 EndX=132.072 EndY=124.221 EndZ=0
    g73: LineSegment StartX=132.072 StartY=127.221 StartZ=0 EndX=132.072 EndY=124.221 EndZ=0
    g74: LineSegment StartX=132.072 StartY=133.221 StartZ=0 EndX=132.072 EndY=136.221 EndZ=0
    g75: LineSegment StartX=132.072 StartY=136.221 StartZ=0 EndX=-42.9272 EndY=136.221 EndZ=0
    g76: LineSegment StartX=2.07281 StartY=124.221 StartZ=0 EndX=42.0728 EndY=124.221 EndZ=0
    g77: LineSegment StartX=46.0728 StartY=120.221 StartZ=0 EndX=46.0728 EndY=109.865 EndZ=0
    g78: LineSegment StartX=42.0728 StartY=105.865 StartZ=0 EndX=35.5028 EndY=105.865 EndZ=0
    g79: LineSegment StartX=27.9965 StartY=107.79 StartZ=0 EndX=1.57905 EndY=122.295 EndZ=0
    g80: LineSegment StartX=-6.92718 StartY=76.4095 StartZ=0 EndX=42.0728 EndY=76.4095 EndZ=0
    g81: LineSegment StartX=-17.9272 StartY=48.2206 StartZ=0 EndX=-17.9272 EndY=58.2206 EndZ=0
    g82: LineSegment StartX=-35.9272 StartY=48.2206 StartZ=0 EndX=-35.9272 EndY=52.2206 EndZ=0
    g83: LineSegment StartX=-29.9272 StartY=48.2206 StartZ=0 EndX=-29.9272 EndY=52.2206 EndZ=0
    g84: LineSegment StartX=-23.9272 StartY=48.2206 StartZ=0 EndX=-23.9272 EndY=58.2206 EndZ=0
    g85: ArcOfCircle CenterX=-32.9272 CenterY=55.2206 CenterZ=0 NormalX=0 NormalY=0 NormalZ=1 AngleXU=0 Radius=4.24264 StartAngle=5.49779 EndAngle=10.2102
    g86: ArcOfCircle CenterX=-20.9272 CenterY=61.2206 CenterZ=0 NormalX=0 NormalY=0 NormalZ=1 AngleXU=0 Radius=4.24264 StartAngle=5.49779 EndAngle=10.2102
    g87: LineSegment StartX=-10.9272 StartY=48.2206 StartZ=0 EndX=-10.9272 EndY=72.4095 EndZ=0
    g88: LineSegment StartX=-42.9272 StartY=48.2206 StartZ=0 EndX=-42.9272 EndY=136.221 EndZ=0
    g89: LineSegment StartX=46.0728 StartY=72.4095 StartZ=0 EndX=46.0728 EndY=-27.5905 EndZ=0
    g90: LineSegment StartX=58.0728 StartY=-27.5905 StartZ=0 EndX=58.0728 EndY=73.3346 EndZ=0
    g91: LineSegment StartX=50.0728 StartY=-27.5905 StartZ=0 EndX=50.0728 EndY=-31.5905 EndZ=0
    g92: LineSegment StartX=54.0728 StartY=-27.5905 StartZ=0 EndX=54.0728 EndY=-31.5905 EndZ=0
    g93: ArcOfCircle CenterX=52.0728 CenterY=-33.5905 CenterZ=0 NormalX=0 NormalY=0 NormalZ=1 AngleXU=0 Radius=2.82843 StartAngle=2.35619 EndAngle=7.06858
    g94: LineSegment StartX=46.0728 StartY=-27.5905 StartZ=0 EndX=50.0728 EndY=-27.5905 EndZ=0
    g95: LineSegment StartX=54.0728 StartY=-27.5905 StartZ=0 EndX=58.0728 EndY=-27.5905 EndZ=0
    g96: LineSegment StartX=-17.9272 StartY=48.2206 StartZ=0 EndX=-10.9272 EndY=48.2206 EndZ=0
    g97: LineSegment StartX=-29.9272 StartY=48.2206 StartZ=0 EndX=-23.9272 EndY=48.2206 EndZ=0
    g98: LineSegment StartX=-42.9272 StartY=48.2206 StartZ=0 EndX=-35.9272 EndY=48.2206 EndZ=0
  constraints (172):
    c: Weight(g0) = 1
    c: Equal(g0,g1)
    c: Equal(g0,g2)
    c: InternalAlignment(g0,g3)
    c: InternalAlignment(g1,g3)
    c: InternalAlignment(g2,g3)
    c: InternalAlignment(g4,g3)
    c: InternalAlignment(g5,g3)
    c: Weight(g6) = 1
    c: Equal(g6,g7)
    c: Equal(g6,g8)
    c: InternalAlignment(g6,g9)
    c: InternalAlignment(g7,g9)
    c: InternalAlignment(g8,g9)
    c: InternalAlignment(g10,g9)
    c: InternalAlignment(g11,g9)
    c: Block(g3)
    c: Block(g9)
    c: Weight(g12) = 1
    c: Equal(g12,g13)
    c: Equal(g12,g14)
    c: InternalAlignment(g12,g15)
    c: InternalAlignment(g13,g15)
    c: InternalAlignment(g14,g15)
    c: InternalAlignment(g16,g15)
    c: InternalAlignment(g17,g15)
    c: Block(g15)
    c: Weight(g18) = 1
    c: Equal(g18,g19)
    c: Equal(g18,g20)
    c: InternalAlignment(g18,g21)
    c: InternalAlignment(g19,g21)
    c: InternalAlignment(g20,g21)
    c: InternalAlignment(g22,g21)
    c: InternalAlignment(g23,g21)
    c: Block(g21)
    c: Weight(g24) = 1
    c: Equal(g24,g25)
    c: InternalAlignment(g24,g26)
    c: InternalAlignment(g25,g26)
    c: InternalAlignment(g27,g26)
    c: InternalAlignment(g28,g26)
    c: InternalAlignment(g29,g31)
    c: InternalAlignment(g30,g31)
    c: InternalAlignment(g32,g31)
    c: InternalAlignment(g33,g31)
    c: Weight(g34) = 1
    c: Equal(g34,g35)
    c: Equal(g34,g36)
    c: InternalAlignment(g34,g37)
    c: InternalAlignment(g35,g37)
    c: InternalAlignment(g36,g37)
    c: InternalAlignment(g38,g37)
    c: InternalAlignment(g39,g37)
    c: Equal(g40,g41)
    c: Equal(g40,g42)
    c: InternalAlignment(g40,g43)
    c: InternalAlignment(g41,g43)
    c: InternalAlignment(g42,g43)
    c: InternalAlignment(g44,g43)
    c: InternalAlignment(g45,g43)
    c: Block(g31)
    c: Block(g37)
    c: Block(g43)
    c: Block(g26)
    c: Weight(g46) = 1
    c: Equal(g46, g47-g50) x4
    c: InternalAlignment(g46-g50 -> g51) x5
    c: InternalAlignment(g52,g51)
    c: InternalAlignment(g53,g51)
    c: InternalAlignment(g54,g51)
    c: Block(g51)
    c: Block(g55)
    c: Block(g56)
    c: Block(g57)
    c: Block(g58)
    c: Block(g59)
    c: Block(g60)
    c: Block(g61)
    c: Block(g62)
    c: Coincident(g90,g21)
    c: Coincident(g63,g21)
    c: Coincident(g63,g60)
    c: Coincident(g64,g55)
    c: Coincident(g64,g60)
    c: Coincident(g65,g55)
    c: Coincident(g65,g59)
    c: Coincident(g66,g59)
    c: Coincident(g66,g9)
    c: Coincident(g67,g9)
    c: Coincident(g67,g3)
    c: Vertical(g67)
    c: Coincident(g68,g3)
    c: Coincident(g68,g58)
    c: Coincident(g69,g58)
    c: Coincident(g69,g57)
    c: Coincident(g70,g57)
    c: Coincident(g70,g56)
    c: Coincident(g71,g56)
    c: Coincident(g71,g15)
    c: Coincident(g72,g15)
    c: Horizontal(g72)
    c: Coincident(g73,g51)
    c: Coincident(g73,g72)
    c: Vertical(g73)
    c: Coincident(g74,g51)
    c: Vertical(g74)
    c: Coincident(g75,g74)
    c: Horizontal(g75)
    c: Coincident(g76,g26)
    c: Coincident(g76,g31)
    c: Horizontal(g76)
    c: Coincident(g77,g31)
    c: Coincident(g77,g37)
    c: Vertical(g77)
    c: Coincident(g78,g37)
    c: Coincident(g78,g43)
    c: Horizontal(g78)
    c: Coincident(g79,g43)
    c: Coincident(g79,g26)
    c: Coincident(g80,g62)
    c: Coincident(g80,g61)
    c: Horizontal(g80)
    c: Vertical(g81)
    c: Distance(g81) = 10
    c: Vertical(g82)
    c: Distance(g82) = 4
    c: Vertical(g83)
    c: Distance(g83) = 4
    c: Vertical(g84)
    c: Distance(g84) = 10
    c: Coincident(g85,g83)
    c: Coincident(g85,g82)
    c: Block(g85)
    c: Coincident(g86,g84)
    c: Coincident(g86,g81)
    c: Block(g86)
    c: Coincident(g87,g62)
    c: Vertical(g87)
    c: Coincident(g88,g75)
    c: Vertical(g88)
    c: Block(g75)
    c: Coincident(g89,g61)
    c: Vertical(g89)
    c: Distance(g89) = 100
    c: Block(g90)
    c: Vertical(g91)
    c: Distance(g91) = 4
    c: Vertical(g92)
    c: Distance(g92) = 4
    c: Coincident(g93,g91)
    c: Coincident(g93,g92)
    c: Block(g93)
    c: Coincident(g94,g89)
    c: Coincident(g94,g91)
    c: Horizontal(g94)
    c: Distance(g94) = 4
    c: Coincident(g95,g92)
    c: Coincident(g95,g90)
    c: Horizontal(g95)
    c: Distance(g95) = 4
    c: Block(g87)
    c: Block(g88)
    c: Coincident(g96,g81)
    c: Coincident(g96,g87)
    c: Horizontal(g96)
    c: Coincident(g97,g83)
    c: Coincident(g97,g84)
    c: Horizontal(g97)
    c: Coincident(g98,g88)
    c: Coincident(g98,g82)
    c: Horizontal(g98)
FEATURE [Sketcher::SketchObject] Sketch007  label="leftSideBottom"
  FullyConstrained = true
  sketch-geometry (92):
    g0: ArcOfCircle CenterX=-26.9272 CenterY=-83.7794 CenterZ=0 NormalX=0 NormalY=0 NormalZ=1 AngleXU=0 Radius=8 StartAngle=3.14159 EndAngle=6.28319
    g1: Circle CenterX=61.5791 CenterY=-56.9099 CenterZ=0 NormalX=0 NormalY=0 NormalZ=1 AngleXU=0 Radius=1
    g2: Circle CenterX=58.0728 CenterY=-58.8351 CenterZ=0 NormalX=0 NormalY=0 NormalZ=1 AngleXU=0 Radius=1
    g3: Circle CenterX=58.0728 CenterY=-62.8351 CenterZ=0 NormalX=0 NormalY=0 NormalZ=1 AngleXU=0 Radius=1
    g4: BSplineCurve PolesCount=3 KnotsCount=2 Degree=2 IsPeriodic=0
    g5: GeomPoint X=61.5791 Y=-56.9099 Z=0
    g6: GeomPoint X=58.0728 Y=-62.8351 Z=0
    g7: Circle CenterX=58.0728 CenterY=-77.8102 CenterZ=0 NormalX=0 NormalY=0 NormalZ=1 AngleXU=0 Radius=1
    g8: Circle CenterX=58.0728 CenterY=-81.8102 CenterZ=0 NormalX=0 NormalY=0 NormalZ=1 AngleXU=0 Radius=1
    g9: Circle CenterX=61.1496 CenterY=-79.2541 CenterZ=0 NormalX=0 NormalY=0 NormalZ=1 AngleXU=0 Radius=1
    g10: BSplineCurve PolesCount=3 KnotsCount=2 Degree=2 IsPeriodic=0
    g11: GeomPoint X=58.0728 Y=-77.8102 Z=0
    g12: GeomPoint X=61.1496 Y=-79.2541 Z=0
    g13: Circle CenterX=61.6457 CenterY=-88.8112 CenterZ=0 NormalX=0 NormalY=0 NormalZ=1 AngleXU=0 Radius=1
    g14: Circle CenterX=58.0728 CenterY=-91.7794 CenterZ=0 NormalX=0 NormalY=0 NormalZ=1 AngleXU=0 Radius=1
    g15: Circle CenterX=63.9135 CenterY=-91.8014 CenterZ=0 NormalX=0 NormalY=0 NormalZ=1 AngleXU=0 Radius=1
    g16: BSplineCurve PolesCount=3 KnotsCount=2 Degree=2 IsPeriodic=0
    g17: GeomPoint X=61.6457 Y=-88.8112 Z=0
    g18: GeomPoint X=63.9135 Y=-91.8014 Z=0
    g19: Circle CenterX=58.0728 CenterY=-40.8935 CenterZ=0 NormalX=0 NormalY=0 NormalZ=1 AngleXU=0 Radius=1
    g20: Circle CenterX=58.0728 CenterY=-44.8935 CenterZ=0 NormalX=0 NormalY=0 NormalZ=1 AngleXU=0 Radius=1
    g21: Circle CenterX=61.5791 CenterY=-42.9683 CenterZ=0 NormalX=0 NormalY=0 NormalZ=1 AngleXU=0 Radius=1
    g22: BSplineCurve PolesCount=3 KnotsCount=2 Degree=2 IsPeriodic=0
    g23: GeomPoint X=58.0728 Y=-40.8935 Z=0
    g24: GeomPoint X=61.5791 Y=-42.9683 Z=0
    g25: Circle CenterX=42.5666 CenterY=-67.3492 CenterZ=0 NormalX=0 NormalY=0 NormalZ=1 AngleXU=0 Radius=1
    g26: Circle CenterX=46.0728 CenterY=-65.424 CenterZ=0 NormalX=0 NormalY=0 NormalZ=1 AngleXU=0 Radius=1
    g27: Circle CenterX=46.0728 CenterY=-69.424 CenterZ=0 NormalX=0 NormalY=0 NormalZ=1 AngleXU=0 Radius=1
    g28: BSplineCurve PolesCount=3 KnotsCount=2 Degree=2 IsPeriodic=0
    g29: GeomPoint X=42.5666 Y=-67.3492 Z=0
    g30: GeomPoint X=46.0728 Y=-69.424 Z=0
    g31: Circle CenterX=2.07281 CenterY=-91.7794 CenterZ=0 NormalX=0 NormalY=0 NormalZ=1 AngleXU=0 Radius=1
    g32: Circle CenterX=-1.92719 CenterY=-91.7794 CenterZ=0 NormalX=0 NormalY=0 NormalZ=1 AngleXU=0 Radius=1
    g33: Circle CenterX=1.57905 CenterY=-89.8542 CenterZ=0 NormalX=0 NormalY=0 NormalZ=1 AngleXU=0 Radius=1
    g34: BSplineCurve PolesCount=3 KnotsCount=2 Degree=2 IsPeriodic=0
    g35: GeomPoint X=2.07281 Y=-91.7794 Z=0
    g36: GeomPoint X=1.57905 Y=-89.8542 Z=0
    g37: ArcOfCircle CenterX=-26.9272 CenterY=22.1087 CenterZ=0 NormalX=0 NormalY=0 NormalZ=1 AngleXU=0 Radius=4 StartAngle=5e-16 EndAngle=3.14159
    g38: Circle CenterX=-10.9272 CenterY=-78.7794 CenterZ=0 NormalX=0 NormalY=0 NormalZ=1 AngleXU=0 Radius=1
    g39: Circle CenterX=-10.9272 CenterY=-82.7794 CenterZ=0 NormalX=0 NormalY=0 NormalZ=1 AngleXU=0 Radius=1
    g40: Circle CenterX=-7.42095 CenterY=-80.8542 CenterZ=0 NormalX=0 NormalY=0 NormalZ=1 AngleXU=0 Radius=1
    g41: BSplineCurve PolesCount=3 KnotsCount=2 Degree=2 IsPeriodic=0
    g42: GeomPoint X=-10.9272 Y=-78.7794 Z=0
    g43: GeomPoint X=-7.42095 Y=-80.8542 Z=0
    g44: BSplineCurve PolesCount=3 KnotsCount=2 Degree=2 IsPeriodic=0
    g45: GeomPoint X=42.5666 Y=-53.4075 Z=0
    g46: GeomPoint X=46.0728 Y=-47.4823 Z=0
    g47: BSplineCurve PolesCount=5 KnotsCount=3 Degree=3 IsPeriodic=0
    g48: LineSegment StartX=124.814 StartY=-22.1885 StartZ=0 EndX=123.265 EndY=-19.3655 EndZ=0
    g49: ArcOfCircle CenterX=116.562 CenterY=-19.6236 CenterZ=0 NormalX=0 NormalY=0 NormalZ=1 AngleXU=0 Radius=4.24264 StartAngle=1.28753 EndAngle=6.00037
    g50: LineSegment StartX=-30.9272 StartY=22.1087 StartZ=0 EndX=-34.9272 EndY=-83.7794 EndZ=0
    g51: LineSegment StartX=-22.9272 StartY=22.1087 StartZ=0 EndX=-18.9272 EndY=-83.7794 EndZ=0
    g52: LineSegment StartX=118.934 StartY=-11.4765 StartZ=0 EndX=120.377 EndY=-14.1062 EndZ=0
    g53: LineSegment StartX=118.86 StartY=-31.3104 StartZ=0 EndX=120.377 EndY=-33.1447 EndZ=0
    g54: LineSegment StartX=115.291 StartY=-37.3514 StartZ=0 EndX=117.05 EndY=-39.4781 EndZ=0
    g55: LineSegment StartX=122.136 StartY=-35.2714 StartZ=0 EndX=123.656 EndY=-37.1092 EndZ=0
    g56: BSplineCurve PolesCount=3 KnotsCount=2 Degree=2 IsPeriodic=0
    g57: LineSegment StartX=132.072 StartY=-100.779 StartZ=0 EndX=132.072 EndY=-103.779 EndZ=0
    g58: LineSegment StartX=132.072 StartY=-91.8014 StartZ=0 EndX=132.072 EndY=-94.7791 EndZ=0
    g59: LineSegment StartX=63.9135 StartY=-91.8014 StartZ=0 EndX=132.072 EndY=-91.8014 EndZ=0
    g60: LineSegment StartX=61.6457 StartY=-88.8112 StartZ=0 EndX=123.656 EndY=-37.1092 EndZ=0
    g61: LineSegment StartX=122.136 StartY=-35.2714 StartZ=0 EndX=117.05 EndY=-39.4781 EndZ=0
    g62: LineSegment StartX=115.291 StartY=-37.3514 StartZ=0 EndX=120.377 EndY=-33.1447 EndZ=0
    g63: LineSegment StartX=118.86 StartY=-31.3104 StartZ=0 EndX=61.1496 EndY=-79.2541 EndZ=0
    g64: LineSegment StartX=58.0728 StartY=-77.8102 StartZ=0 EndX=58.0728 EndY=-62.8351 EndZ=0
    g65: LineSegment StartX=61.5791 StartY=-56.9099 StartZ=0 EndX=124.814 EndY=-22.1885 EndZ=0
    g66: LineSegment StartX=120.636 StartY=-20.8076 StartZ=0 EndX=123.265 EndY=-19.3655 EndZ=0
    g67: LineSegment StartX=117.748 StartY=-15.55 StartZ=0 EndX=120.377 EndY=-14.1062 EndZ=0
    g68: LineSegment StartX=118.934 StartY=-11.4765 StartZ=0 EndX=61.5791 EndY=-42.9683 EndZ=0
    g69: LineSegment StartX=-42.9272 StartY=-103.779 StartZ=0 EndX=132.072 EndY=-103.779 EndZ=0
    g70: LineSegment StartX=42.5666 StartY=-53.4075 StartZ=0 EndX=-7.42095 EndY=-80.8542 EndZ=0
    g71: LineSegment StartX=-10.9272 StartY=-78.7794 StartZ=0 EndX=-10.9272 EndY=48.2206 EndZ=0
    g72: LineSegment StartX=2.07281 StartY=-91.7794 StartZ=0 EndX=42.0728 EndY=-91.7794 EndZ=0
    g73: LineSegment StartX=46.0728 StartY=-87.7794 StartZ=0 EndX=46.0728 EndY=-69.424 EndZ=0
    g74: LineSegment StartX=42.5666 StartY=-67.3492 StartZ=0 EndX=1.57905 EndY=-89.8542 EndZ=0
    g75: LineSegment StartX=-42.9272 StartY=-103.779 StartZ=0 EndX=-42.9272 EndY=48.2206 EndZ=0
    g76: LineSegment StartX=-17.9272 StartY=48.2206 StartZ=0 EndX=-17.9272 EndY=58.2206 EndZ=0
    g77: LineSegment StartX=-35.9272 StartY=48.2206 StartZ=0 EndX=-35.9272 EndY=52.2206 EndZ=0
    g78: LineSegment StartX=-29.9272 StartY=48.2206 StartZ=0 EndX=-29.9272 EndY=52.2206 EndZ=0
    g79: LineSegment StartX=-23.9272 StartY=48.2206 StartZ=0 EndX=-23.9272 EndY=58.2206 EndZ=0
    g80: ArcOfCircle CenterX=-32.9272 CenterY=55.2206 CenterZ=0 NormalX=0 NormalY=0 NormalZ=1 AngleXU=0 Radius=4.24264 StartAngle=5.49779 EndAngle=10.2102
    g81: ArcOfCircle CenterX=-20.9272 CenterY=61.2206 CenterZ=0 NormalX=0 NormalY=0 NormalZ=1 AngleXU=0 Radius=4.24264 StartAngle=5.49779 EndAngle=10.2102
    g82: LineSegment StartX=-17.9272 StartY=48.2206 StartZ=0 EndX=-10.9272 EndY=48.2206 EndZ=0
    g83: LineSegment StartX=-42.9272 StartY=48.2206 StartZ=0 EndX=-35.9272 EndY=48.2206 EndZ=0
    g84: LineSegment StartX=50.0728 StartY=-27.5905 StartZ=0 EndX=50.0728 EndY=-31.5905 EndZ=0
    g85: LineSegment StartX=54.0728 StartY=-27.5905 StartZ=0 EndX=54.0728 EndY=-31.5905 EndZ=0
    g86: ArcOfCircle CenterX=52.0728 CenterY=-33.5905 CenterZ=0 NormalX=0 NormalY=0 NormalZ=1 AngleXU=0 Radius=2.82843 StartAngle=2.35619 EndAngle=7.06858
    g87: LineSegment StartX=46.0728 StartY=-27.5905 StartZ=0 EndX=50.0728 EndY=-27.5905 EndZ=0
    g88: LineSegment StartX=54.0728 StartY=-27.5905 StartZ=0 EndX=58.0728 EndY=-27.5905 EndZ=0
    g89: LineSegment StartX=46.0728 StartY=-27.5905 StartZ=0 EndX=46.0728 EndY=-47.4823 EndZ=0
    g90: LineSegment StartX=58.0728 StartY=-27.5905 StartZ=0 EndX=58.0728 EndY=-40.8935 EndZ=0
    g91: LineSegment StartX=-29.9272 StartY=48.2206 StartZ=0 EndX=-23.9272 EndY=48.2206 EndZ=0
  constraints (170):
    c: Weight(g1) = 1
    c: Equal(g1,g2)
    c: Equal(g1,g3)
    c: InternalAlignment(g1,g4)
    c: InternalAlignment(g2,g4)
    c: InternalAlignment(g3,g4)
    c: InternalAlignment(g5,g4)
    c: InternalAlignment(g6,g4)
    c: Weight(g7) = 1
    c: Equal(g7,g8)
    c: Equal(g7,g9)
    c: InternalAlignment(g7,g10)
    c: InternalAlignment(g8,g10)
    c: InternalAlignment(g9,g10)
    c: InternalAlignment(g11,g10)
    c: InternalAlignment(g12,g10)
    c: Block(g4)
    c: Block(g10)
    c: Weight(g13) = 1
    c: Equal(g13,g14)
    c: Equal(g13,g15)
    c: InternalAlignment(g13,g16)
    c: InternalAlignment(g14,g16)
    c: InternalAlignment(g15,g16)
    c: InternalAlignment(g17,g16)
    c: InternalAlignment(g18,g16)
    c: Block(g16)
    c: Weight(g19) = 1
    c: Equal(g19,g20)
    c: Equal(g19,g21)
    c: InternalAlignment(g19,g22)
    c: InternalAlignment(g20,g22)
    c: InternalAlignment(g21,g22)
    c: InternalAlignment(g23,g22)
    c: InternalAlignment(g24,g22)
    c: Block(g22)
    c: Weight(g25) = 1
    c: Equal(g25,g26)
    c: Equal(g25,g27)
    c: InternalAlignment(g25,g28)
    c: InternalAlignment(g26,g28)
    c: InternalAlignment(g27,g28)
    c: InternalAlignment(g29,g28)
    c: InternalAlignment(g30,g28)
    c: Weight(g31) = 1
    c: Equal(g31,g32)
    c: Equal(g31,g33)
    c: InternalAlignment(g31,g34)
    c: InternalAlignment(g32,g34)
    c: InternalAlignment(g33,g34)
    c: InternalAlignment(g35,g34)
    c: InternalAlignment(g36,g34)
    c: Block(g34)
    c: Block(g28)
    c: Block(g37)
    c: Block(g0)
    c: Weight(g38) = 1
    c: Equal(g38,g40)
    c: InternalAlignment(g38,g41)
    c: InternalAlignment(g39,g41)
    c: InternalAlignment(g40,g41)
    c: InternalAlignment(g42,g41)
    c: InternalAlignment(g43,g41)
    c: InternalAlignment(g45,g44)
    c: InternalAlignment(g46,g44)
    c: Block(g47)
    c: Block(g44)
    c: Block(g41)
    c: Block(g48)
    c: Block(g49)
    c: Coincident(g50,g37)
    c: Coincident(g50,g0)
    c: Coincident(g51,g37)
    c: Coincident(g51,g0)
    c: Block(g51)
    c: Block(g50)
    c: Block(g52)
    c: Block(g53)
    c: Block(g54)
    c: Block(g55)
    c: Block(g56)
    c: Coincident(g57,g47)
    c: Vertical(g57)
    c: Coincident(g58,g47)
    c: Vertical(g58)
    c: Coincident(g59,g16)
    c: Coincident(g59,g58)
    c: Horizontal(g59)
    c: Coincident(g60,g16)
    c: Coincident(g60,g55)
    c: Coincident(g61,g55)
    c: Coincident(g61,g54)
    c: Coincident(g62,g54)
    c: Coincident(g62,g53)
    c: Coincident(g63,g53)
    c: Coincident(g63,g10)
    c: Coincident(g64,g10)
    c: Coincident(g64,g4)
    c: Vertical(g64)
    c: Coincident(g65,g4)
    c: Coincident(g65,g48)
    c: Coincident(g66,g49)
    c: Coincident(g66,g48)
    c: Coincident(g67,g49)
    c: Coincident(g67,g52)
    c: Coincident(g68,g52)
    c: Coincident(g68,g22)
    c: Coincident(g69,g57)
    c: Horizontal(g69)
    c: Coincident(g70,g44)
    c: Coincident(g70,g41)
    c: Coincident(g71,g41)
    c: Vertical(g71)
    c: Coincident(g72,g34)
    c: Coincident(g72,g56)
    c: Horizontal(g72)
    c: Coincident(g73,g56)
    c: Coincident(g73,g28)
    c: Vertical(g73)
    c: Coincident(g74,g28)
    c: Coincident(g74,g34)
    c: Block(g69)
    c: Coincident(g75,g69)
    c: Vertical(g75)
    c: Distance(g75) = 152
    c: Block(g71)
    c: Vertical(g76)
    c: Distance(g76) = 10
    c: Vertical(g77)
    c: Distance(g77) = 4
    c: Vertical(g78)
    c: Distance(g78) = 4
    c: Vertical(g79)
    c: Distance(g79) = 10
    c: Coincident(g80,g78)
    c: Coincident(g80,g77)
    c: Block(g80)
    c: Coincident(g81,g79)
    c: Coincident(g81,g76)
    c: Block(g81)
    c: Coincident(g82,g76)
    c: Coincident(g82,g71)
    c: Horizontal(g82)
    c: Coincident(g83,g75)
    c: Coincident(g83,g77)
    c: Horizontal(g83)
    c: Distance(g83) = 7
    c: Distance(g82) = 7
    c: Vertical(g84)
    c: Distance(g84) = 4
    c: Vertical(g85)
    c: Distance(g85) = 4
    c: Coincident(g86,g84)
    c: Coincident(g86,g85)
    c: Block(g86)
    c: Coincident(g87,g84)
    c: Horizontal(g87)
    c: Distance(g87) = 4
    c: Coincident(g88,g85)
    c: Horizontal(g88)
    c: Distance(g88) = 4
    c: Coincident(g89,g87)
    c: Coincident(g89,g44)
    c: Vertical(g89)
    c: Coincident(g90,g88)
    c: Coincident(g90,g22)
    c: Vertical(g90)
    c: Coincident(g91,g78)
    c: Coincident(g91,g79)
    c: Horizontal(g91)
FEATURE [Sketcher::SketchObject] Sketch008  label="rightSideTop"
  FullyConstrained = false
  sketch-geometry (108):
    g0: Circle CenterX=302.996 CenterY=111.695 CenterZ=0 NormalX=0 NormalY=0 NormalZ=1 AngleXU=0 Radius=1
    g1: Circle CenterX=306.073 CenterY=114.251 CenterZ=0 NormalX=0 NormalY=0 NormalZ=1 AngleXU=0 Radius=1
    g2: Circle CenterX=306.073 CenterY=110.251 CenterZ=0 NormalX=0 NormalY=0 NormalZ=1 AngleXU=0 Radius=1
    g3: BSplineCurve PolesCount=3 KnotsCount=2 Degree=2 IsPeriodic=0
    g4: GeomPoint X=302.996 Y=111.695 Z=0
    g5: GeomPoint X=306.073 Y=110.251 Z=0
    g6: Circle CenterX=306.073 CenterY=95.2763 CenterZ=0 NormalX=0 NormalY=0 NormalZ=1 AngleXU=0 Radius=1
    g7: Circle CenterX=306.073 CenterY=91.2763 CenterZ=0 NormalX=0 NormalY=0 NormalZ=1 AngleXU=0 Radius=1
    g8: Circle CenterX=302.567 CenterY=89.3511 CenterZ=0 NormalX=0 NormalY=0 NormalZ=1 AngleXU=0 Radius=1
    g9: BSplineCurve PolesCount=3 KnotsCount=2 Degree=2 IsPeriodic=0
    g10: GeomPoint X=306.073 Y=95.2763 Z=0
    g11: GeomPoint X=302.567 Y=89.3511 Z=0
    g12: LineSegment StartX=306.073 StartY=110.251 StartZ=0 EndX=306.073 EndY=95.2763 EndZ=0
    g13: Circle CenterX=302.073 CenterY=124.221 CenterZ=0 NormalX=0 NormalY=0 NormalZ=1 AngleXU=0 Radius=1
    g14: Circle CenterX=306.073 CenterY=124.221 CenterZ=0 NormalX=0 NormalY=0 NormalZ=1 AngleXU=0 Radius=1
    g15: Circle CenterX=302.996 CenterY=121.665 CenterZ=0 NormalX=0 NormalY=0 NormalZ=1 AngleXU=0 Radius=1
    g16: BSplineCurve PolesCount=3 KnotsCount=2 Degree=2 IsPeriodic=0
    g17: GeomPoint X=302.073 Y=124.221 Z=0
    g18: GeomPoint X=302.996 Y=121.665 Z=0
    g19: Circle CenterX=306.073 CenterY=73.3346 CenterZ=0 NormalX=0 NormalY=0 NormalZ=1 AngleXU=0 Radius=1
    g20: Circle CenterX=306.073 CenterY=77.3346 CenterZ=0 NormalX=0 NormalY=0 NormalZ=1 AngleXU=0 Radius=1
    g21: Circle CenterX=302.535 CenterY=75.4095 CenterZ=0 NormalX=0 NormalY=0 NormalZ=1 AngleXU=0 Radius=1
    g22: BSplineCurve PolesCount=3 KnotsCount=2 Degree=2 IsPeriodic=0
    g23: GeomPoint X=306.073 Y=73.3346 Z=0
    g24: GeomPoint X=302.535 Y=75.4095 Z=0
    g25: Circle CenterX=362.073 CenterY=124.221 CenterZ=0 NormalX=0 NormalY=0 NormalZ=1 AngleXU=0 Radius=1
    g26: Circle CenterX=366.073 CenterY=124.221 CenterZ=0 NormalX=0 NormalY=0 NormalZ=1 AngleXU=0 Radius=1
    g27: Circle CenterX=362.567 CenterY=122.294 CenterZ=0 NormalX=0 NormalY=0 NormalZ=1 AngleXU=0 Radius=1
    g28: BSplineCurve PolesCount=3 KnotsCount=2 Degree=2 IsPeriodic=0
    g29: GeomPoint X=362.073 Y=124.221 Z=0
    g30: GeomPoint X=362.567 Y=122.294 Z=0
    g31: Circle CenterX=322.073 CenterY=124.221 CenterZ=0 NormalX=0 NormalY=0 NormalZ=1 AngleXU=0 Radius=1
    g32: Circle CenterX=318.073 CenterY=124.221 CenterZ=0 NormalX=0 NormalY=0 NormalZ=1 AngleXU=0 Radius=1
    g33: Circle CenterX=318.073 CenterY=120.221 CenterZ=0 NormalX=0 NormalY=0 NormalZ=1 AngleXU=0 Radius=1
    g34: BSplineCurve PolesCount=3 KnotsCount=2 Degree=2 IsPeriodic=0
    g35: GeomPoint X=322.073 Y=124.221 Z=0
    g36: GeomPoint X=318.073 Y=120.221 Z=0
    g37: Circle CenterX=322.073 CenterY=105.865 CenterZ=0 NormalX=0 NormalY=0 NormalZ=1 AngleXU=0 Radius=1
    g38: Circle CenterX=318.073 CenterY=105.865 CenterZ=0 NormalX=0 NormalY=0 NormalZ=1 AngleXU=0 Radius=1
    g39: Circle CenterX=318.073 CenterY=109.865 CenterZ=0 NormalX=0 NormalY=0 NormalZ=1 AngleXU=0 Radius=1
    g40: BSplineCurve PolesCount=3 KnotsCount=2 Degree=2 IsPeriodic=0
    g41: GeomPoint X=322.073 Y=105.865 Z=0
    g42: GeomPoint X=318.073 Y=109.865 Z=0
    g43: Circle CenterX=336.157 CenterY=107.779 CenterZ=0 NormalX=0 NormalY=0 NormalZ=1 AngleXU=0 Radius=1
    g44: Circle CenterX=332.651 CenterY=105.853 CenterZ=0 NormalX=0 NormalY=0 NormalZ=1 AngleXU=0 Radius=1
    g45: Circle CenterX=328.643 CenterY=105.865 CenterZ=0 NormalX=0 NormalY=0 NormalZ=1 AngleXU=0 Radius=1
    g46: BSplineCurve PolesCount=3 KnotsCount=2 Degree=2 IsPeriodic=0
    g47: GeomPoint X=336.157 Y=107.779 Z=0
    g48: GeomPoint X=328.643 Y=105.865 Z=0
    g49: Circle CenterX=322.073 CenterY=76.4095 CenterZ=0 NormalX=0 NormalY=0 NormalZ=1 AngleXU=0 Radius=4
    g50: BSplineCurve PolesCount=3 KnotsCount=2 Degree=2 IsPeriodic=0
    g51: GeomPoint X=318.073 Y=72.4095 Z=0
    g52: GeomPoint X=322.073 Y=76.4095 Z=0
    g53: Circle CenterX=375.073 CenterY=72.4095 CenterZ=0 NormalX=0 NormalY=0 NormalZ=1 AngleXU=0 Radius=1
    g54: Circle CenterX=375.073 CenterY=76.4095 CenterZ=0 NormalX=0 NormalY=0 NormalZ=1 AngleXU=0 Radius=1
    g55: Circle CenterX=371.073 CenterY=76.4095 CenterZ=0 NormalX=0 NormalY=0 NormalZ=1 AngleXU=0 Radius=1
    g56: BSplineCurve PolesCount=3 KnotsCount=2 Degree=2 IsPeriodic=0
    g57: GeomPoint X=375.073 Y=72.4095 Z=0
    g58: GeomPoint X=371.073 Y=76.4095 Z=0
    g59: LineSegment StartX=322.073 StartY=76.4095 StartZ=0 EndX=371.073 EndY=76.4095 EndZ=0
    g60: Circle CenterX=232.072 CenterY=133.221 CenterZ=0 NormalX=0 NormalY=0 NormalZ=1 AngleXU=0 Radius=1
    g61: Circle CenterX=226.072 CenterY=136.221 CenterZ=0 NormalX=0 NormalY=0 NormalZ=1 AngleXU=0 Radius=1
    g62: Circle CenterX=226.072 CenterY=124.221 CenterZ=0 NormalX=0 NormalY=0 NormalZ=1 AngleXU=0 Radius=1
    g63: Circle CenterX=232.072 CenterY=127.221 CenterZ=0 NormalX=0 NormalY=0 NormalZ=1 AngleXU=0 Radius=1
    g64: BSplineCurve PolesCount=5 KnotsCount=3 Degree=3 IsPeriodic=0
    g65: GeomPoint X=232.072 Y=133.221 Z=0
    g66: GeomPoint X=223.072 Y=130.221 Z=0
    g67: GeomPoint X=232.072 Y=127.221 Z=0
    g68: LineSegment StartX=240.687 StartY=51.8263 StartZ=0 EndX=243.317 EndY=53.2701 EndZ=0
    g69: LineSegment StartX=243.575 StartY=46.5669 StartZ=0 EndX=246.205 EndY=48.0108 EndZ=0
    g70: ArcOfCircle CenterX=247.391 CenterY=52.0843 CenterZ=0 NormalX=0 NormalY=0 NormalZ=1 AngleXU=0 Radius=4.24264 StartAngle=4.42912 EndAngle=9.14151
    g71: LineSegment StartX=243.475 StartY=65.4951 StartZ=0 EndX=245.073 EndY=63.5726 EndZ=0
    g72: LineSegment StartX=243.575 StartY=46.5669 StartZ=0 EndX=245.072 EndY=43.8408 EndZ=0
    g73: LineSegment StartX=245.072 StartY=43.8408 StartZ=0 EndX=302.535 EndY=75.4095 EndZ=0
    g74: LineSegment StartX=239.192 StartY=54.5542 StartZ=0 EndX=302.567 EndY=89.3511 EndZ=0
    g75: LineSegment StartX=232.072 StartY=127.221 StartZ=0 EndX=232.072 EndY=124.221 EndZ=0
    g76: LineSegment StartX=232.072 StartY=136.221 StartZ=0 EndX=232.072 EndY=133.221 EndZ=0
    g77: LineSegment StartX=232.072 StartY=136.221 StartZ=0 EndX=407.073 EndY=136.221 EndZ=0
    g78: LineSegment StartX=322.073 StartY=124.221 StartZ=0 EndX=362.073 EndY=124.221 EndZ=0
    g79: LineSegment StartX=362.567 StartY=122.294 StartZ=0 EndX=336.157 EndY=107.779 EndZ=0
    g80: LineSegment StartX=322.073 StartY=105.865 StartZ=0 EndX=328.643 EndY=105.865 EndZ=0
    g81: LineSegment StartX=318.073 StartY=120.221 StartZ=0 EndX=318.073 EndY=109.865 EndZ=0
    g82: LineSegment StartX=232.072 StartY=124.221 StartZ=0 EndX=302.073 EndY=124.221 EndZ=0
    g83: LineSegment StartX=302.996 StartY=121.665 StartZ=0 EndX=240.171 EndY=69.471 EndZ=0
    g84: LineSegment StartX=240.171 StartY=69.471 StartZ=0 EndX=241.711 EndY=67.6177 EndZ=0
    g85: LineSegment StartX=241.711 StartY=67.6177 StartZ=0 EndX=246.787 EndY=71.8365 EndZ=0
    g86: LineSegment StartX=246.787 StartY=71.8365 StartZ=0 EndX=248.551 EndY=69.712 EndZ=0
    g87: LineSegment StartX=248.551 StartY=69.712 StartZ=0 EndX=243.475 EndY=65.4951 EndZ=0
    g88: LineSegment StartX=245.073 StartY=63.5726 StartZ=0 EndX=302.996 EndY=111.695 EndZ=0
    g89: LineSegment StartX=239.192 StartY=54.5542 StartZ=0 EndX=240.687 EndY=51.8263 EndZ=0
    g90: LineSegment StartX=375.073 StartY=48.2206 StartZ=0 EndX=382.073 EndY=48.2206 EndZ=0
    g91: LineSegment StartX=407.073 StartY=48.2206 StartZ=0 EndX=400.073 EndY=48.2206 EndZ=0
    g92: LineSegment StartX=394.073 StartY=48.2206 StartZ=0 EndX=394.073 EndY=52.2206 EndZ=0
    g93: LineSegment StartX=388.073 StartY=48.2206 StartZ=0 EndX=388.073 EndY=58.2206 EndZ=0
    g94: ArcOfCircle CenterX=385.073 CenterY=61.2206 CenterZ=0 NormalX=0 NormalY=0 NormalZ=1 AngleXU=0 Radius=4.24264 StartAngle=5.49779 EndAngle=10.2102
    g95: ArcOfCircle CenterX=397.073 CenterY=55.2206 CenterZ=0 NormalX=0 NormalY=0 NormalZ=1 AngleXU=0 Radius=4.24264 StartAngle=5.49779 EndAngle=10.2102
    g96: LineSegment StartX=382.073 StartY=58.2206 StartZ=0 EndX=382.073 EndY=48.2206 EndZ=0
    g97: LineSegment StartX=400.073 StartY=52.2206 StartZ=0 EndX=400.073 EndY=48.2206 EndZ=0
    g98: LineSegment StartX=394.073 StartY=48.2206 StartZ=0 EndX=388.073 EndY=48.2206 EndZ=0
    g99: LineSegment StartX=306.073 StartY=-27.5935 StartZ=0 EndX=310.073 EndY=-27.5935 EndZ=0
    g100: LineSegment StartX=318.073 StartY=-27.5935 StartZ=0 EndX=314.073 EndY=-27.5935 EndZ=0
    g101: LineSegment StartX=310.073 StartY=-27.5935 StartZ=0 EndX=310.073 EndY=-31.5935 EndZ=0
    g102: LineSegment StartX=314.073 StartY=-27.5935 StartZ=0 EndX=314.073 EndY=-31.5935 EndZ=0
    g103: ArcOfCircle CenterX=312.073 CenterY=-33.5935 CenterZ=0 NormalX=0 NormalY=0 NormalZ=1 AngleXU=0 Radius=2.82843 StartAngle=2.35619 EndAngle=7.06858
    g104: LineSegment StartX=375.073 StartY=72.4095 StartZ=0 EndX=375.073 EndY=48.2206 EndZ=0
    g105: LineSegment StartX=407.073 StartY=48.2206 StartZ=0 EndX=407.073 EndY=136.221 EndZ=0
    g106: LineSegment StartX=318.073 StartY=-27.5935 StartZ=0 EndX=318.073 EndY=72.4095 EndZ=0
    g107: LineSegment StartX=306.073 StartY=73.3346 StartZ=0 EndX=306.073 EndY=-27.5935 EndZ=0
  constraints (136):
    c: Weight(g0) = 1
    c: Equal(g0,g1)
    c: Equal(g0,g2)
    c: InternalAlignment(g0,g3)
    c: InternalAlignment(g1,g3)
    c: InternalAlignment(g2,g3)
    c: InternalAlignment(g4,g3)
    c: InternalAlignment(g5,g3)
    c: Weight(g6) = 1
    c: Equal(g6,g7)
    c: Equal(g6,g8)
    c: InternalAlignment(g6,g9)
    c: InternalAlignment(g7,g9)
    c: InternalAlignment(g8,g9)
    c: InternalAlignment(g10,g9)
    c: InternalAlignment(g11,g9)
    c: Block(g3)
    c: Block(g9)
    c: Coincident(g12,g3)
    c: Coincident(g12,g9)
    c: Vertical(g12)
    c: Weight(g13) = 1
    c: Equal(g13,g14)
    c: Equal(g13,g15)
    c: InternalAlignment(g14,g16)
    c: InternalAlignment(g15,g16)
    c: InternalAlignment(g17,g16)
    c: InternalAlignment(g18,g16)
    c: Block(g71)
    c: Block(g72)
    c: Coincident(g73,g72)
    c: Coincident(g73,g22)
    c: Block(g73)
    c: Coincident(g70,g69)
    c: Coincident(g70,g68)
    c: Coincident(g74,g9)
    c: Block(g74)
    c: Distance(g71) = 2.5
    c: Block(g64)
    c: Block(g46)
    c: Block(g59)
    c: Coincident(g75,g64)
    c: Vertical(g75)
    c: Coincident(g76,g64)
    c: Vertical(g76)
    c: Coincident(g77,g76)
    c: Horizontal(g77)
    c: Coincident(g78,g34)
    c: Coincident(g78,g28)
    c: Horizontal(g78)
    c: Coincident(g79,g28)
    c: Coincident(g79,g46)
    c: Coincident(g80,g40)
    c: Coincident(g80,g46)
    c: Horizontal(g80)
    c: Coincident(g81,g34)
    c: Coincident(g81,g40)
    c: Vertical(g81)
    c: Block(g34)
    c: Block(g40)
    c: Block(g28)
    c: Coincident(g82,g75)
    c: Coincident(g82,g16)
    c: Horizontal(g82)
    c: Coincident(g83,g16)
    c: Block(g82)
    c: Block(g83)
    c: Block(g16)
    c: Coincident(g84,g83)
    c: Block(g84)
    c: Coincident(g85,g84)
    c: Block(g85)
    c: Coincident(g86,g85)
    c: Coincident(g87,g86)
    c: Coincident(g87,g71)
    c: Block(g87)
    c: Coincident(g88,g71)
    c: Coincident(g88,g3)
    c: Block(g88)
    c: Coincident(g89,g74)
    c: Coincident(g89,g68)
    c: Block(g70)
    c: Block(g68)
    c: Block(g69)
    c: Block(g22)
    c: Block(g50)
    c: Block(g56)
    c: Horizontal(g90)
    c: Distance(g90) = 7
    c: Horizontal(g91)
    c: Distance(g91) = 7
    c: Vertical(g92)
    c: Distance(g92) = 4
    c: Vertical(g93)
    c: Distance(g93) = 10
    c: Coincident(g94,g93)
    c: Coincident(g95,g92)
    c: Block(g95)
    c: Block(g94)
    c: Coincident(g96,g94)
    c: Coincident(g96,g90)
    c: Vertical(g96)
    c: Coincident(g97,g95)
    c: Coincident(g97,g91)
    c: Vertical(g97)
    c: Coincident(g98,g92)
    c: Coincident(g98,g93)
    c: Horizontal(g98)
    c: Horizontal(g99)
    c: Distance(g99) = 4
    c: Horizontal(g100)
    c: Distance(g100) = 4
    c: Coincident(g101,g99)
    c: Vertical(g101)
    c: Coincident(g102,g100)
    c: Vertical(g102)
    c: Distance(g101) = 4
    c: Distance(g102) = 4
    c: Coincident(g103,g101)
    c: Coincident(g103,g102)
    c: Block(g103)
    c: Coincident(g104,g56)
    c: Coincident(g104,g90)
    c: Vertical(g104)
    c: Block(g104)
    c: Coincident(g105,g91)
    c: Coincident(g105,g77)
    c: Vertical(g105)
    c: Block(g77)
    c: Block(g105)
    c: Coincident(g106,g100)
    c: Coincident(g106,g50)
    c: Vertical(g106)
    c: Coincident(g107,g22)
    c: Coincident(g107,g99)
    c: Vertical(g107)
FEATURE [Sketcher::SketchObject] Sketch009  label="middleBottom"
  FullyConstrained = true
  sketch-geometry (109):
    g0: Circle CenterX=175.022 CenterY=5.37834 CenterZ=0 NormalX=0 NormalY=0 NormalZ=1 AngleXU=0 Radius=1
    g1: Circle CenterX=179.022 CenterY=7.57463 CenterZ=0 NormalX=0 NormalY=0 NormalZ=1 AngleXU=0 Radius=1
    g2: Circle CenterX=179.022 CenterY=5.34704 CenterZ=0 NormalX=0 NormalY=0 NormalZ=1 AngleXU=0 Radius=1
    g3: BSplineCurve PolesCount=3 KnotsCount=2 Degree=2 IsPeriodic=0
    g4: GeomPoint X=175.022 Y=5.37834 Z=0
    g5: GeomPoint X=179.022 Y=5.34704 Z=0
    g6: Circle CenterX=189.124 CenterY=5.37834 CenterZ=0 NormalX=0 NormalY=0 NormalZ=1 AngleXU=0 Radius=1
    g7: Circle CenterX=185.124 CenterY=7.57463 CenterZ=0 NormalX=0 NormalY=0 NormalZ=1 AngleXU=0 Radius=1
    g8: Circle CenterX=185.124 CenterY=5.34704 CenterZ=0 NormalX=0 NormalY=0 NormalZ=1 AngleXU=0 Radius=1
    g9: BSplineCurve PolesCount=3 KnotsCount=2 Degree=2 IsPeriodic=0
    g10: GeomPoint X=189.124 Y=5.37834 Z=0
    g11: GeomPoint X=185.124 Y=5.34704 Z=0
    g12: Circle CenterX=224.513 CenterY=-14.0532 CenterZ=0 NormalX=0 NormalY=0 NormalZ=1 AngleXU=0 Radius=1
    g13: Circle CenterX=236.584 CenterY=-24.2775 CenterZ=0 NormalX=0 NormalY=0 NormalZ=1 AngleXU=0 Radius=1
    g14: BSplineCurve PolesCount=3 KnotsCount=2 Degree=2 IsPeriodic=0
    g15: GeomPoint X=236.584 Y=-24.2775 Z=0
    g16: Circle CenterX=125.607 CenterY=-21.7539 CenterZ=0 NormalX=0 NormalY=0 NormalZ=1 AngleXU=0 Radius=1
    g17: Circle CenterX=139.632 CenterY=-14.0532 CenterZ=0 NormalX=0 NormalY=0 NormalZ=1 AngleXU=0 Radius=1
    g18: Circle CenterX=127.325 CenterY=-24.2775 CenterZ=0 NormalX=0 NormalY=0 NormalZ=1 AngleXU=0 Radius=1
    g19: BSplineCurve PolesCount=3 KnotsCount=2 Degree=2 IsPeriodic=0
    g20: GeomPoint X=125.607 Y=-21.7539 Z=0
    g21: GeomPoint X=127.325 Y=-24.2775 Z=0
    g22: Circle CenterX=179.022 CenterY=-85.8163 CenterZ=0 NormalX=0 NormalY=0 NormalZ=1 AngleXU=0 Radius=1
    g23: Circle CenterX=179.022 CenterY=-91.7794 CenterZ=0 NormalX=0 NormalY=0 NormalZ=1 AngleXU=0 Radius=1
    g24: Circle CenterX=171.895 CenterY=-91.8014 CenterZ=0 NormalX=0 NormalY=0 NormalZ=1 AngleXU=0 Radius=1
    g25: BSplineCurve PolesCount=3 KnotsCount=2 Degree=2 IsPeriodic=0
    g26: GeomPoint X=179.022 Y=-85.8163 Z=0
    g27: GeomPoint X=171.895 Y=-91.8014 Z=0
    g28: Circle CenterX=185.124 CenterY=-86.2028 CenterZ=0 NormalX=0 NormalY=0 NormalZ=1 AngleXU=0 Radius=1
    g29: Circle CenterX=185.124 CenterY=-91.7794 CenterZ=0 NormalX=0 NormalY=0 NormalZ=1 AngleXU=0 Radius=1
    g30: Circle CenterX=191.747 CenterY=-91.7794 CenterZ=0 NormalX=0 NormalY=0 NormalZ=1 AngleXU=0 Radius=1
    g31: BSplineCurve PolesCount=3 KnotsCount=2 Degree=2 IsPeriodic=0
    g32: GeomPoint X=185.124 Y=-86.2028 Z=0
    g33: GeomPoint X=191.747 Y=-91.7794 Z=0
    g34: BSplineCurve PolesCount=5 KnotsCount=3 Degree=3 IsPeriodic=0
    g35: LineSegment StartX=132.072 StartY=-100.779 StartZ=0 EndX=132.072 EndY=-103.779 EndZ=0
    g36: GeomPoint X=232.072 Y=-94.7794 Z=0
    g37: GeomPoint X=223.072 Y=-97.7794 Z=0
    g38: Circle CenterX=232.072 CenterY=-94.7794 CenterZ=0 NormalX=0 NormalY=0 NormalZ=1 AngleXU=0 Radius=1
    g39: Circle CenterX=232.072 CenterY=-100.779 CenterZ=0 NormalX=0 NormalY=0 NormalZ=1 AngleXU=0 Radius=1
    g40: BSplineCurve PolesCount=5 KnotsCount=3 Degree=3 IsPeriodic=0
    g41: GeomPoint X=232.072 Y=-100.779 Z=0
    g42: LineSegment StartX=123.656 StartY=-37.1092 StartZ=0 EndX=122.136 EndY=-35.2714 EndZ=0
    g43: LineSegment StartX=117.05 StartY=-39.4781 StartZ=0 EndX=115.291 EndY=-37.3514 EndZ=0
    g44: LineSegment StartX=120.377 StartY=-33.1447 StartZ=0 EndX=118.86 EndY=-31.3104 EndZ=0
    g45: ArcOfCircle CenterX=116.562 CenterY=-19.6236 CenterZ=0 NormalX=0 NormalY=0 NormalZ=1 AngleXU=0 Radius=4.24264 StartAngle=1.28753 EndAngle=5.99992
    g46: LineSegment StartX=240.266 StartY=-37.1092 StartZ=0 EndX=189.124 EndY=5.37834 EndZ=0
    g47: LineSegment StartX=191.747 StartY=-91.7794 StartZ=0 EndX=232.072 EndY=-91.7794 EndZ=0
    g48: LineSegment StartX=232.072 StartY=-91.7794 StartZ=0 EndX=232.072 EndY=-94.7794 EndZ=0
    g49: LineSegment StartX=232.072 StartY=-100.779 StartZ=0 EndX=232.072 EndY=-103.779 EndZ=0
    g50: LineSegment StartX=132.072 StartY=-103.779 StartZ=0 EndX=232.072 EndY=-103.779 EndZ=0
    g51: LineSegment StartX=132.072 StartY=-91.8014 StartZ=0 EndX=132.072 EndY=-94.7791 EndZ=0
    g52: LineSegment StartX=132.072 StartY=-91.8014 StartZ=0 EndX=171.895 EndY=-91.8014 EndZ=0
    g53: LineSegment StartX=179.022 StartY=-85.8163 StartZ=0 EndX=179.022 EndY=5.34704 EndZ=0
    g54: LineSegment StartX=175.022 StartY=5.37834 StartZ=0 EndX=123.656 EndY=-37.1092 EndZ=0
    g55: LineSegment StartX=185.124 StartY=5.34704 StartZ=0 EndX=185.124 EndY=-86.2028 EndZ=0
    g56: LineSegment StartX=122.136 StartY=-35.2714 StartZ=0 EndX=117.05 EndY=-39.4781 EndZ=0
    g57: LineSegment StartX=115.291 StartY=-37.3514 StartZ=0 EndX=120.377 EndY=-33.1447 EndZ=0
    g58: LineSegment StartX=118.86 StartY=-31.3104 StartZ=0 EndX=127.325 EndY=-24.2775 EndZ=0
    g59: LineSegment StartX=125.607 StartY=-21.7539 StartZ=0 EndX=124.815 EndY=-22.1887 EndZ=0
    g60: LineSegment StartX=123.265 StartY=-19.3655 StartZ=0 EndX=124.815 EndY=-22.1887 EndZ=0
    g61: LineSegment StartX=120.636 StartY=-20.8094 StartZ=0 EndX=123.265 EndY=-19.3655 EndZ=0
    g62: LineSegment StartX=117.748 StartY=-15.55 StartZ=0 EndX=120.377 EndY=-14.1062 EndZ=0
    g63: LineSegment StartX=120.377 StartY=-14.1062 StartZ=0 EndX=118.934 EndY=-11.4765 EndZ=0
    g64: LineSegment StartX=236.584 StartY=-24.2775 StartZ=0 EndX=245.072 EndY=-31.3037 EndZ=0
    g65: LineSegment StartX=245.072 StartY=-31.3037 StartZ=0 EndX=243.535 EndY=-33.1602 EndZ=0
    g66: LineSegment StartX=243.535 StartY=-33.1602 StartZ=0 EndX=248.619 EndY=-37.3688 EndZ=0
    g67: LineSegment StartX=248.619 StartY=-37.3688 StartZ=0 EndX=246.855 EndY=-39.5064 EndZ=0
    g68: LineSegment StartX=246.855 StartY=-39.5064 StartZ=0 EndX=241.778 EndY=-35.2889 EndZ=0
    g69: LineSegment StartX=241.778 StartY=-35.2889 StartZ=0 EndX=240.266 EndY=-37.1092 EndZ=0
    g70: LineSegment StartX=243.628 StartY=-14.0323 StartZ=0 EndX=246.258 EndY=-15.476 EndZ=0
    g71: LineSegment StartX=240.741 StartY=-19.2917 StartZ=0 EndX=243.37 EndY=-20.7355 EndZ=0
    g72: ArcOfCircle CenterX=247.444 CenterY=-19.5496 CenterZ=0 NormalX=0 NormalY=0 NormalZ=1 AngleXU=0 Radius=4.24264 StartAngle=3.4249 EndAngle=8.13729
    g73: LineSegment StartX=240.741 StartY=-19.2917 StartZ=0 EndX=239.201 EndY=-22.0968 EndZ=0
    g74: LineSegment StartX=238.538 StartY=-21.7516 StartZ=0 EndX=239.201 EndY=-22.0968 EndZ=0
    g75: LineSegment StartX=245.072 StartY=-11.4025 StartZ=0 EndX=243.628 EndY=-14.0323 EndZ=0
    g76-g91: Circle x16 (B-spline internal-alignment scaffolding for g92; pole/knot coordinates omitted)
    g92: BSplineCurve PolesCount=16 KnotsCount=14 Degree=3 IsPeriodic=0
    g93-g106: GeomPoint x14 (B-spline internal-alignment scaffolding for g92; pole/knot coordinates omitted)
    g107: LineSegment StartX=165.871 StartY=14.2956 StartZ=0 EndX=118.934 EndY=-11.4765 EndZ=0
    g108: LineSegment StartX=198.264 StartY=14.2963 StartZ=0 EndX=245.072 EndY=-11.4025 EndZ=0
  constraints (146):
    c: Weight(g0) = 1
    c: Equal(g0,g1)
    c: Equal(g0,g2)
    c: InternalAlignment(g0,g3)
    c: InternalAlignment(g1,g3)
    c: InternalAlignment(g2,g3)
    c: InternalAlignment(g4,g3)
    c: InternalAlignment(g5,g3)
    c: Weight(g6) = 1
    c: Equal(g6,g7)
    c: Equal(g6,g8)
    c: InternalAlignment(g6,g9)
    c: InternalAlignment(g7,g9)
    c: InternalAlignment(g8,g9)
    c: InternalAlignment(g10,g9)
    c: InternalAlignment(g11,g9)
    c: Block(g9)
    c: Block(g3)
    c: InternalAlignment(g12,g14)
    c: InternalAlignment(g13,g14)
    c: InternalAlignment(g15,g14)
    c: Block(g14)
    c: Weight(g16) = 1
    c: Equal(g16,g17)
    c: Equal(g16,g18)
    c: InternalAlignment(g16,g19)
    c: InternalAlignment(g17,g19)
    c: InternalAlignment(g18,g19)
    c: InternalAlignment(g20,g19)
    c: InternalAlignment(g21,g19)
    c: Block(g19)
    c: Weight(g22) = 1
    c: Equal(g22,g23)
    c: Equal(g22,g24)
    c: InternalAlignment(g22,g25)
    c: InternalAlignment(g23,g25)
    c: InternalAlignment(g24,g25)
    c: InternalAlignment(g26,g25)
    c: InternalAlignment(g27,g25)
    c: Weight(g28) = 1
    c: Equal(g28,g29)
    c: Equal(g28,g30)
    c: InternalAlignment(g28,g31)
    c: InternalAlignment(g29,g31)
    c: InternalAlignment(g30,g31)
    c: InternalAlignment(g32,g31)
    c: InternalAlignment(g33,g31)
    c: Block(g31)
    c: Block(g25)
    c: Block(g34)
    c: Coincident(g35,g34)
    c: Vertical(g35)
    c: Block(g35)
    c: Equal(g38,g39)
    c: InternalAlignment(g38,g40)
    c: InternalAlignment(g39,g40)
    c: InternalAlignment(g36,g40)
    c: InternalAlignment(g37,g40)
    c: InternalAlignment(g41,g40)
    c: Block(g40)
    c: Distance(g42) = 2.385
    c: Distance(g43) = 2.76
    c: Parallel(g42,g44)
    c: Block(g45)
    c: Coincident(g46,g9)
    c: Coincident(g47,g31)
    c: Horizontal(g47)
    c: Block(g47)
    c: Coincident(g48,g47)
    c: Coincident(g48,g40)
    c: Vertical(g48)
    c: Block(g48)
    c: Coincident(g49,g40)
    c: Vertical(g49)
    c: Block(g49)
    c: Coincident(g50,g35)
    c: Coincident(g50,g49)
    c: Horizontal(g50)
    c: Block(g50)
    c: Coincident(g51,g34)
    c: Vertical(g51)
    c: Coincident(g52,g51)
    c: Coincident(g52,g25)
    c: Horizontal(g52)
    c: Coincident(g53,g25)
    c: Coincident(g53,g3)
    c: Vertical(g53)
    c: Coincident(g54,g3)
    c: Coincident(g54,g42)
    c: Coincident(g55,g9)
    c: Coincident(g55,g31)
    c: Vertical(g55)
    c: Block(g42)
    c: Coincident(g56,g42)
    c: Coincident(g56,g43)
    c: Coincident(g57,g43)
    c: Coincident(g57,g44)
    c: Block(g57)
    c: Block(g56)
    c: Coincident(g58,g44)
    c: Coincident(g58,g19)
    c: Block(g58)
    c: Coincident(g59,g19)
    c: Block(g59)
    c: Coincident(g60,g59)
    c: Block(g60)
    c: Coincident(g61,g45)
    c: Coincident(g61,g60)
    c: Coincident(g62,g45)
    c: Coincident(g63,g62)
    c: Block(g63)
    c: Coincident(g64,g14)
    c: Block(g64)
    c: Coincident(g65,g64)
    c: Coincident(g66,g65)
    c: Coincident(g67,g66)
    c: Coincident(g68,g67)
    c: Coincident(g69,g68)
    c: Coincident(g69,g46)
    c: Block(g46)
    c: Block(g68)
    c: Block(g66)
    c: Distance(g70) = 3
    c: Distance(g71) = 3
    c: Coincident(g72,g70)
    c: Coincident(g72,g71)
    c: Block(g72)
    c: Coincident(g73,g71)
    c: Distance(g73) = 3.2
    c: Coincident(g74,g14)
    c: Coincident(g74,g73)
    c: Coincident(g75,g70)
    c: Block(g75)
    c: Block(g73)
    c: Distance(g63) = 3
    c: Distance(g60) = 3.22077
    c: Weight(g76) = 1
    c: Equal(g76, g77-g91) x15
    c: InternalAlignment(g76-g91 -> g92) x16
    c: InternalAlignment(g93-g106 -> g92) x14
    c: Coincident(g107,g92)
    c: Coincident(g107,g63)
    c: Block(g107)
    c: Block(g92)
    c: Coincident(g108,g92)
    c: Coincident(g108,g75)
FEATURE [Sketcher::SketchObject] Sketch010  label="legBottom"
  FullyConstrained = false
  MapMode = 4
  Placement = pos=(0,0,0) rot=(0.57735,0.57735,0.57735;2.0944rad)
  sketch-geometry (44):
    g0: BSplineCurve PolesCount=3 KnotsCount=2 Degree=2 IsPeriodic=0
    g1: Circle CenterX=-199.665 CenterY=-138.314 CenterZ=0 NormalX=0 NormalY=0 NormalZ=1 AngleXU=0 Radius=1
    g2: GeomPoint X=-199.665 Y=-138.314 Z=0
    g3: LineSegment StartX=-199.665 StartY=-138.314 StartZ=0 EndX=-200.721 EndY=-141.122 EndZ=0
    g4: Circle CenterX=-17.0256 CenterY=-190.268 CenterZ=0 NormalX=0 NormalY=0 NormalZ=1 AngleXU=0 Radius=10.5072
    g5: Circle CenterX=-37.7758 CenterY=-187.672 CenterZ=0 NormalX=0 NormalY=0 NormalZ=1 AngleXU=0 Radius=5.64388
    g6: Circle CenterX=-51.4606 CenterY=-185.091 CenterZ=0 NormalX=0 NormalY=0 NormalZ=1 AngleXU=0 Radius=3.01653
    g7: Circle CenterX=-60.4835 CenterY=-182.688 CenterZ=0 NormalX=0 NormalY=0 NormalZ=1 AngleXU=0 Radius=2.12826
    g8: Circle CenterX=-3.29005 CenterY=-177.662 CenterZ=0 NormalX=0 NormalY=0 NormalZ=1 AngleXU=0 Radius=3.26661
    g9: ArcOfCircle CenterX=11.0205 CenterY=-198.019 CenterZ=0 NormalX=0 NormalY=0 NormalZ=1 AngleXU=0 Radius=13 StartAngle=2.78068 EndAngle=5.92131
    g10: LineSegment StartX=5.08312 StartY=-176.581 StartZ=0 EndX=-1.14188 EndY=-193.429 EndZ=0
    g11: ArcOfCircle CenterX=17.2475 CenterY=-181.166 CenterZ=0 NormalX=0 NormalY=0 NormalZ=1 AngleXU=0 Radius=13 StartAngle=1.21042 EndAngle=2.78109
    g12: LineSegment StartX=38.8952 StartY=-231.233 StartZ=0 EndX=39.9512 EndY=-228.425 EndZ=0
    g13: ArcOfCircle CenterX=46.9911 CenterY=-209.705 CenterZ=0 NormalX=0 NormalY=0 NormalZ=1 AngleXU=0 Radius=20 StartAngle=2.78766 EndAngle=4.35269
    g14: LineSegment StartX=23.7323 StartY=-126.969 StartZ=0 EndX=17.4091 EndY=-143.817 EndZ=0
    g15: ArcOfCircle CenterX=29.5716 CenterY=-148.408 CenterZ=0 NormalX=0 NormalY=0 NormalZ=1 AngleXU=0 Radius=13 StartAngle=2.78068 EndAngle=4.35262
    g16: ArcOfCircle CenterX=35.8967 CenterY=-131.555 CenterZ=0 NormalX=0 NormalY=0 NormalZ=1 AngleXU=0 Radius=13 StartAngle=1.21584 EndAngle=2.78109
    g17: ArcOfCircle CenterX=48.1805 CenterY=-98.7782 CenterZ=0 NormalX=0 NormalY=0 NormalZ=1 AngleXU=0 Radius=13 StartAngle=2.78068 EndAngle=4.35005
    g18: LineSegment StartX=42.354 StartY=-77.3391 StartZ=0 EndX=36.018 EndY=-94.1875 EndZ=0
    g19: ArcOfCircle CenterX=54.5183 CenterY=-81.9247 CenterZ=0 NormalX=0 NormalY=0 NormalZ=1 AngleXU=0 Radius=13 StartAngle=2.42113 EndAngle=2.78109
    g20: ArcOfCircle CenterX=20.184 CenterY=-217.506 CenterZ=0 NormalX=0 NormalY=0 NormalZ=1 AngleXU=0 Radius=3.81084 StartAngle=1.88136 EndAngle=6.80465
    g21: LineSegment StartX=38.4753 StartY=-115.966 StartZ=0 EndX=41.2852 EndY=-117.017 EndZ=0
    g22: ArcOfCircle CenterX=36.3663 CenterY=-113.042 CenterZ=0 NormalX=0 NormalY=0 NormalZ=1 AngleXU=0 Radius=3.60555 StartAngle=0.230024 EndAngle=5.3372
    g23: LineSegment StartX=39.8769 StartY=-112.22 StartZ=0 EndX=42.6867 EndY=-113.271 EndZ=0
    g24: LineSegment StartX=19.9036 StartY=-165.61 StartZ=0 EndX=22.7134 EndY=-166.661 EndZ=0
    g25: ArcOfCircle CenterX=17.7945 CenterY=-162.686 CenterZ=0 NormalX=0 NormalY=0 NormalZ=1 AngleXU=0 Radius=3.60555 StartAngle=0.230024 EndAngle=5.3372
    g26: LineSegment StartX=21.3051 StartY=-161.864 StartZ=0 EndX=24.1149 EndY=-162.915 EndZ=0
    g27: LineSegment StartX=41.085 StartY=-66.3176 StartZ=0 EndX=46.0385 EndY=-62.5254 EndZ=0
    g28: LineSegment StartX=48.9563 StartY=-66.3367 StartZ=0 EndX=44.7488 EndY=-73.3482 EndZ=0
    g29: ArcOfCircle CenterX=49.8795 CenterY=-62.6074 CenterZ=0 NormalX=0 NormalY=0 NormalZ=1 AngleXU=0 Radius=3.84187 StartAngle=4.46973 EndAngle=9.40343
    g30: LineSegment StartX=41.085 StartY=-66.3176 StartZ=0 EndX=8.65492 EndY=-152.553 EndZ=0
    g31: LineSegment StartX=43.5724 StartY=-110.934 StartZ=0 EndX=42.6867 EndY=-113.271 EndZ=0
    g32: LineSegment StartX=40.4148 StartY=-119.365 StartZ=0 EndX=41.2852 EndY=-117.017 EndZ=0
    g33: LineSegment StartX=21.8316 StartY=-169.001 StartZ=0 EndX=22.7134 EndY=-166.661 EndZ=0
    g34: LineSegment StartX=24.9948 StartY=-160.575 StartZ=0 EndX=24.1149 EndY=-162.915 EndZ=0
    g35: LineSegment StartX=23.1786 StartY=-202.622 StartZ=0 EndX=19.0195 EndY=-213.878 EndZ=0
    g36: LineSegment StartX=28.2308 StartY=-202.773 StartZ=0 EndX=23.4884 EndY=-215.608 EndZ=0
    g37: LineSegment StartX=-200.721 StartY=-141.122 StartZ=0 EndX=-79.0409 EndY=-186.881 EndZ=0
    g38: LineSegment StartX=-79.0409 StartY=-186.881 StartZ=0 EndX=-77.6329 EndY=-183.137 EndZ=0
    g39: LineSegment StartX=-76.2249 StartY=-179.393 StartZ=0 EndX=-72.8553 EndY=-180.66 EndZ=0
    g40: LineSegment StartX=-77.6329 StartY=-183.137 StartZ=0 EndX=-74.2633 EndY=-184.404 EndZ=0
    g41: ArcOfCircle CenterX=-71.1257 CenterY=-183.448 CenterZ=0 NormalX=0 NormalY=0 NormalZ=1 AngleXU=0 Radius=3.28025 StartAngle=3.43759 EndAngle=8.40938
    g42: LineSegment StartX=-76.2249 StartY=-179.393 StartZ=0 EndX=-74.4658 EndY=-174.715 EndZ=0
    g43: LineSegment StartX=-79.0409 StartY=-186.881 StartZ=0 EndX=38.8952 EndY=-231.233 EndZ=0
  constraints (81):
    c: Block(g9)
    c: Block(g11)
    c: InternalAlignment(g1,g0)
    c: InternalAlignment(g2,g0)
    c: Block(g0)
    c: Block(g4)
    c: Block(g8)
    c: Block(g5)
    c: Block(g6)
    c: Block(g7)
    c: Block(g13)
    c: Coincident(g12,g13)
    c: Block(g12)
    c: Coincident(g3,g0)
    c: Coincident(g10,g11)
    c: Coincident(g10,g9)
    c: Block(g15)
    c: Block(g16)
    c: Coincident(g14,g16)
    c: Coincident(g14,g15)
    c: Block(g17)
    c: Block(g19)
    c: Coincident(g18,g19)
    c: Coincident(g18,g17)
    c: Block(g20)
    c: Block(g22)
    c: Coincident(g23,g22)
    c: Coincident(g21,g22)
    c: Parallel(g23,g21)
    c: Block(g21)
    c: Block(g23)
    c: Block(g25)
    c: Coincident(g26,g25)
    c: Coincident(g24,g25)
    c: Parallel(g26,g24)
    c: Block(g24)
    c: Block(g26)
    c: Block(g27)
    c: Coincident(g29,g27)
    c: Coincident(g29,g28)
    c: Block(g29)
    c: Coincident(g30,g27)
    c: Coincident(g30,g0)
    c: Block(g28)
    c: Coincident(g31,g23)
    c: Block(g31)
    c: Coincident(g32,g21)
    c: Block(g32)
    c: Coincident(g33,g24)
    c: Coincident(g34,g26)
    c: Block(g34)
    c: Block(g33)
    c: Coincident(g35,g9)
    c: Coincident(g35,g20)
    c: Block(g35)
    c: Coincident(g11,g33)
    c: Coincident(g15,g34)
    c: Coincident(g16,g32)
    c: Coincident(g17,g31)
    c: Coincident(g19,g28)
    c: Coincident(g36,g13)
    c: Coincident(g36,g20)
    c: Coincident(g37,g3)
    c: Block(g3)
    c: Perpendicular(g37,g3)
    c: Distance(g37) = 130
    c: Coincident(g38,g37)
    c: Distance(g38) = 4
    c: Perpendicular(g37,g38)
    c: Distance(g39) = 3.6
    c: Coincident(g40,g38)
    c: Distance(g40) = 3.6
    c: Block(g39)
    c: Block(g40)
    c: Coincident(g41,g39)
    c: Coincident(g41,g40)
    c: Coincident(g42,g39)
    c: Parallel(g38,g42)
    c: PointOnObject(g42,g0)
    c: Coincident(g43,g37)
    c: Coincident(g43,g12)
